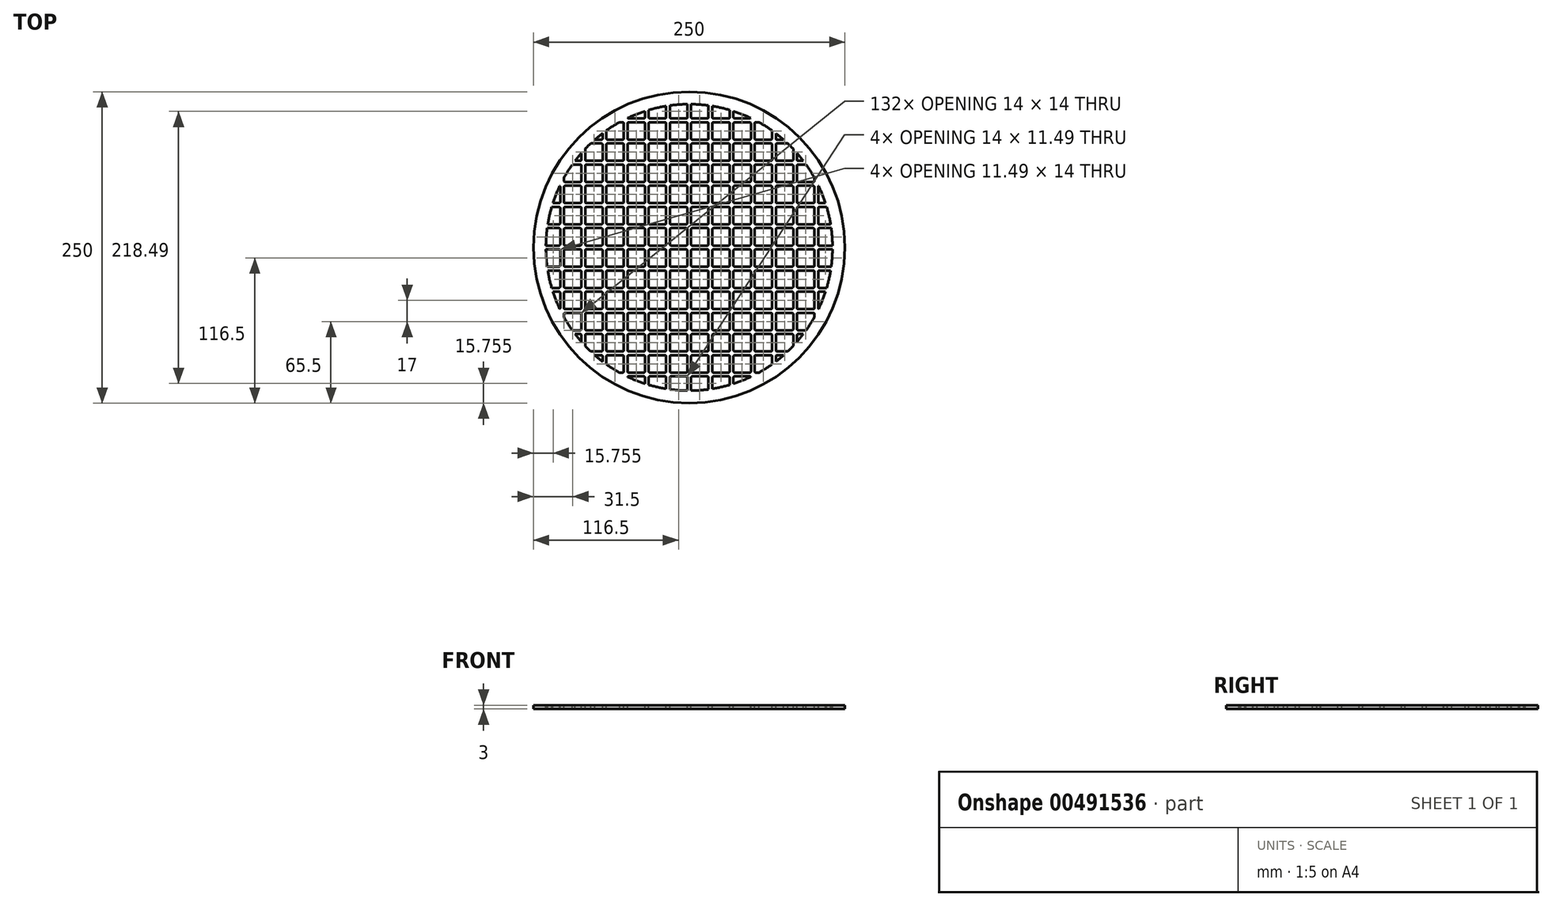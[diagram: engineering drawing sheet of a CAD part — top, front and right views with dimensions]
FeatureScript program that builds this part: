
annotation { "Feature Type Name" : "Feature", "Feature Type Description" : "" }
export const myFeature = defineFeature(function(context is Context, id is Id, definition is map)
    precondition{}
    {
        {
            var Q0;
            Q0=qCreatedBy(makeId("Top.planeOp"),FACE);
            var sketch = newSketch(context, id + "F0", { "sketchPlane" : qUnion([Q0])});
            skCircle(sketch, "E0", {"center": v(0, 0) * mm, "radius": 125 * mm});
            skSolve(sketch);
        }
        {
            var Q0;
            Q0 = qSketchRegion(id + "F0", true);
            extrude(context, id + "F1", {"entities" : qUnion([Q0]), "depth" : 3 * mm});
        }
        {
            var Q0;
            Q0=makeQuery(id+"F1.opExtrude","CAP_FACE",FACE,{"disambiguationData":[OSD([sQuery(id+"F0.wireOp",EDGE,"E0")])],"isStart":false});
            var sketch = newSketch(context, id + "F2", { "sketchPlane" : qUnion([Q0])});
            skLineSegment(sketch, "E1.bottom", {"start": v(2.5, 1.5) * mm, "end": v(14.5, 1.5) * mm});
            skLineSegment(sketch, "E1.top", {"start": v(2.5, 15.5) * mm, "end": v(14.5, 15.5) * mm});
            skLineSegment(sketch, "E1.left", {"start": v(1.5, 2.5) * mm, "end": v(1.5, 14.5) * mm});
            skLineSegment(sketch, "E1.right", {"start": v(15.5, 2.5) * mm, "end": v(15.5, 14.5) * mm});
            skPoint(sketch, "E2.visualSharp", {"position": v(1.5, 15.5) * mm});
            skArc(sketch, "E2.filletArc", {"start": v(2.5, 15.5) * mm, "mid": v(1.8, 15.2) * mm, "end": v(1.5, 14.5) * mm});
            skPoint(sketch, "E3.visualSharp", {"position": v(15.5, 15.5) * mm});
            skArc(sketch, "E3.filletArc", {"start": v(15.5, 14.5) * mm, "mid": v(15.2, 15.2) * mm, "end": v(14.5, 15.5) * mm});
            skPoint(sketch, "E4.visualSharp", {"position": v(1.5, 1.5) * mm});
            skArc(sketch, "E4.filletArc", {"start": v(1.5, 2.5) * mm, "mid": v(1.8, 1.8) * mm, "end": v(2.5, 1.5) * mm});
            skPoint(sketch, "E5.visualSharp", {"position": v(15.5, 1.5) * mm});
            skArc(sketch, "E5.filletArc", {"start": v(14.5, 1.5) * mm, "mid": v(15.2, 1.8) * mm, "end": v(15.5, 2.5) * mm});
            skLineSegment(sketch, "E6.0.1.0", {"start": v(2.5, 18.5) * mm, "end": v(14.5, 18.5) * mm});
            skPoint(sketch, "E6.0.1.1", {"position": v(1.5, 32.5) * mm});
            skArc(sketch, "E6.0.1.2", {"start": v(14.5, 18.5) * mm, "mid": v(15.2, 18.8) * mm, "end": v(15.5, 19.5) * mm});
            skLineSegment(sketch, "E6.0.1.3", {"start": v(15.5, 19.5) * mm, "end": v(15.5, 31.5) * mm});
            skArc(sketch, "E6.0.1.4", {"start": v(15.5, 31.5) * mm, "mid": v(15.2, 32.2) * mm, "end": v(14.5, 32.5) * mm});
            skLineSegment(sketch, "E6.0.1.5", {"start": v(1.5, 19.5) * mm, "end": v(1.5, 31.5) * mm});
            skPoint(sketch, "E6.0.1.6", {"position": v(1.5, 18.5) * mm});
            skArc(sketch, "E6.0.1.7", {"start": v(2.5, 32.5) * mm, "mid": v(1.8, 32.2) * mm, "end": v(1.5, 31.5) * mm});
            skLineSegment(sketch, "E6.0.1.8", {"start": v(2.5, 32.5) * mm, "end": v(14.5, 32.5) * mm});
            skPoint(sketch, "E6.0.1.9", {"position": v(15.5, 32.5) * mm});
            skPoint(sketch, "E6.0.1.10", {"position": v(15.5, 18.5) * mm});
            skArc(sketch, "E6.0.1.11", {"start": v(1.5, 19.5) * mm, "mid": v(1.8, 18.8) * mm, "end": v(2.5, 18.5) * mm});
            skLineSegment(sketch, "E6.0.2.0", {"start": v(2.5, 35.5) * mm, "end": v(14.5, 35.5) * mm});
            skPoint(sketch, "E6.0.2.1", {"position": v(1.5, 49.5) * mm});
            skArc(sketch, "E6.0.2.2", {"start": v(14.5, 35.5) * mm, "mid": v(15.2, 35.8) * mm, "end": v(15.5, 36.5) * mm});
            skLineSegment(sketch, "E6.0.2.3", {"start": v(15.5, 36.5) * mm, "end": v(15.5, 48.5) * mm});
            skArc(sketch, "E6.0.2.4", {"start": v(15.5, 48.5) * mm, "mid": v(15.2, 49.2) * mm, "end": v(14.5, 49.5) * mm});
            skLineSegment(sketch, "E6.0.2.5", {"start": v(1.5, 36.5) * mm, "end": v(1.5, 48.5) * mm});
            skPoint(sketch, "E6.0.2.6", {"position": v(1.5, 35.5) * mm});
            skArc(sketch, "E6.0.2.7", {"start": v(2.5, 49.5) * mm, "mid": v(1.8, 49.2) * mm, "end": v(1.5, 48.5) * mm});
            skLineSegment(sketch, "E6.0.2.8", {"start": v(2.5, 49.5) * mm, "end": v(14.5, 49.5) * mm});
            skPoint(sketch, "E6.0.2.9", {"position": v(15.5, 49.5) * mm});
            skPoint(sketch, "E6.0.2.10", {"position": v(15.5, 35.5) * mm});
            skArc(sketch, "E6.0.2.11", {"start": v(1.5, 36.5) * mm, "mid": v(1.8, 35.8) * mm, "end": v(2.5, 35.5) * mm});
            skLineSegment(sketch, "E6.0.3.0", {"start": v(2.5, 52.5) * mm, "end": v(14.5, 52.5) * mm});
            skPoint(sketch, "E6.0.3.1", {"position": v(1.5, 66.5) * mm});
            skArc(sketch, "E6.0.3.2", {"start": v(14.5, 52.5) * mm, "mid": v(15.2, 52.8) * mm, "end": v(15.5, 53.5) * mm});
            skLineSegment(sketch, "E6.0.3.3", {"start": v(15.5, 53.5) * mm, "end": v(15.5, 65.5) * mm});
            skArc(sketch, "E6.0.3.4", {"start": v(15.5, 65.5) * mm, "mid": v(15.2, 66.2) * mm, "end": v(14.5, 66.5) * mm});
            skLineSegment(sketch, "E6.0.3.5", {"start": v(1.5, 53.5) * mm, "end": v(1.5, 65.5) * mm});
            skPoint(sketch, "E6.0.3.6", {"position": v(1.5, 52.5) * mm});
            skArc(sketch, "E6.0.3.7", {"start": v(2.5, 66.5) * mm, "mid": v(1.8, 66.2) * mm, "end": v(1.5, 65.5) * mm});
            skLineSegment(sketch, "E6.0.3.8", {"start": v(2.5, 66.5) * mm, "end": v(14.5, 66.5) * mm});
            skPoint(sketch, "E6.0.3.9", {"position": v(15.5, 66.5) * mm});
            skPoint(sketch, "E6.0.3.10", {"position": v(15.5, 52.5) * mm});
            skArc(sketch, "E6.0.3.11", {"start": v(1.5, 53.5) * mm, "mid": v(1.8, 52.8) * mm, "end": v(2.5, 52.5) * mm});
            skLineSegment(sketch, "E6.0.4.0", {"start": v(2.5, 69.5) * mm, "end": v(14.5, 69.5) * mm});
            skPoint(sketch, "E6.0.4.1", {"position": v(1.5, 83.5) * mm});
            skArc(sketch, "E6.0.4.2", {"start": v(14.5, 69.5) * mm, "mid": v(15.2, 69.8) * mm, "end": v(15.5, 70.5) * mm});
            skLineSegment(sketch, "E6.0.4.3", {"start": v(15.5, 70.5) * mm, "end": v(15.5, 82.5) * mm});
            skArc(sketch, "E6.0.4.4", {"start": v(15.5, 82.5) * mm, "mid": v(15.2, 83.2) * mm, "end": v(14.5, 83.5) * mm});
            skLineSegment(sketch, "E6.0.4.5", {"start": v(1.5, 70.5) * mm, "end": v(1.5, 82.5) * mm});
            skPoint(sketch, "E6.0.4.6", {"position": v(1.5, 69.5) * mm});
            skArc(sketch, "E6.0.4.7", {"start": v(2.5, 83.5) * mm, "mid": v(1.8, 83.2) * mm, "end": v(1.5, 82.5) * mm});
            skLineSegment(sketch, "E6.0.4.8", {"start": v(2.5, 83.5) * mm, "end": v(14.5, 83.5) * mm});
            skPoint(sketch, "E6.0.4.9", {"position": v(15.5, 83.5) * mm});
            skPoint(sketch, "E6.0.4.10", {"position": v(15.5, 69.5) * mm});
            skArc(sketch, "E6.0.4.11", {"start": v(1.5, 70.5) * mm, "mid": v(1.8, 69.8) * mm, "end": v(2.5, 69.5) * mm});
            skLineSegment(sketch, "E6.0.5.0", {"start": v(2.5, 86.5) * mm, "end": v(14.5, 86.5) * mm});
            skPoint(sketch, "E6.0.5.1", {"position": v(1.5, 100.5) * mm});
            skArc(sketch, "E6.0.5.2", {"start": v(14.5, 86.5) * mm, "mid": v(15.2, 86.8) * mm, "end": v(15.5, 87.5) * mm});
            skLineSegment(sketch, "E6.0.5.3", {"start": v(15.5, 87.5) * mm, "end": v(15.5, 99.5) * mm});
            skArc(sketch, "E6.0.5.4", {"start": v(15.5, 99.5) * mm, "mid": v(15.2, 100.2) * mm, "end": v(14.5, 100.5) * mm});
            skLineSegment(sketch, "E6.0.5.5", {"start": v(1.5, 87.5) * mm, "end": v(1.5, 99.5) * mm});
            skPoint(sketch, "E6.0.5.6", {"position": v(1.5, 86.5) * mm});
            skArc(sketch, "E6.0.5.7", {"start": v(2.5, 100.5) * mm, "mid": v(1.8, 100.2) * mm, "end": v(1.5, 99.5) * mm});
            skLineSegment(sketch, "E6.0.5.8", {"start": v(2.5, 100.5) * mm, "end": v(14.5, 100.5) * mm});
            skPoint(sketch, "E6.0.5.9", {"position": v(15.5, 100.5) * mm});
            skPoint(sketch, "E6.0.5.10", {"position": v(15.5, 86.5) * mm});
            skArc(sketch, "E6.0.5.11", {"start": v(1.5, 87.5) * mm, "mid": v(1.8, 86.8) * mm, "end": v(2.5, 86.5) * mm});
            skLineSegment(sketch, "E6.0.6.0", {"start": v(2.5, 103.5) * mm, "end": v(14.5, 103.5) * mm});
            skArc(sketch, "E6.0.6.2", {"start": v(14.5, 103.5) * mm, "mid": v(15.2, 103.8) * mm, "end": v(15.5, 104.5) * mm});
            skLineSegment(sketch, "E6.0.6.3", {"start": v(15.5, 104.5) * mm, "end": v(15.5, 113.95) * mm});
            skLineSegment(sketch, "E6.0.6.5", {"start": v(1.5, 104.5) * mm, "end": v(1.5, 115) * mm});
            skPoint(sketch, "E6.0.6.6", {"position": v(1.5, 103.5) * mm});
            skPoint(sketch, "E6.0.6.10", {"position": v(15.5, 103.5) * mm});
            skArc(sketch, "E6.0.6.11", {"start": v(1.5, 104.5) * mm, "mid": v(1.8, 103.8) * mm, "end": v(2.5, 103.5) * mm});
            skLineSegment(sketch, "E6.1.0.0", {"start": v(19.5, 1.5) * mm, "end": v(31.5, 1.5) * mm});
            skPoint(sketch, "E6.1.0.1", {"position": v(18.5, 15.5) * mm});
            skArc(sketch, "E6.1.0.2", {"start": v(31.5, 1.5) * mm, "mid": v(32.2, 1.8) * mm, "end": v(32.5, 2.5) * mm});
            skLineSegment(sketch, "E6.1.0.3", {"start": v(32.5, 2.5) * mm, "end": v(32.5, 14.5) * mm});
            skArc(sketch, "E6.1.0.4", {"start": v(32.5, 14.5) * mm, "mid": v(32.2, 15.2) * mm, "end": v(31.5, 15.5) * mm});
            skLineSegment(sketch, "E6.1.0.5", {"start": v(18.5, 2.5) * mm, "end": v(18.5, 14.5) * mm});
            skPoint(sketch, "E6.1.0.6", {"position": v(18.5, 1.5) * mm});
            skArc(sketch, "E6.1.0.7", {"start": v(19.5, 15.5) * mm, "mid": v(18.8, 15.2) * mm, "end": v(18.5, 14.5) * mm});
            skLineSegment(sketch, "E6.1.0.8", {"start": v(19.5, 15.5) * mm, "end": v(31.5, 15.5) * mm});
            skPoint(sketch, "E6.1.0.9", {"position": v(32.5, 15.5) * mm});
            skPoint(sketch, "E6.1.0.10", {"position": v(32.5, 1.5) * mm});
            skArc(sketch, "E6.1.0.11", {"start": v(18.5, 2.5) * mm, "mid": v(18.8, 1.8) * mm, "end": v(19.5, 1.5) * mm});
            skLineSegment(sketch, "E6.1.1.0", {"start": v(19.5, 18.5) * mm, "end": v(31.5, 18.5) * mm});
            skPoint(sketch, "E6.1.1.1", {"position": v(18.5, 32.5) * mm});
            skArc(sketch, "E6.1.1.2", {"start": v(31.5, 18.5) * mm, "mid": v(32.2, 18.8) * mm, "end": v(32.5, 19.5) * mm});
            skLineSegment(sketch, "E6.1.1.3", {"start": v(32.5, 19.5) * mm, "end": v(32.5, 31.5) * mm});
            skArc(sketch, "E6.1.1.4", {"start": v(32.5, 31.5) * mm, "mid": v(32.2, 32.2) * mm, "end": v(31.5, 32.5) * mm});
            skLineSegment(sketch, "E6.1.1.5", {"start": v(18.5, 19.5) * mm, "end": v(18.5, 31.5) * mm});
            skPoint(sketch, "E6.1.1.6", {"position": v(18.5, 18.5) * mm});
            skArc(sketch, "E6.1.1.7", {"start": v(19.5, 32.5) * mm, "mid": v(18.8, 32.2) * mm, "end": v(18.5, 31.5) * mm});
            skLineSegment(sketch, "E6.1.1.8", {"start": v(19.5, 32.5) * mm, "end": v(31.5, 32.5) * mm});
            skPoint(sketch, "E6.1.1.9", {"position": v(32.5, 32.5) * mm});
            skPoint(sketch, "E6.1.1.10", {"position": v(32.5, 18.5) * mm});
            skArc(sketch, "E6.1.1.11", {"start": v(18.5, 19.5) * mm, "mid": v(18.8, 18.8) * mm, "end": v(19.5, 18.5) * mm});
            skLineSegment(sketch, "E6.1.2.0", {"start": v(19.5, 35.5) * mm, "end": v(31.5, 35.5) * mm});
            skPoint(sketch, "E6.1.2.1", {"position": v(18.5, 49.5) * mm});
            skArc(sketch, "E6.1.2.2", {"start": v(31.5, 35.5) * mm, "mid": v(32.2, 35.8) * mm, "end": v(32.5, 36.5) * mm});
            skLineSegment(sketch, "E6.1.2.3", {"start": v(32.5, 36.5) * mm, "end": v(32.5, 48.5) * mm});
            skArc(sketch, "E6.1.2.4", {"start": v(32.5, 48.5) * mm, "mid": v(32.2, 49.2) * mm, "end": v(31.5, 49.5) * mm});
            skLineSegment(sketch, "E6.1.2.5", {"start": v(18.5, 36.5) * mm, "end": v(18.5, 48.5) * mm});
            skPoint(sketch, "E6.1.2.6", {"position": v(18.5, 35.5) * mm});
            skArc(sketch, "E6.1.2.7", {"start": v(19.5, 49.5) * mm, "mid": v(18.8, 49.2) * mm, "end": v(18.5, 48.5) * mm});
            skLineSegment(sketch, "E6.1.2.8", {"start": v(19.5, 49.5) * mm, "end": v(31.5, 49.5) * mm});
            skPoint(sketch, "E6.1.2.9", {"position": v(32.5, 49.5) * mm});
            skPoint(sketch, "E6.1.2.10", {"position": v(32.5, 35.5) * mm});
            skArc(sketch, "E6.1.2.11", {"start": v(18.5, 36.5) * mm, "mid": v(18.8, 35.8) * mm, "end": v(19.5, 35.5) * mm});
            skLineSegment(sketch, "E6.1.3.0", {"start": v(19.5, 52.5) * mm, "end": v(31.5, 52.5) * mm});
            skPoint(sketch, "E6.1.3.1", {"position": v(18.5, 66.5) * mm});
            skArc(sketch, "E6.1.3.2", {"start": v(31.5, 52.5) * mm, "mid": v(32.2, 52.8) * mm, "end": v(32.5, 53.5) * mm});
            skLineSegment(sketch, "E6.1.3.3", {"start": v(32.5, 53.5) * mm, "end": v(32.5, 65.5) * mm});
            skArc(sketch, "E6.1.3.4", {"start": v(32.5, 65.5) * mm, "mid": v(32.2, 66.2) * mm, "end": v(31.5, 66.5) * mm});
            skLineSegment(sketch, "E6.1.3.5", {"start": v(18.5, 53.5) * mm, "end": v(18.5, 65.5) * mm});
            skPoint(sketch, "E6.1.3.6", {"position": v(18.5, 52.5) * mm});
            skArc(sketch, "E6.1.3.7", {"start": v(19.5, 66.5) * mm, "mid": v(18.8, 66.2) * mm, "end": v(18.5, 65.5) * mm});
            skLineSegment(sketch, "E6.1.3.8", {"start": v(19.5, 66.5) * mm, "end": v(31.5, 66.5) * mm});
            skPoint(sketch, "E6.1.3.9", {"position": v(32.5, 66.5) * mm});
            skPoint(sketch, "E6.1.3.10", {"position": v(32.5, 52.5) * mm});
            skArc(sketch, "E6.1.3.11", {"start": v(18.5, 53.5) * mm, "mid": v(18.8, 52.8) * mm, "end": v(19.5, 52.5) * mm});
            skLineSegment(sketch, "E6.1.4.0", {"start": v(19.5, 69.5) * mm, "end": v(31.5, 69.5) * mm});
            skPoint(sketch, "E6.1.4.1", {"position": v(18.5, 83.5) * mm});
            skArc(sketch, "E6.1.4.2", {"start": v(31.5, 69.5) * mm, "mid": v(32.2, 69.8) * mm, "end": v(32.5, 70.5) * mm});
            skLineSegment(sketch, "E6.1.4.3", {"start": v(32.5, 70.5) * mm, "end": v(32.5, 82.5) * mm});
            skArc(sketch, "E6.1.4.4", {"start": v(32.5, 82.5) * mm, "mid": v(32.2, 83.2) * mm, "end": v(31.5, 83.5) * mm});
            skLineSegment(sketch, "E6.1.4.5", {"start": v(18.5, 70.5) * mm, "end": v(18.5, 82.5) * mm});
            skPoint(sketch, "E6.1.4.6", {"position": v(18.5, 69.5) * mm});
            skArc(sketch, "E6.1.4.7", {"start": v(19.5, 83.5) * mm, "mid": v(18.8, 83.2) * mm, "end": v(18.5, 82.5) * mm});
            skLineSegment(sketch, "E6.1.4.8", {"start": v(19.5, 83.5) * mm, "end": v(31.5, 83.5) * mm});
            skPoint(sketch, "E6.1.4.9", {"position": v(32.5, 83.5) * mm});
            skPoint(sketch, "E6.1.4.10", {"position": v(32.5, 69.5) * mm});
            skArc(sketch, "E6.1.4.11", {"start": v(18.5, 70.5) * mm, "mid": v(18.8, 69.8) * mm, "end": v(19.5, 69.5) * mm});
            skLineSegment(sketch, "E6.1.5.0", {"start": v(19.5, 86.5) * mm, "end": v(31.5, 86.5) * mm});
            skPoint(sketch, "E6.1.5.1", {"position": v(18.5, 100.5) * mm});
            skArc(sketch, "E6.1.5.2", {"start": v(31.5, 86.5) * mm, "mid": v(32.2, 86.8) * mm, "end": v(32.5, 87.5) * mm});
            skLineSegment(sketch, "E6.1.5.3", {"start": v(32.5, 87.5) * mm, "end": v(32.5, 99.5) * mm});
            skArc(sketch, "E6.1.5.4", {"start": v(32.5, 99.5) * mm, "mid": v(32.2, 100.2) * mm, "end": v(31.5, 100.5) * mm});
            skLineSegment(sketch, "E6.1.5.5", {"start": v(18.5, 87.5) * mm, "end": v(18.5, 99.5) * mm});
            skPoint(sketch, "E6.1.5.6", {"position": v(18.5, 86.5) * mm});
            skArc(sketch, "E6.1.5.7", {"start": v(19.5, 100.5) * mm, "mid": v(18.8, 100.2) * mm, "end": v(18.5, 99.5) * mm});
            skLineSegment(sketch, "E6.1.5.8", {"start": v(19.5, 100.5) * mm, "end": v(31.5, 100.5) * mm});
            skPoint(sketch, "E6.1.5.9", {"position": v(32.5, 100.5) * mm});
            skPoint(sketch, "E6.1.5.10", {"position": v(32.5, 86.5) * mm});
            skArc(sketch, "E6.1.5.11", {"start": v(18.5, 87.5) * mm, "mid": v(18.8, 86.8) * mm, "end": v(19.5, 86.5) * mm});
            skLineSegment(sketch, "E6.1.6.0", {"start": v(19.5, 103.5) * mm, "end": v(31.5, 103.5) * mm});
            skArc(sketch, "E6.1.6.2", {"start": v(31.5, 103.5) * mm, "mid": v(32.2, 103.8) * mm, "end": v(32.5, 104.5) * mm});
            skLineSegment(sketch, "E6.1.6.3", {"start": v(32.5, 104.5) * mm, "end": v(32.5, 110.31) * mm});
            skLineSegment(sketch, "E6.1.6.5", {"start": v(18.5, 104.5) * mm, "end": v(18.5, 113.5) * mm});
            skPoint(sketch, "E6.1.6.6", {"position": v(18.5, 103.5) * mm});
            skPoint(sketch, "E6.1.6.10", {"position": v(32.5, 103.5) * mm});
            skArc(sketch, "E6.1.6.11", {"start": v(18.5, 104.5) * mm, "mid": v(18.8, 103.8) * mm, "end": v(19.5, 103.5) * mm});
            skLineSegment(sketch, "E6.2.0.0", {"start": v(36.5, 1.5) * mm, "end": v(48.5, 1.5) * mm});
            skPoint(sketch, "E6.2.0.1", {"position": v(35.5, 15.5) * mm});
            skArc(sketch, "E6.2.0.2", {"start": v(48.5, 1.5) * mm, "mid": v(49.2, 1.8) * mm, "end": v(49.5, 2.5) * mm});
            skLineSegment(sketch, "E6.2.0.3", {"start": v(49.5, 2.5) * mm, "end": v(49.5, 14.5) * mm});
            skArc(sketch, "E6.2.0.4", {"start": v(49.5, 14.5) * mm, "mid": v(49.2, 15.2) * mm, "end": v(48.5, 15.5) * mm});
            skLineSegment(sketch, "E6.2.0.5", {"start": v(35.5, 2.5) * mm, "end": v(35.5, 14.5) * mm});
            skPoint(sketch, "E6.2.0.6", {"position": v(35.5, 1.5) * mm});
            skArc(sketch, "E6.2.0.7", {"start": v(36.5, 15.5) * mm, "mid": v(35.8, 15.2) * mm, "end": v(35.5, 14.5) * mm});
            skLineSegment(sketch, "E6.2.0.8", {"start": v(36.5, 15.5) * mm, "end": v(48.5, 15.5) * mm});
            skPoint(sketch, "E6.2.0.9", {"position": v(49.5, 15.5) * mm});
            skPoint(sketch, "E6.2.0.10", {"position": v(49.5, 1.5) * mm});
            skArc(sketch, "E6.2.0.11", {"start": v(35.5, 2.5) * mm, "mid": v(35.8, 1.8) * mm, "end": v(36.5, 1.5) * mm});
            skLineSegment(sketch, "E6.2.1.0", {"start": v(36.5, 18.5) * mm, "end": v(48.5, 18.5) * mm});
            skPoint(sketch, "E6.2.1.1", {"position": v(35.5, 32.5) * mm});
            skArc(sketch, "E6.2.1.2", {"start": v(48.5, 18.5) * mm, "mid": v(49.2, 18.8) * mm, "end": v(49.5, 19.5) * mm});
            skLineSegment(sketch, "E6.2.1.3", {"start": v(49.5, 19.5) * mm, "end": v(49.5, 31.5) * mm});
            skArc(sketch, "E6.2.1.4", {"start": v(49.5, 31.5) * mm, "mid": v(49.2, 32.2) * mm, "end": v(48.5, 32.5) * mm});
            skLineSegment(sketch, "E6.2.1.5", {"start": v(35.5, 19.5) * mm, "end": v(35.5, 31.5) * mm});
            skPoint(sketch, "E6.2.1.6", {"position": v(35.5, 18.5) * mm});
            skArc(sketch, "E6.2.1.7", {"start": v(36.5, 32.5) * mm, "mid": v(35.8, 32.2) * mm, "end": v(35.5, 31.5) * mm});
            skLineSegment(sketch, "E6.2.1.8", {"start": v(36.5, 32.5) * mm, "end": v(48.5, 32.5) * mm});
            skPoint(sketch, "E6.2.1.9", {"position": v(49.5, 32.5) * mm});
            skPoint(sketch, "E6.2.1.10", {"position": v(49.5, 18.5) * mm});
            skArc(sketch, "E6.2.1.11", {"start": v(35.5, 19.5) * mm, "mid": v(35.8, 18.8) * mm, "end": v(36.5, 18.5) * mm});
            skLineSegment(sketch, "E6.2.2.0", {"start": v(36.5, 35.5) * mm, "end": v(48.5, 35.5) * mm});
            skPoint(sketch, "E6.2.2.1", {"position": v(35.5, 49.5) * mm});
            skArc(sketch, "E6.2.2.2", {"start": v(48.5, 35.5) * mm, "mid": v(49.2, 35.8) * mm, "end": v(49.5, 36.5) * mm});
            skLineSegment(sketch, "E6.2.2.3", {"start": v(49.5, 36.5) * mm, "end": v(49.5, 48.5) * mm});
            skArc(sketch, "E6.2.2.4", {"start": v(49.5, 48.5) * mm, "mid": v(49.2, 49.2) * mm, "end": v(48.5, 49.5) * mm});
            skLineSegment(sketch, "E6.2.2.5", {"start": v(35.5, 36.5) * mm, "end": v(35.5, 48.5) * mm});
            skPoint(sketch, "E6.2.2.6", {"position": v(35.5, 35.5) * mm});
            skArc(sketch, "E6.2.2.7", {"start": v(36.5, 49.5) * mm, "mid": v(35.8, 49.2) * mm, "end": v(35.5, 48.5) * mm});
            skLineSegment(sketch, "E6.2.2.8", {"start": v(36.5, 49.5) * mm, "end": v(48.5, 49.5) * mm});
            skPoint(sketch, "E6.2.2.9", {"position": v(49.5, 49.5) * mm});
            skPoint(sketch, "E6.2.2.10", {"position": v(49.5, 35.5) * mm});
            skArc(sketch, "E6.2.2.11", {"start": v(35.5, 36.5) * mm, "mid": v(35.8, 35.8) * mm, "end": v(36.5, 35.5) * mm});
            skLineSegment(sketch, "E6.2.3.0", {"start": v(36.5, 52.5) * mm, "end": v(48.5, 52.5) * mm});
            skPoint(sketch, "E6.2.3.1", {"position": v(35.5, 66.5) * mm});
            skArc(sketch, "E6.2.3.2", {"start": v(48.5, 52.5) * mm, "mid": v(49.2, 52.8) * mm, "end": v(49.5, 53.5) * mm});
            skLineSegment(sketch, "E6.2.3.3", {"start": v(49.5, 53.5) * mm, "end": v(49.5, 65.5) * mm});
            skArc(sketch, "E6.2.3.4", {"start": v(49.5, 65.5) * mm, "mid": v(49.2, 66.2) * mm, "end": v(48.5, 66.5) * mm});
            skLineSegment(sketch, "E6.2.3.5", {"start": v(35.5, 53.5) * mm, "end": v(35.5, 65.5) * mm});
            skPoint(sketch, "E6.2.3.6", {"position": v(35.5, 52.5) * mm});
            skArc(sketch, "E6.2.3.7", {"start": v(36.5, 66.5) * mm, "mid": v(35.8, 66.2) * mm, "end": v(35.5, 65.5) * mm});
            skLineSegment(sketch, "E6.2.3.8", {"start": v(36.5, 66.5) * mm, "end": v(48.5, 66.5) * mm});
            skPoint(sketch, "E6.2.3.9", {"position": v(49.5, 66.5) * mm});
            skPoint(sketch, "E6.2.3.10", {"position": v(49.5, 52.5) * mm});
            skArc(sketch, "E6.2.3.11", {"start": v(35.5, 53.5) * mm, "mid": v(35.8, 52.8) * mm, "end": v(36.5, 52.5) * mm});
            skLineSegment(sketch, "E6.2.4.0", {"start": v(36.5, 69.5) * mm, "end": v(48.5, 69.5) * mm});
            skPoint(sketch, "E6.2.4.1", {"position": v(35.5, 83.5) * mm});
            skArc(sketch, "E6.2.4.2", {"start": v(48.5, 69.5) * mm, "mid": v(49.2, 69.8) * mm, "end": v(49.5, 70.5) * mm});
            skLineSegment(sketch, "E6.2.4.3", {"start": v(49.5, 70.5) * mm, "end": v(49.5, 82.5) * mm});
            skArc(sketch, "E6.2.4.4", {"start": v(49.5, 82.5) * mm, "mid": v(49.2, 83.2) * mm, "end": v(48.5, 83.5) * mm});
            skLineSegment(sketch, "E6.2.4.5", {"start": v(35.5, 70.5) * mm, "end": v(35.5, 82.5) * mm});
            skPoint(sketch, "E6.2.4.6", {"position": v(35.5, 69.5) * mm});
            skArc(sketch, "E6.2.4.7", {"start": v(36.5, 83.5) * mm, "mid": v(35.8, 83.2) * mm, "end": v(35.5, 82.5) * mm});
            skLineSegment(sketch, "E6.2.4.8", {"start": v(36.5, 83.5) * mm, "end": v(48.5, 83.5) * mm});
            skPoint(sketch, "E6.2.4.9", {"position": v(49.5, 83.5) * mm});
            skPoint(sketch, "E6.2.4.10", {"position": v(49.5, 69.5) * mm});
            skArc(sketch, "E6.2.4.11", {"start": v(35.5, 70.5) * mm, "mid": v(35.8, 69.8) * mm, "end": v(36.5, 69.5) * mm});
            skLineSegment(sketch, "E6.2.5.0", {"start": v(36.5, 86.5) * mm, "end": v(48.5, 86.5) * mm});
            skPoint(sketch, "E6.2.5.1", {"position": v(35.5, 100.5) * mm});
            skArc(sketch, "E6.2.5.2", {"start": v(48.5, 86.5) * mm, "mid": v(49.2, 86.8) * mm, "end": v(49.5, 87.5) * mm});
            skLineSegment(sketch, "E6.2.5.3", {"start": v(49.5, 87.5) * mm, "end": v(49.5, 99.5) * mm});
            skArc(sketch, "E6.2.5.4", {"start": v(49.5, 99.5) * mm, "mid": v(49.2, 100.2) * mm, "end": v(48.5, 100.5) * mm});
            skLineSegment(sketch, "E6.2.5.5", {"start": v(35.5, 87.5) * mm, "end": v(35.5, 99.5) * mm});
            skPoint(sketch, "E6.2.5.6", {"position": v(35.5, 86.5) * mm});
            skArc(sketch, "E6.2.5.7", {"start": v(36.5, 100.5) * mm, "mid": v(35.8, 100.2) * mm, "end": v(35.5, 99.5) * mm});
            skLineSegment(sketch, "E6.2.5.8", {"start": v(36.5, 100.5) * mm, "end": v(48.5, 100.5) * mm});
            skPoint(sketch, "E6.2.5.9", {"position": v(49.5, 100.5) * mm});
            skPoint(sketch, "E6.2.5.10", {"position": v(49.5, 86.5) * mm});
            skArc(sketch, "E6.2.5.11", {"start": v(35.5, 87.5) * mm, "mid": v(35.8, 86.8) * mm, "end": v(36.5, 86.5) * mm});
            skLineSegment(sketch, "E6.2.6.0", {"start": v(36.5, 103.5) * mm, "end": v(48.5, 103.5) * mm});
            skArc(sketch, "E6.2.6.2", {"start": v(48.5, 103.5) * mm, "mid": v(48.95, 103.6) * mm, "end": v(49.3, 103.9) * mm});
            skLineSegment(sketch, "E6.2.6.5", {"start": v(35.5, 104.5) * mm, "end": v(35.5, 109.38) * mm});
            skPoint(sketch, "E6.2.6.6", {"position": v(35.5, 103.5) * mm});
            skPoint(sketch, "E6.2.6.10", {"position": v(49.5, 103.5) * mm});
            skArc(sketch, "E6.2.6.11", {"start": v(35.5, 104.5) * mm, "mid": v(35.8, 103.8) * mm, "end": v(36.5, 103.5) * mm});
            skLineSegment(sketch, "E6.3.0.0", {"start": v(53.5, 1.5) * mm, "end": v(65.5, 1.5) * mm});
            skPoint(sketch, "E6.3.0.1", {"position": v(52.5, 15.5) * mm});
            skArc(sketch, "E6.3.0.2", {"start": v(65.5, 1.5) * mm, "mid": v(66.2, 1.8) * mm, "end": v(66.5, 2.5) * mm});
            skLineSegment(sketch, "E6.3.0.3", {"start": v(66.5, 2.5) * mm, "end": v(66.5, 14.5) * mm});
            skArc(sketch, "E6.3.0.4", {"start": v(66.5, 14.5) * mm, "mid": v(66.2, 15.2) * mm, "end": v(65.5, 15.5) * mm});
            skLineSegment(sketch, "E6.3.0.5", {"start": v(52.5, 2.5) * mm, "end": v(52.5, 14.5) * mm});
            skPoint(sketch, "E6.3.0.6", {"position": v(52.5, 1.5) * mm});
            skArc(sketch, "E6.3.0.7", {"start": v(53.5, 15.5) * mm, "mid": v(52.8, 15.2) * mm, "end": v(52.5, 14.5) * mm});
            skLineSegment(sketch, "E6.3.0.8", {"start": v(53.5, 15.5) * mm, "end": v(65.5, 15.5) * mm});
            skPoint(sketch, "E6.3.0.9", {"position": v(66.5, 15.5) * mm});
            skPoint(sketch, "E6.3.0.10", {"position": v(66.5, 1.5) * mm});
            skArc(sketch, "E6.3.0.11", {"start": v(52.5, 2.5) * mm, "mid": v(52.8, 1.8) * mm, "end": v(53.5, 1.5) * mm});
            skLineSegment(sketch, "E6.3.1.0", {"start": v(53.5, 18.5) * mm, "end": v(65.5, 18.5) * mm});
            skPoint(sketch, "E6.3.1.1", {"position": v(52.5, 32.5) * mm});
            skArc(sketch, "E6.3.1.2", {"start": v(65.5, 18.5) * mm, "mid": v(66.2, 18.8) * mm, "end": v(66.5, 19.5) * mm});
            skLineSegment(sketch, "E6.3.1.3", {"start": v(66.5, 19.5) * mm, "end": v(66.5, 31.5) * mm});
            skArc(sketch, "E6.3.1.4", {"start": v(66.5, 31.5) * mm, "mid": v(66.2, 32.2) * mm, "end": v(65.5, 32.5) * mm});
            skLineSegment(sketch, "E6.3.1.5", {"start": v(52.5, 19.5) * mm, "end": v(52.5, 31.5) * mm});
            skPoint(sketch, "E6.3.1.6", {"position": v(52.5, 18.5) * mm});
            skArc(sketch, "E6.3.1.7", {"start": v(53.5, 32.5) * mm, "mid": v(52.8, 32.2) * mm, "end": v(52.5, 31.5) * mm});
            skLineSegment(sketch, "E6.3.1.8", {"start": v(53.5, 32.5) * mm, "end": v(65.5, 32.5) * mm});
            skPoint(sketch, "E6.3.1.9", {"position": v(66.5, 32.5) * mm});
            skPoint(sketch, "E6.3.1.10", {"position": v(66.5, 18.5) * mm});
            skArc(sketch, "E6.3.1.11", {"start": v(52.5, 19.5) * mm, "mid": v(52.8, 18.8) * mm, "end": v(53.5, 18.5) * mm});
            skLineSegment(sketch, "E6.3.2.0", {"start": v(53.5, 35.5) * mm, "end": v(65.5, 35.5) * mm});
            skPoint(sketch, "E6.3.2.1", {"position": v(52.5, 49.5) * mm});
            skArc(sketch, "E6.3.2.2", {"start": v(65.5, 35.5) * mm, "mid": v(66.2, 35.8) * mm, "end": v(66.5, 36.5) * mm});
            skLineSegment(sketch, "E6.3.2.3", {"start": v(66.5, 36.5) * mm, "end": v(66.5, 48.5) * mm});
            skArc(sketch, "E6.3.2.4", {"start": v(66.5, 48.5) * mm, "mid": v(66.2, 49.2) * mm, "end": v(65.5, 49.5) * mm});
            skLineSegment(sketch, "E6.3.2.5", {"start": v(52.5, 36.5) * mm, "end": v(52.5, 48.5) * mm});
            skPoint(sketch, "E6.3.2.6", {"position": v(52.5, 35.5) * mm});
            skArc(sketch, "E6.3.2.7", {"start": v(53.5, 49.5) * mm, "mid": v(52.8, 49.2) * mm, "end": v(52.5, 48.5) * mm});
            skLineSegment(sketch, "E6.3.2.8", {"start": v(53.5, 49.5) * mm, "end": v(65.5, 49.5) * mm});
            skPoint(sketch, "E6.3.2.9", {"position": v(66.5, 49.5) * mm});
            skPoint(sketch, "E6.3.2.10", {"position": v(66.5, 35.5) * mm});
            skArc(sketch, "E6.3.2.11", {"start": v(52.5, 36.5) * mm, "mid": v(52.8, 35.8) * mm, "end": v(53.5, 35.5) * mm});
            skLineSegment(sketch, "E6.3.3.0", {"start": v(53.5, 52.5) * mm, "end": v(65.5, 52.5) * mm});
            skPoint(sketch, "E6.3.3.1", {"position": v(52.5, 66.5) * mm});
            skArc(sketch, "E6.3.3.2", {"start": v(65.5, 52.5) * mm, "mid": v(66.2, 52.8) * mm, "end": v(66.5, 53.5) * mm});
            skLineSegment(sketch, "E6.3.3.3", {"start": v(66.5, 53.5) * mm, "end": v(66.5, 65.5) * mm});
            skArc(sketch, "E6.3.3.4", {"start": v(66.5, 65.5) * mm, "mid": v(66.2, 66.2) * mm, "end": v(65.5, 66.5) * mm});
            skLineSegment(sketch, "E6.3.3.5", {"start": v(52.5, 53.5) * mm, "end": v(52.5, 65.5) * mm});
            skPoint(sketch, "E6.3.3.6", {"position": v(52.5, 52.5) * mm});
            skArc(sketch, "E6.3.3.7", {"start": v(53.5, 66.5) * mm, "mid": v(52.8, 66.2) * mm, "end": v(52.5, 65.5) * mm});
            skLineSegment(sketch, "E6.3.3.8", {"start": v(53.5, 66.5) * mm, "end": v(65.5, 66.5) * mm});
            skPoint(sketch, "E6.3.3.9", {"position": v(66.5, 66.5) * mm});
            skPoint(sketch, "E6.3.3.10", {"position": v(66.5, 52.5) * mm});
            skArc(sketch, "E6.3.3.11", {"start": v(52.5, 53.5) * mm, "mid": v(52.8, 52.8) * mm, "end": v(53.5, 52.5) * mm});
            skLineSegment(sketch, "E6.3.4.0", {"start": v(53.5, 69.5) * mm, "end": v(65.5, 69.5) * mm});
            skPoint(sketch, "E6.3.4.1", {"position": v(52.5, 83.5) * mm});
            skArc(sketch, "E6.3.4.2", {"start": v(65.5, 69.5) * mm, "mid": v(66.2, 69.8) * mm, "end": v(66.5, 70.5) * mm});
            skLineSegment(sketch, "E6.3.4.3", {"start": v(66.5, 70.5) * mm, "end": v(66.5, 82.5) * mm});
            skArc(sketch, "E6.3.4.4", {"start": v(66.5, 82.5) * mm, "mid": v(66.2, 83.2) * mm, "end": v(65.5, 83.5) * mm});
            skLineSegment(sketch, "E6.3.4.5", {"start": v(52.5, 70.5) * mm, "end": v(52.5, 82.5) * mm});
            skPoint(sketch, "E6.3.4.6", {"position": v(52.5, 69.5) * mm});
            skArc(sketch, "E6.3.4.7", {"start": v(53.5, 83.5) * mm, "mid": v(52.8, 83.2) * mm, "end": v(52.5, 82.5) * mm});
            skLineSegment(sketch, "E6.3.4.8", {"start": v(53.5, 83.5) * mm, "end": v(65.5, 83.5) * mm});
            skPoint(sketch, "E6.3.4.9", {"position": v(66.5, 83.5) * mm});
            skPoint(sketch, "E6.3.4.10", {"position": v(66.5, 69.5) * mm});
            skArc(sketch, "E6.3.4.11", {"start": v(52.5, 70.5) * mm, "mid": v(52.8, 69.8) * mm, "end": v(53.5, 69.5) * mm});
            skLineSegment(sketch, "E6.3.5.0", {"start": v(53.5, 86.5) * mm, "end": v(65.5, 86.5) * mm});
            skPoint(sketch, "E6.3.5.1", {"position": v(52.5, 100.5) * mm});
            skArc(sketch, "E6.3.5.2", {"start": v(65.5, 86.5) * mm, "mid": v(66.2, 86.8) * mm, "end": v(66.5, 87.5) * mm});
            skLineSegment(sketch, "E6.3.5.3", {"start": v(66.5, 87.5) * mm, "end": v(66.5, 93.82) * mm});
            skLineSegment(sketch, "E6.3.5.5", {"start": v(52.5, 87.5) * mm, "end": v(52.5, 99.5) * mm});
            skPoint(sketch, "E6.3.5.6", {"position": v(52.5, 86.5) * mm});
            skArc(sketch, "E6.3.5.7", {"start": v(53.5, 100.5) * mm, "mid": v(52.8, 100.2) * mm, "end": v(52.5, 99.5) * mm});
            skLineSegment(sketch, "E6.3.5.8", {"start": v(53.5, 100.5) * mm, "end": v(55.9, 100.5) * mm});
            skPoint(sketch, "E6.3.5.10", {"position": v(66.5, 86.5) * mm});
            skArc(sketch, "E6.3.5.11", {"start": v(52.5, 87.5) * mm, "mid": v(52.8, 86.8) * mm, "end": v(53.5, 86.5) * mm});
            skLineSegment(sketch, "E6.4.0.0", {"start": v(70.5, 1.5) * mm, "end": v(82.5, 1.5) * mm});
            skPoint(sketch, "E6.4.0.1", {"position": v(69.5, 15.5) * mm});
            skArc(sketch, "E6.4.0.2", {"start": v(82.5, 1.5) * mm, "mid": v(83.2, 1.8) * mm, "end": v(83.5, 2.5) * mm});
            skLineSegment(sketch, "E6.4.0.3", {"start": v(83.5, 2.5) * mm, "end": v(83.5, 14.5) * mm});
            skArc(sketch, "E6.4.0.4", {"start": v(83.5, 14.5) * mm, "mid": v(83.2, 15.2) * mm, "end": v(82.5, 15.5) * mm});
            skLineSegment(sketch, "E6.4.0.5", {"start": v(69.5, 2.5) * mm, "end": v(69.5, 14.5) * mm});
            skPoint(sketch, "E6.4.0.6", {"position": v(69.5, 1.5) * mm});
            skArc(sketch, "E6.4.0.7", {"start": v(70.5, 15.5) * mm, "mid": v(69.8, 15.2) * mm, "end": v(69.5, 14.5) * mm});
            skLineSegment(sketch, "E6.4.0.8", {"start": v(70.5, 15.5) * mm, "end": v(82.5, 15.5) * mm});
            skPoint(sketch, "E6.4.0.9", {"position": v(83.5, 15.5) * mm});
            skPoint(sketch, "E6.4.0.10", {"position": v(83.5, 1.5) * mm});
            skArc(sketch, "E6.4.0.11", {"start": v(69.5, 2.5) * mm, "mid": v(69.8, 1.8) * mm, "end": v(70.5, 1.5) * mm});
            skLineSegment(sketch, "E6.4.1.0", {"start": v(70.5, 18.5) * mm, "end": v(82.5, 18.5) * mm});
            skPoint(sketch, "E6.4.1.1", {"position": v(69.5, 32.5) * mm});
            skArc(sketch, "E6.4.1.2", {"start": v(82.5, 18.5) * mm, "mid": v(83.2, 18.8) * mm, "end": v(83.5, 19.5) * mm});
            skLineSegment(sketch, "E6.4.1.3", {"start": v(83.5, 19.5) * mm, "end": v(83.5, 31.5) * mm});
            skArc(sketch, "E6.4.1.4", {"start": v(83.5, 31.5) * mm, "mid": v(83.2, 32.2) * mm, "end": v(82.5, 32.5) * mm});
            skLineSegment(sketch, "E6.4.1.5", {"start": v(69.5, 19.5) * mm, "end": v(69.5, 31.5) * mm});
            skPoint(sketch, "E6.4.1.6", {"position": v(69.5, 18.5) * mm});
            skArc(sketch, "E6.4.1.7", {"start": v(70.5, 32.5) * mm, "mid": v(69.8, 32.2) * mm, "end": v(69.5, 31.5) * mm});
            skLineSegment(sketch, "E6.4.1.8", {"start": v(70.5, 32.5) * mm, "end": v(82.5, 32.5) * mm});
            skPoint(sketch, "E6.4.1.9", {"position": v(83.5, 32.5) * mm});
            skPoint(sketch, "E6.4.1.10", {"position": v(83.5, 18.5) * mm});
            skArc(sketch, "E6.4.1.11", {"start": v(69.5, 19.5) * mm, "mid": v(69.8, 18.8) * mm, "end": v(70.5, 18.5) * mm});
            skLineSegment(sketch, "E6.4.2.0", {"start": v(70.5, 35.5) * mm, "end": v(82.5, 35.5) * mm});
            skPoint(sketch, "E6.4.2.1", {"position": v(69.5, 49.5) * mm});
            skArc(sketch, "E6.4.2.2", {"start": v(82.5, 35.5) * mm, "mid": v(83.2, 35.8) * mm, "end": v(83.5, 36.5) * mm});
            skLineSegment(sketch, "E6.4.2.3", {"start": v(83.5, 36.5) * mm, "end": v(83.5, 48.5) * mm});
            skArc(sketch, "E6.4.2.4", {"start": v(83.5, 48.5) * mm, "mid": v(83.2, 49.2) * mm, "end": v(82.5, 49.5) * mm});
            skLineSegment(sketch, "E6.4.2.5", {"start": v(69.5, 36.5) * mm, "end": v(69.5, 48.5) * mm});
            skPoint(sketch, "E6.4.2.6", {"position": v(69.5, 35.5) * mm});
            skArc(sketch, "E6.4.2.7", {"start": v(70.5, 49.5) * mm, "mid": v(69.8, 49.2) * mm, "end": v(69.5, 48.5) * mm});
            skLineSegment(sketch, "E6.4.2.8", {"start": v(70.5, 49.5) * mm, "end": v(82.5, 49.5) * mm});
            skPoint(sketch, "E6.4.2.9", {"position": v(83.5, 49.5) * mm});
            skPoint(sketch, "E6.4.2.10", {"position": v(83.5, 35.5) * mm});
            skArc(sketch, "E6.4.2.11", {"start": v(69.5, 36.5) * mm, "mid": v(69.8, 35.8) * mm, "end": v(70.5, 35.5) * mm});
            skLineSegment(sketch, "E6.4.3.0", {"start": v(70.5, 52.5) * mm, "end": v(82.5, 52.5) * mm});
            skPoint(sketch, "E6.4.3.1", {"position": v(69.5, 66.5) * mm});
            skArc(sketch, "E6.4.3.2", {"start": v(82.5, 52.5) * mm, "mid": v(83.2, 52.8) * mm, "end": v(83.5, 53.5) * mm});
            skLineSegment(sketch, "E6.4.3.3", {"start": v(83.5, 53.5) * mm, "end": v(83.5, 65.5) * mm});
            skArc(sketch, "E6.4.3.4", {"start": v(83.5, 65.5) * mm, "mid": v(83.2, 66.2) * mm, "end": v(82.5, 66.5) * mm});
            skLineSegment(sketch, "E6.4.3.5", {"start": v(69.5, 53.5) * mm, "end": v(69.5, 65.5) * mm});
            skPoint(sketch, "E6.4.3.6", {"position": v(69.5, 52.5) * mm});
            skArc(sketch, "E6.4.3.7", {"start": v(70.5, 66.5) * mm, "mid": v(69.8, 66.2) * mm, "end": v(69.5, 65.5) * mm});
            skLineSegment(sketch, "E6.4.3.8", {"start": v(70.5, 66.5) * mm, "end": v(82.5, 66.5) * mm});
            skPoint(sketch, "E6.4.3.9", {"position": v(83.5, 66.5) * mm});
            skPoint(sketch, "E6.4.3.10", {"position": v(83.5, 52.5) * mm});
            skArc(sketch, "E6.4.3.11", {"start": v(69.5, 53.5) * mm, "mid": v(69.8, 52.8) * mm, "end": v(70.5, 52.5) * mm});
            skLineSegment(sketch, "E6.4.4.0", {"start": v(70.5, 69.5) * mm, "end": v(82.5, 69.5) * mm});
            skPoint(sketch, "E6.4.4.1", {"position": v(69.5, 83.5) * mm});
            skArc(sketch, "E6.4.4.2", {"start": v(82.5, 69.5) * mm, "mid": v(83.2, 69.8) * mm, "end": v(83.5, 70.5) * mm});
            skLineSegment(sketch, "E6.4.4.3", {"start": v(83.5, 70.5) * mm, "end": v(83.5, 79.07) * mm});
            skLineSegment(sketch, "E6.4.4.5", {"start": v(69.5, 70.5) * mm, "end": v(69.5, 82.5) * mm});
            skPoint(sketch, "E6.4.4.6", {"position": v(69.5, 69.5) * mm});
            skArc(sketch, "E6.4.4.7", {"start": v(70.5, 83.5) * mm, "mid": v(69.8, 83.2) * mm, "end": v(69.5, 82.5) * mm});
            skLineSegment(sketch, "E6.4.4.8", {"start": v(70.5, 83.5) * mm, "end": v(79.07, 83.5) * mm});
            skPoint(sketch, "E6.4.4.10", {"position": v(83.5, 69.5) * mm});
            skArc(sketch, "E6.4.4.11", {"start": v(69.5, 70.5) * mm, "mid": v(69.8, 69.8) * mm, "end": v(70.5, 69.5) * mm});
            skLineSegment(sketch, "E6.4.5.0", {"start": v(70.5, 86.5) * mm, "end": v(75.78, 86.5) * mm});
            skLineSegment(sketch, "E6.4.5.5", {"start": v(69.5, 87.5) * mm, "end": v(69.5, 91.62) * mm});
            skPoint(sketch, "E6.4.5.6", {"position": v(69.5, 86.5) * mm});
            skArc(sketch, "E6.4.5.11", {"start": v(69.5, 87.5) * mm, "mid": v(69.8, 86.8) * mm, "end": v(70.5, 86.5) * mm});
            skLineSegment(sketch, "E6.5.0.0", {"start": v(87.5, 1.5) * mm, "end": v(99.5, 1.5) * mm});
            skPoint(sketch, "E6.5.0.1", {"position": v(86.5, 15.5) * mm});
            skArc(sketch, "E6.5.0.2", {"start": v(99.5, 1.5) * mm, "mid": v(100.2, 1.8) * mm, "end": v(100.5, 2.5) * mm});
            skLineSegment(sketch, "E6.5.0.3", {"start": v(100.5, 2.5) * mm, "end": v(100.5, 14.5) * mm});
            skArc(sketch, "E6.5.0.4", {"start": v(100.5, 14.5) * mm, "mid": v(100.2, 15.2) * mm, "end": v(99.5, 15.5) * mm});
            skLineSegment(sketch, "E6.5.0.5", {"start": v(86.5, 2.5) * mm, "end": v(86.5, 14.5) * mm});
            skPoint(sketch, "E6.5.0.6", {"position": v(86.5, 1.5) * mm});
            skArc(sketch, "E6.5.0.7", {"start": v(87.5, 15.5) * mm, "mid": v(86.8, 15.2) * mm, "end": v(86.5, 14.5) * mm});
            skLineSegment(sketch, "E6.5.0.8", {"start": v(87.5, 15.5) * mm, "end": v(99.5, 15.5) * mm});
            skPoint(sketch, "E6.5.0.9", {"position": v(100.5, 15.5) * mm});
            skPoint(sketch, "E6.5.0.10", {"position": v(100.5, 1.5) * mm});
            skArc(sketch, "E6.5.0.11", {"start": v(86.5, 2.5) * mm, "mid": v(86.8, 1.8) * mm, "end": v(87.5, 1.5) * mm});
            skLineSegment(sketch, "E6.5.1.0", {"start": v(87.5, 18.5) * mm, "end": v(99.5, 18.5) * mm});
            skPoint(sketch, "E6.5.1.1", {"position": v(86.5, 32.5) * mm});
            skArc(sketch, "E6.5.1.2", {"start": v(99.5, 18.5) * mm, "mid": v(100.2, 18.8) * mm, "end": v(100.5, 19.5) * mm});
            skLineSegment(sketch, "E6.5.1.3", {"start": v(100.5, 19.5) * mm, "end": v(100.5, 31.5) * mm});
            skArc(sketch, "E6.5.1.4", {"start": v(100.5, 31.5) * mm, "mid": v(100.2, 32.2) * mm, "end": v(99.5, 32.5) * mm});
            skLineSegment(sketch, "E6.5.1.5", {"start": v(86.5, 19.5) * mm, "end": v(86.5, 31.5) * mm});
            skPoint(sketch, "E6.5.1.6", {"position": v(86.5, 18.5) * mm});
            skArc(sketch, "E6.5.1.7", {"start": v(87.5, 32.5) * mm, "mid": v(86.8, 32.2) * mm, "end": v(86.5, 31.5) * mm});
            skLineSegment(sketch, "E6.5.1.8", {"start": v(87.5, 32.5) * mm, "end": v(99.5, 32.5) * mm});
            skPoint(sketch, "E6.5.1.9", {"position": v(100.5, 32.5) * mm});
            skPoint(sketch, "E6.5.1.10", {"position": v(100.5, 18.5) * mm});
            skArc(sketch, "E6.5.1.11", {"start": v(86.5, 19.5) * mm, "mid": v(86.8, 18.8) * mm, "end": v(87.5, 18.5) * mm});
            skLineSegment(sketch, "E6.5.2.0", {"start": v(87.5, 35.5) * mm, "end": v(99.5, 35.5) * mm});
            skPoint(sketch, "E6.5.2.1", {"position": v(86.5, 49.5) * mm});
            skArc(sketch, "E6.5.2.2", {"start": v(99.5, 35.5) * mm, "mid": v(100.2, 35.8) * mm, "end": v(100.5, 36.5) * mm});
            skLineSegment(sketch, "E6.5.2.3", {"start": v(100.5, 36.5) * mm, "end": v(100.5, 48.5) * mm});
            skArc(sketch, "E6.5.2.4", {"start": v(100.5, 48.5) * mm, "mid": v(100.2, 49.2) * mm, "end": v(99.5, 49.5) * mm});
            skLineSegment(sketch, "E6.5.2.5", {"start": v(86.5, 36.5) * mm, "end": v(86.5, 48.5) * mm});
            skPoint(sketch, "E6.5.2.6", {"position": v(86.5, 35.5) * mm});
            skArc(sketch, "E6.5.2.7", {"start": v(87.5, 49.5) * mm, "mid": v(86.8, 49.2) * mm, "end": v(86.5, 48.5) * mm});
            skLineSegment(sketch, "E6.5.2.8", {"start": v(87.5, 49.5) * mm, "end": v(99.5, 49.5) * mm});
            skPoint(sketch, "E6.5.2.9", {"position": v(100.5, 49.5) * mm});
            skPoint(sketch, "E6.5.2.10", {"position": v(100.5, 35.5) * mm});
            skArc(sketch, "E6.5.2.11", {"start": v(86.5, 36.5) * mm, "mid": v(86.8, 35.8) * mm, "end": v(87.5, 35.5) * mm});
            skLineSegment(sketch, "E6.5.3.0", {"start": v(87.5, 52.5) * mm, "end": v(99.5, 52.5) * mm});
            skPoint(sketch, "E6.5.3.1", {"position": v(86.5, 66.5) * mm});
            skArc(sketch, "E6.5.3.2", {"start": v(99.5, 52.5) * mm, "mid": v(100.2, 52.8) * mm, "end": v(100.5, 53.5) * mm});
            skLineSegment(sketch, "E6.5.3.3", {"start": v(100.5, 53.5) * mm, "end": v(100.5, 55.9) * mm});
            skLineSegment(sketch, "E6.5.3.5", {"start": v(86.5, 53.5) * mm, "end": v(86.5, 65.5) * mm});
            skPoint(sketch, "E6.5.3.6", {"position": v(86.5, 52.5) * mm});
            skArc(sketch, "E6.5.3.7", {"start": v(87.5, 66.5) * mm, "mid": v(86.8, 66.2) * mm, "end": v(86.5, 65.5) * mm});
            skLineSegment(sketch, "E6.5.3.8", {"start": v(87.5, 66.5) * mm, "end": v(93.82, 66.5) * mm});
            skPoint(sketch, "E6.5.3.10", {"position": v(100.5, 52.5) * mm});
            skArc(sketch, "E6.5.3.11", {"start": v(86.5, 53.5) * mm, "mid": v(86.8, 52.8) * mm, "end": v(87.5, 52.5) * mm});
            skLineSegment(sketch, "E6.5.4.0", {"start": v(87.5, 69.5) * mm, "end": v(91.62, 69.5) * mm});
            skLineSegment(sketch, "E6.5.4.5", {"start": v(86.5, 70.5) * mm, "end": v(86.5, 75.78) * mm});
            skPoint(sketch, "E6.5.4.6", {"position": v(86.5, 69.5) * mm});
            skArc(sketch, "E6.5.4.11", {"start": v(86.5, 70.5) * mm, "mid": v(86.8, 69.8) * mm, "end": v(87.5, 69.5) * mm});
            skLineSegment(sketch, "E6.6.0.0", {"start": v(104.5, 1.5) * mm, "end": v(115, 1.5) * mm});
            skPoint(sketch, "E6.6.0.1", {"position": v(103.5, 15.5) * mm});
            skLineSegment(sketch, "E6.6.0.5", {"start": v(103.5, 2.5) * mm, "end": v(103.5, 14.5) * mm});
            skPoint(sketch, "E6.6.0.6", {"position": v(103.5, 1.5) * mm});
            skArc(sketch, "E6.6.0.7", {"start": v(104.5, 15.5) * mm, "mid": v(103.8, 15.2) * mm, "end": v(103.5, 14.5) * mm});
            skLineSegment(sketch, "E6.6.0.8", {"start": v(104.5, 15.5) * mm, "end": v(113.95, 15.5) * mm});
            skArc(sketch, "E6.6.0.11", {"start": v(103.5, 2.5) * mm, "mid": v(103.8, 1.8) * mm, "end": v(104.5, 1.5) * mm});
            skLineSegment(sketch, "E6.6.1.0", {"start": v(104.5, 18.5) * mm, "end": v(113.5, 18.5) * mm});
            skPoint(sketch, "E6.6.1.1", {"position": v(103.5, 32.5) * mm});
            skLineSegment(sketch, "E6.6.1.5", {"start": v(103.5, 19.5) * mm, "end": v(103.5, 31.5) * mm});
            skPoint(sketch, "E6.6.1.6", {"position": v(103.5, 18.5) * mm});
            skArc(sketch, "E6.6.1.7", {"start": v(104.5, 32.5) * mm, "mid": v(103.8, 32.2) * mm, "end": v(103.5, 31.5) * mm});
            skLineSegment(sketch, "E6.6.1.8", {"start": v(104.5, 32.5) * mm, "end": v(110.31, 32.5) * mm});
            skArc(sketch, "E6.6.1.11", {"start": v(103.5, 19.5) * mm, "mid": v(103.8, 18.8) * mm, "end": v(104.5, 18.5) * mm});
            skLineSegment(sketch, "E6.6.2.0", {"start": v(104.5, 35.5) * mm, "end": v(109.38, 35.5) * mm});
            skPoint(sketch, "E6.6.2.1", {"position": v(103.5, 49.5) * mm});
            skLineSegment(sketch, "E6.6.2.5", {"start": v(103.5, 36.5) * mm, "end": v(103.5, 48.5) * mm});
            skPoint(sketch, "E6.6.2.6", {"position": v(103.5, 35.5) * mm});
            skArc(sketch, "E6.6.2.7", {"start": v(103.9, 49.3) * mm, "mid": v(103.6, 48.95) * mm, "end": v(103.5, 48.5) * mm});
            skArc(sketch, "E6.6.2.11", {"start": v(103.5, 36.5) * mm, "mid": v(103.8, 35.8) * mm, "end": v(104.5, 35.5) * mm});
            skLineSegment(sketch, "E6.direction1", {"start": v(1.5, 1.5) * mm, "end": v(18.5, 1.5) * mm, "construction": true});
            skLineSegment(sketch, "E6.direction2", {"start": v(1.5, 1.5) * mm, "end": v(1.5, 18.5) * mm, "construction": true});
            skArc(sketch, "E7.0", {"start": v(113.5, 18.5) * mm, "mid": v(112.13, 25.55) * mm, "end": v(110.31, 32.5) * mm});
            skPoint(sketch, "E8.orphan", {"position": v(104.5, 49.5) * mm});
            skArc(sketch, "E9.trimOffspring", {"start": v(109.38, 35.5) * mm, "mid": v(106.86, 42.49) * mm, "end": v(103.9, 49.3) * mm});
            skArc(sketch, "E10.trimOffspring", {"start": v(100.5, 55.9) * mm, "mid": v(97.3, 61.3) * mm, "end": v(93.82, 66.5) * mm});
            skArc(sketch, "E11.trimOffspring", {"start": v(91.62, 69.5) * mm, "mid": v(89.12, 72.69) * mm, "end": v(86.5, 75.78) * mm});
            skArc(sketch, "E12.trimOffspring", {"start": v(83.5, 79.07) * mm, "mid": v(81.32, 81.32) * mm, "end": v(79.07, 83.5) * mm});
            skArc(sketch, "E13.trimOffspring", {"start": v(75.78, 86.5) * mm, "mid": v(72.69, 89.12) * mm, "end": v(69.5, 91.62) * mm});
            skArc(sketch, "E14.trimOffspring", {"start": v(66.5, 93.82) * mm, "mid": v(61.3, 97.3) * mm, "end": v(55.9, 100.5) * mm});
            skPoint(sketch, "E15.orphan", {"position": v(49.5, 104.5) * mm});
            skArc(sketch, "E16.trimOffspring", {"start": v(49.3, 103.9) * mm, "mid": v(42.49, 106.86) * mm, "end": v(35.5, 109.38) * mm});
            skArc(sketch, "E17.trimOffspring", {"start": v(32.5, 110.31) * mm, "mid": v(25.55, 112.13) * mm, "end": v(18.5, 113.5) * mm});
            skArc(sketch, "E18.trimOffspring", {"start": v(15.5, 113.95) * mm, "mid": v(8.52, 114.68) * mm, "end": v(1.5, 115) * mm});
            skArc(sketch, "E19.trimOffspring", {"start": v(115, 1.5) * mm, "mid": v(114.68, 8.52) * mm, "end": v(113.95, 15.5) * mm});
            skLineSegment(sketch, "E20.MirrorCS", {"start": v(32.5, -104.5) * mm, "end": v(32.5, -110.31) * mm});
            skPoint(sketch, "E21.MirrorP", {"position": v(18.5, -15.5) * mm});
            skPoint(sketch, "E22.MirrorP", {"position": v(35.5, -52.5) * mm});
            skPoint(sketch, "E23.MirrorP", {"position": v(69.5, -32.5) * mm});
            skPoint(sketch, "E24.MirrorP", {"position": v(100.5, -35.5) * mm});
            skLineSegment(sketch, "E25.MirrorCS", {"start": v(2.5, -66.5) * mm, "end": v(14.5, -66.5) * mm});
            skLineSegment(sketch, "E26.MirrorCS", {"start": v(2.5, -86.5) * mm, "end": v(14.5, -86.5) * mm});
            skArc(sketch, "E27.MirrorCS", {"start": v(49.5, -14.5) * mm, "mid": v(49.2, -15.2) * mm, "end": v(48.5, -15.5) * mm});
            skArc(sketch, "E28.MirrorCS", {"start": v(36.5, -32.5) * mm, "mid": v(35.8, -32.2) * mm, "end": v(35.5, -31.5) * mm});
            skPoint(sketch, "E29.MirrorP", {"position": v(18.5, -49.5) * mm});
            skPoint(sketch, "E30.MirrorP", {"position": v(35.5, -86.5) * mm});
            skPoint(sketch, "E31.MirrorP", {"position": v(35.5, -15.5) * mm});
            skLineSegment(sketch, "E32.MirrorCS", {"start": v(2.5, -100.5) * mm, "end": v(14.5, -100.5) * mm});
            skArc(sketch, "E33.MirrorCS", {"start": v(32.5, -14.5) * mm, "mid": v(32.2, -15.2) * mm, "end": v(31.5, -15.5) * mm});
            skArc(sketch, "E34.MirrorCS", {"start": v(1.5, -2.5) * mm, "mid": v(1.8, -1.8) * mm, "end": v(2.5, -1.5) * mm});
            skArc(sketch, "E35.MirrorCS", {"start": v(49.5, -48.5) * mm, "mid": v(49.2, -49.2) * mm, "end": v(48.5, -49.5) * mm});
            skArc(sketch, "E36.MirrorCS", {"start": v(36.5, -66.5) * mm, "mid": v(35.8, -66.2) * mm, "end": v(35.5, -65.5) * mm});
            skPoint(sketch, "E37.MirrorP", {"position": v(18.5, -83.5) * mm});
            skPoint(sketch, "E38.MirrorP", {"position": v(35.5, -49.5) * mm});
            skArc(sketch, "E39.MirrorCS", {"start": v(31.5, -18.5) * mm, "mid": v(32.2, -18.8) * mm, "end": v(32.5, -19.5) * mm});
            skArc(sketch, "E40.MirrorCS", {"start": v(32.5, -48.5) * mm, "mid": v(32.2, -49.2) * mm, "end": v(31.5, -49.5) * mm});
            skArc(sketch, "E41.MirrorCS", {"start": v(49.5, -82.5) * mm, "mid": v(49.2, -83.2) * mm, "end": v(48.5, -83.5) * mm});
            skArc(sketch, "E42.MirrorCS", {"start": v(36.5, -100.5) * mm, "mid": v(35.8, -100.2) * mm, "end": v(35.5, -99.5) * mm});
            skPoint(sketch, "E43.MirrorP", {"position": v(32.5, -15.5) * mm});
            skPoint(sketch, "E44.MirrorP", {"position": v(35.5, -83.5) * mm});
            skArc(sketch, "E45.MirrorCS", {"start": v(31.5, -52.5) * mm, "mid": v(32.2, -52.8) * mm, "end": v(32.5, -53.5) * mm});
            skArc(sketch, "E46.MirrorCS", {"start": v(32.5, -82.5) * mm, "mid": v(32.2, -83.2) * mm, "end": v(31.5, -83.5) * mm});
            skArc(sketch, "E47.MirrorCS", {"start": v(35.5, -104.5) * mm, "mid": v(35.8, -103.8) * mm, "end": v(36.5, -103.5) * mm});
            skArc(sketch, "E48.MirrorCS", {"start": v(65.5, -18.5) * mm, "mid": v(66.2, -18.8) * mm, "end": v(66.5, -19.5) * mm});
            skPoint(sketch, "E49.MirrorP", {"position": v(32.5, -49.5) * mm});
            skArc(sketch, "E50.MirrorCS", {"start": v(14.5, -52.5) * mm, "mid": v(15.2, -52.8) * mm, "end": v(15.5, -53.5) * mm});
            skLineSegment(sketch, "E51.MirrorCS", {"start": v(18.5, -104.5) * mm, "end": v(18.5, -113.5) * mm});
            skArc(sketch, "E52.MirrorCS", {"start": v(65.5, -52.5) * mm, "mid": v(66.2, -52.8) * mm, "end": v(66.5, -53.5) * mm});
            skArc(sketch, "E53.MirrorCS", {"start": v(52.5, -19.5) * mm, "mid": v(52.8, -18.8) * mm, "end": v(53.5, -18.5) * mm});
            skArc(sketch, "E54.MirrorCS", {"start": v(31.5, -86.5) * mm, "mid": v(32.2, -86.8) * mm, "end": v(32.5, -87.5) * mm});
            skPoint(sketch, "E55.MirrorP", {"position": v(32.5, -83.5) * mm});
            skArc(sketch, "E56.MirrorCS", {"start": v(1.5, -53.5) * mm, "mid": v(1.8, -52.8) * mm, "end": v(2.5, -52.5) * mm});
            skArc(sketch, "E57.MirrorCS", {"start": v(14.5, -86.5) * mm, "mid": v(15.2, -86.8) * mm, "end": v(15.5, -87.5) * mm});
            skLineSegment(sketch, "E58.MirrorCS", {"start": v(36.5, -32.5) * mm, "end": v(48.5, -32.5) * mm});
            skArc(sketch, "E59.MirrorCS", {"start": v(65.5, -86.5) * mm, "mid": v(66.2, -86.8) * mm, "end": v(66.5, -87.5) * mm});
            skArc(sketch, "E60.MirrorCS", {"start": v(52.5, -53.5) * mm, "mid": v(52.8, -52.8) * mm, "end": v(53.5, -52.5) * mm});
            skLineSegment(sketch, "E61.MirrorCS", {"start": v(35.5, -2.5) * mm, "end": v(35.5, -14.5) * mm});
            skArc(sketch, "E62.MirrorCS", {"start": v(1.5, -87.5) * mm, "mid": v(1.8, -86.8) * mm, "end": v(2.5, -86.5) * mm});
            skLineSegment(sketch, "E63.MirrorCS", {"start": v(18.5, -2.5) * mm, "end": v(18.5, -14.5) * mm});
            skLineSegment(sketch, "E64.MirrorCS", {"start": v(36.5, -66.5) * mm, "end": v(48.5, -66.5) * mm});
            skLineSegment(sketch, "E65.MirrorCS", {"start": v(83.5, -19.5) * mm, "end": v(83.5, -31.5) * mm});
            skLineSegment(sketch, "E66.MirrorCS", {"start": v(70.5, -1.5) * mm, "end": v(82.5, -1.5) * mm});
            skLineSegment(sketch, "E67.MirrorCS", {"start": v(35.5, -36.5) * mm, "end": v(35.5, -48.5) * mm});
            skArc(sketch, "E68.MirrorCS", {"start": v(14.5, -1.5) * mm, "mid": v(15.2, -1.8) * mm, "end": v(15.5, -2.5) * mm});
            skPoint(sketch, "E69.MirrorP", {"position": v(52.5, -32.5) * mm});
            skPoint(sketch, "E70.MirrorP", {"position": v(69.5, -49.5) * mm});
            skPoint(sketch, "E71.MirrorP", {"position": v(66.5, -86.5) * mm});
            skLineSegment(sketch, "E72.MirrorCS", {"start": v(32.5, -19.5) * mm, "end": v(32.5, -31.5) * mm});
            skLineSegment(sketch, "E73.MirrorCS", {"start": v(18.5, -36.5) * mm, "end": v(18.5, -48.5) * mm});
            skLineSegment(sketch, "E74.MirrorCS", {"start": v(36.5, -100.5) * mm, "end": v(48.5, -100.5) * mm});
            skLineSegment(sketch, "E75.MirrorCS", {"start": v(83.5, -53.5) * mm, "end": v(83.5, -65.5) * mm});
            skLineSegment(sketch, "E76.MirrorCS", {"start": v(70.5, -35.5) * mm, "end": v(82.5, -35.5) * mm});
            skLineSegment(sketch, "E77.MirrorCS", {"start": v(35.5, -70.5) * mm, "end": v(35.5, -82.5) * mm});
            skPoint(sketch, "E78.MirrorP", {"position": v(52.5, -66.5) * mm});
            skPoint(sketch, "E79.MirrorP", {"position": v(69.5, -83.5) * mm});
            skPoint(sketch, "E80.MirrorP", {"position": v(32.5, -1.5) * mm});
            skLineSegment(sketch, "E81.MirrorCS", {"start": v(32.5, -53.5) * mm, "end": v(32.5, -65.5) * mm});
            skLineSegment(sketch, "E82.MirrorCS", {"start": v(18.5, -70.5) * mm, "end": v(18.5, -82.5) * mm});
            skLineSegment(sketch, "E83.MirrorCS", {"start": v(66.5, -19.5) * mm, "end": v(66.5, -31.5) * mm});
            skLineSegment(sketch, "E84.MirrorCS", {"start": v(87.5, -1.5) * mm, "end": v(99.5, -1.5) * mm});
            skLineSegment(sketch, "E85.MirrorCS", {"start": v(70.5, -69.5) * mm, "end": v(82.5, -69.5) * mm});
            skLineSegment(sketch, "E86.MirrorCS", {"start": v(53.5, -1.5) * mm, "end": v(65.5, -1.5) * mm});
            skLineSegment(sketch, "E87.MirrorCS", {"start": v(2.5, -18.5) * mm, "end": v(14.5, -18.5) * mm});
            skPoint(sketch, "E88.MirrorP", {"position": v(52.5, -100.5) * mm});
            skPoint(sketch, "E89.MirrorP", {"position": v(86.5, -32.5) * mm});
            skPoint(sketch, "E90.MirrorP", {"position": v(32.5, -35.5) * mm});
            skPoint(sketch, "E91.MirrorP", {"position": v(35.5, -103.5) * mm});
            skLineSegment(sketch, "E92.MirrorCS", {"start": v(15.5, -53.5) * mm, "end": v(15.5, -65.5) * mm});
            skArc(sketch, "E93.MirrorCS", {"start": v(18.5, -104.5) * mm, "mid": v(18.8, -103.8) * mm, "end": v(19.5, -103.5) * mm});
            skLineSegment(sketch, "E94.MirrorCS", {"start": v(66.5, -53.5) * mm, "end": v(66.5, -65.5) * mm});
            skLineSegment(sketch, "E95.MirrorCS", {"start": v(87.5, -35.5) * mm, "end": v(99.5, -35.5) * mm});
            skLineSegment(sketch, "E96.MirrorCS", {"start": v(87.5, -15.5) * mm, "end": v(99.5, -15.5) * mm});
            skLineSegment(sketch, "E97.MirrorCS", {"start": v(53.5, -35.5) * mm, "end": v(65.5, -35.5) * mm});
            skLineSegment(sketch, "E98.MirrorCS", {"start": v(32.5, -87.5) * mm, "end": v(32.5, -99.5) * mm});
            skPoint(sketch, "E99.MirrorP", {"position": v(1.5, -18.5) * mm});
            skPoint(sketch, "E100.MirrorP", {"position": v(86.5, -66.5) * mm});
            skPoint(sketch, "E101.MirrorP", {"position": v(66.5, -32.5) * mm});
            skPoint(sketch, "E102.MirrorP", {"position": v(32.5, -69.5) * mm});
            skLineSegment(sketch, "E103.MirrorCS", {"start": v(15.5, -87.5) * mm, "end": v(15.5, -99.5) * mm});
            skArc(sketch, "E104.MirrorCS", {"start": v(35.5, -19.5) * mm, "mid": v(35.8, -18.8) * mm, "end": v(36.5, -18.5) * mm});
            skLineSegment(sketch, "E105.MirrorCS", {"start": v(66.5, -87.5) * mm, "end": v(66.5, -93.82) * mm});
            skLineSegment(sketch, "E106.MirrorCS", {"start": v(86.5, -70.5) * mm, "end": v(86.5, -75.78) * mm});
            skLineSegment(sketch, "E107.MirrorCS", {"start": v(87.5, -49.5) * mm, "end": v(99.5, -49.5) * mm});
            skLineSegment(sketch, "E108.MirrorCS", {"start": v(53.5, -69.5) * mm, "end": v(65.5, -69.5) * mm});
            skArc(sketch, "E109.MirrorCS", {"start": v(36.5, -15.5) * mm, "mid": v(35.8, -15.2) * mm, "end": v(35.5, -14.5) * mm});
            skArc(sketch, "E110.MirrorCS", {"start": v(14.5, -18.5) * mm, "mid": v(15.2, -18.8) * mm, "end": v(15.5, -19.5) * mm});
            skPoint(sketch, "E111.MirrorP", {"position": v(1.5, -52.5) * mm});
            skPoint(sketch, "E112.MirrorP", {"position": v(103.5, -49.5) * mm});
            skPoint(sketch, "E113.MirrorP", {"position": v(66.5, -66.5) * mm});
            skArc(sketch, "E114.MirrorCS", {"start": v(19.5, -15.5) * mm, "mid": v(18.8, -15.2) * mm, "end": v(18.5, -14.5) * mm});
            skArc(sketch, "E115.MirrorCS", {"start": v(35.5, -53.5) * mm, "mid": v(35.8, -52.8) * mm, "end": v(36.5, -52.5) * mm});
            skArc(sketch, "E116.MirrorCS", {"start": v(83.5, -31.5) * mm, "mid": v(83.2, -32.2) * mm, "end": v(82.5, -32.5) * mm});
            skLineSegment(sketch, "E117.MirrorCS", {"start": v(1.5, -1.5) * mm, "end": v(18.5, -1.5) * mm, "construction": true});
            skArc(sketch, "E118.MirrorCS", {"start": v(103.5, -2.5) * mm, "mid": v(103.8, -1.8) * mm, "end": v(104.5, -1.5) * mm});
            skArc(sketch, "E119.MirrorCS", {"start": v(82.5, -1.5) * mm, "mid": v(83.2, -1.8) * mm, "end": v(83.5, -2.5) * mm});
            skArc(sketch, "E120.MirrorCS", {"start": v(36.5, -49.5) * mm, "mid": v(35.8, -49.2) * mm, "end": v(35.5, -48.5) * mm});
            skPoint(sketch, "E121.MirrorP", {"position": v(1.5, -86.5) * mm});
            skArc(sketch, "E122.MirrorCS", {"start": v(19.5, -49.5) * mm, "mid": v(18.8, -49.2) * mm, "end": v(18.5, -48.5) * mm});
            skArc(sketch, "E123.MirrorCS", {"start": v(35.5, -87.5) * mm, "mid": v(35.8, -86.8) * mm, "end": v(36.5, -86.5) * mm});
            skArc(sketch, "E124.MirrorCS", {"start": v(83.5, -65.5) * mm, "mid": v(83.2, -66.2) * mm, "end": v(82.5, -66.5) * mm});
            skArc(sketch, "E125.MirrorCS", {"start": v(83.5, -79.07) * mm, "mid": v(81.32, -81.32) * mm, "end": v(79.07, -83.5) * mm});
            skArc(sketch, "E126.MirrorCS", {"start": v(82.5, -35.5) * mm, "mid": v(83.2, -35.8) * mm, "end": v(83.5, -36.5) * mm});
            skArc(sketch, "E127.MirrorCS", {"start": v(36.5, -83.5) * mm, "mid": v(35.8, -83.2) * mm, "end": v(35.5, -82.5) * mm});
            skLineSegment(sketch, "E128.MirrorCS", {"start": v(15.5, -19.5) * mm, "end": v(15.5, -31.5) * mm});
            skArc(sketch, "E129.MirrorCS", {"start": v(19.5, -83.5) * mm, "mid": v(18.8, -83.2) * mm, "end": v(18.5, -82.5) * mm});
            skArc(sketch, "E130.MirrorCS", {"start": v(66.5, -31.5) * mm, "mid": v(66.2, -32.2) * mm, "end": v(65.5, -32.5) * mm});
            skArc(sketch, "E131.MirrorCS", {"start": v(99.5, -1.5) * mm, "mid": v(100.2, -1.8) * mm, "end": v(100.5, -2.5) * mm});
            skArc(sketch, "E132.MirrorCS", {"start": v(82.5, -69.5) * mm, "mid": v(83.2, -69.8) * mm, "end": v(83.5, -70.5) * mm});
            skArc(sketch, "E133.MirrorCS", {"start": v(65.5, -1.5) * mm, "mid": v(66.2, -1.8) * mm, "end": v(66.5, -2.5) * mm});
            skPoint(sketch, "E134.MirrorP", {"position": v(49.5, -103.5) * mm});
            skArc(sketch, "E135.MirrorCS", {"start": v(15.5, -65.5) * mm, "mid": v(15.2, -66.2) * mm, "end": v(14.5, -66.5) * mm});
            skLineSegment(sketch, "E136.MirrorCS", {"start": v(36.5, -1.5) * mm, "end": v(48.5, -1.5) * mm});
            skArc(sketch, "E137.MirrorCS", {"start": v(66.5, -65.5) * mm, "mid": v(66.2, -66.2) * mm, "end": v(65.5, -66.5) * mm});
            skArc(sketch, "E138.MirrorCS", {"start": v(99.5, -35.5) * mm, "mid": v(100.2, -35.8) * mm, "end": v(100.5, -36.5) * mm});
            skArc(sketch, "E139.MirrorCS", {"start": v(86.5, -2.5) * mm, "mid": v(86.8, -1.8) * mm, "end": v(87.5, -1.5) * mm});
            skArc(sketch, "E140.MirrorCS", {"start": v(65.5, -35.5) * mm, "mid": v(66.2, -35.8) * mm, "end": v(66.5, -36.5) * mm});
            skPoint(sketch, "E141.MirrorP", {"position": v(66.5, -18.5) * mm});
            skArc(sketch, "E142.MirrorCS", {"start": v(15.5, -31.5) * mm, "mid": v(15.2, -32.2) * mm, "end": v(14.5, -32.5) * mm});
            skArc(sketch, "E143.MirrorCS", {"start": v(15.5, -99.5) * mm, "mid": v(15.2, -100.2) * mm, "end": v(14.5, -100.5) * mm});
            skLineSegment(sketch, "E144.MirrorCS", {"start": v(36.5, -35.5) * mm, "end": v(48.5, -35.5) * mm});
            skLineSegment(sketch, "E145.MirrorCS", {"start": v(52.5, -87.5) * mm, "end": v(52.5, -99.5) * mm});
            skArc(sketch, "E146.MirrorCS", {"start": v(86.5, -70.5) * mm, "mid": v(86.8, -69.8) * mm, "end": v(87.5, -69.5) * mm});
            skArc(sketch, "E147.MirrorCS", {"start": v(86.5, -36.5) * mm, "mid": v(86.8, -35.8) * mm, "end": v(87.5, -35.5) * mm});
            skArc(sketch, "E148.MirrorCS", {"start": v(65.5, -69.5) * mm, "mid": v(66.2, -69.8) * mm, "end": v(66.5, -70.5) * mm});
            skPoint(sketch, "E149.MirrorP", {"position": v(103.5, -35.5) * mm});
            skPoint(sketch, "E150.MirrorP", {"position": v(35.5, -1.5) * mm});
            skPoint(sketch, "E151.MirrorP", {"position": v(66.5, -52.5) * mm});
            skLineSegment(sketch, "E152.MirrorCS", {"start": v(19.5, -15.5) * mm, "end": v(31.5, -15.5) * mm});
            skLineSegment(sketch, "E153.MirrorCS", {"start": v(36.5, -69.5) * mm, "end": v(48.5, -69.5) * mm});
            skLineSegment(sketch, "E154.MirrorCS", {"start": v(69.5, -19.5) * mm, "end": v(69.5, -31.5) * mm});
            skLineSegment(sketch, "E155.MirrorCS", {"start": v(1.5, -1.5) * mm, "end": v(1.5, -18.5) * mm, "construction": true});
            skLineSegment(sketch, "E156.MirrorCS", {"start": v(2.5, -35.5) * mm, "end": v(14.5, -35.5) * mm});
            skLineSegment(sketch, "E157.MirrorCS", {"start": v(104.5, -18.5) * mm, "end": v(113.5, -18.5) * mm});
            skLineSegment(sketch, "E158.MirrorCS", {"start": v(83.5, -2.5) * mm, "end": v(83.5, -14.5) * mm});
            skPoint(sketch, "E159.MirrorP", {"position": v(35.5, -35.5) * mm});
            skPoint(sketch, "E160.MirrorP", {"position": v(69.5, -15.5) * mm});
            skLineSegment(sketch, "E161.MirrorCS", {"start": v(19.5, -49.5) * mm, "end": v(31.5, -49.5) * mm});
            skLineSegment(sketch, "E162.MirrorCS", {"start": v(36.5, -103.5) * mm, "end": v(48.5, -103.5) * mm});
            skLineSegment(sketch, "E163.MirrorCS", {"start": v(69.5, -53.5) * mm, "end": v(69.5, -65.5) * mm});
            skLineSegment(sketch, "E164.MirrorCS", {"start": v(1.5, -19.5) * mm, "end": v(1.5, -31.5) * mm});
            skLineSegment(sketch, "E165.MirrorCS", {"start": v(2.5, -69.5) * mm, "end": v(14.5, -69.5) * mm});
            skArc(sketch, "E166.MirrorCS", {"start": v(75.78, -86.5) * mm, "mid": v(72.69, -89.12) * mm, "end": v(69.5, -91.62) * mm});
            skLineSegment(sketch, "E167.MirrorCS", {"start": v(83.5, -36.5) * mm, "end": v(83.5, -48.5) * mm});
            skPoint(sketch, "E168.MirrorP", {"position": v(69.5, -69.5) * mm});
            skPoint(sketch, "E169.MirrorP", {"position": v(18.5, -32.5) * mm});
            skPoint(sketch, "E170.MirrorP", {"position": v(35.5, -69.5) * mm});
            skLineSegment(sketch, "E171.MirrorCS", {"start": v(19.5, -83.5) * mm, "end": v(31.5, -83.5) * mm});
            skLineSegment(sketch, "E172.MirrorCS", {"start": v(83.5, -70.5) * mm, "end": v(83.5, -79.07) * mm});
            skLineSegment(sketch, "E173.MirrorCS", {"start": v(100.5, -2.5) * mm, "end": v(100.5, -14.5) * mm});
            skLineSegment(sketch, "E174.MirrorCS", {"start": v(52.5, -19.5) * mm, "end": v(52.5, -31.5) * mm});
            skLineSegment(sketch, "E175.MirrorCS", {"start": v(2.5, -103.5) * mm, "end": v(14.5, -103.5) * mm});
            skPoint(sketch, "E176.MirrorP", {"position": v(18.5, -66.5) * mm});
            skLineSegment(sketch, "E177.MirrorCS", {"start": v(1.5, -53.5) * mm, "end": v(1.5, -65.5) * mm});
            skArc(sketch, "E178.MirrorCS", {"start": v(48.5, -1.5) * mm, "mid": v(49.2, -1.8) * mm, "end": v(49.5, -2.5) * mm});
            skLineSegment(sketch, "E179.MirrorCS", {"start": v(87.5, -18.5) * mm, "end": v(99.5, -18.5) * mm});
            skLineSegment(sketch, "E180.MirrorCS", {"start": v(100.5, -36.5) * mm, "end": v(100.5, -48.5) * mm});
            skLineSegment(sketch, "E181.MirrorCS", {"start": v(52.5, -53.5) * mm, "end": v(52.5, -65.5) * mm});
            skArc(sketch, "E182.MirrorCS", {"start": v(32.5, -31.5) * mm, "mid": v(32.2, -32.2) * mm, "end": v(31.5, -32.5) * mm});
            skPoint(sketch, "E183.MirrorP", {"position": v(15.5, -32.5) * mm});
            skPoint(sketch, "E184.MirrorP", {"position": v(18.5, -100.5) * mm});
            skPoint(sketch, "E185.MirrorP", {"position": v(86.5, -52.5) * mm});
            skLineSegment(sketch, "E186.MirrorCS", {"start": v(1.5, -87.5) * mm, "end": v(1.5, -99.5) * mm});
            skArc(sketch, "E187.MirrorCS", {"start": v(48.5, -35.5) * mm, "mid": v(49.2, -35.8) * mm, "end": v(49.5, -36.5) * mm});
            skLineSegment(sketch, "E188.MirrorCS", {"start": v(87.5, -52.5) * mm, "end": v(99.5, -52.5) * mm});
            skLineSegment(sketch, "E189.MirrorCS", {"start": v(104.5, -1.5) * mm, "end": v(115, -1.5) * mm});
            skArc(sketch, "E190.MirrorCS", {"start": v(53.5, -100.5) * mm, "mid": v(52.8, -100.2) * mm, "end": v(52.5, -99.5) * mm});
            skArc(sketch, "E191.MirrorCS", {"start": v(32.5, -65.5) * mm, "mid": v(32.2, -66.2) * mm, "end": v(31.5, -66.5) * mm});
            skPoint(sketch, "E192.MirrorP", {"position": v(15.5, -66.5) * mm});
            skArc(sketch, "E193.MirrorCS", {"start": v(18.5, -2.5) * mm, "mid": v(18.8, -1.8) * mm, "end": v(19.5, -1.5) * mm});
            skArc(sketch, "E194.MirrorCS", {"start": v(48.5, -69.5) * mm, "mid": v(49.2, -69.8) * mm, "end": v(49.5, -70.5) * mm});
            skLineSegment(sketch, "E195.MirrorCS", {"start": v(103.5, -19.5) * mm, "end": v(103.5, -31.5) * mm});
            skArc(sketch, "E196.MirrorCS", {"start": v(113.5, -18.5) * mm, "mid": v(112.13, -25.55) * mm, "end": v(110.31, -32.5) * mm});
            skArc(sketch, "E197.MirrorCS", {"start": v(70.5, -32.5) * mm, "mid": v(69.8, -32.2) * mm, "end": v(69.5, -31.5) * mm});
            skArc(sketch, "E198.MirrorCS", {"start": v(32.5, -99.5) * mm, "mid": v(32.2, -100.2) * mm, "end": v(31.5, -100.5) * mm});
            skArc(sketch, "E199.MirrorCS", {"start": v(14.5, -35.5) * mm, "mid": v(15.2, -35.8) * mm, "end": v(15.5, -36.5) * mm});
            skPoint(sketch, "E200.MirrorP", {"position": v(69.5, -35.5) * mm});
            skPoint(sketch, "E201.MirrorP", {"position": v(15.5, -100.5) * mm});
            skArc(sketch, "E202.MirrorCS", {"start": v(18.5, -36.5) * mm, "mid": v(18.8, -35.8) * mm, "end": v(19.5, -35.5) * mm});
            skArc(sketch, "E203.MirrorCS", {"start": v(48.5, -103.5) * mm, "mid": v(48.95, -103.6) * mm, "end": v(49.3, -103.9) * mm});
            skArc(sketch, "E204.MirrorCS", {"start": v(66.5, -93.82) * mm, "mid": v(61.3, -97.3) * mm, "end": v(55.9, -100.5) * mm});
            skArc(sketch, "E205.MirrorCS", {"start": v(70.5, -66.5) * mm, "mid": v(69.8, -66.2) * mm, "end": v(69.5, -65.5) * mm});
            skLineSegment(sketch, "E206.MirrorCS", {"start": v(36.5, -15.5) * mm, "end": v(48.5, -15.5) * mm});
            skArc(sketch, "E207.MirrorCS", {"start": v(14.5, -69.5) * mm, "mid": v(15.2, -69.8) * mm, "end": v(15.5, -70.5) * mm});
            skArc(sketch, "E208.MirrorCS", {"start": v(18.5, -70.5) * mm, "mid": v(18.8, -69.8) * mm, "end": v(19.5, -69.5) * mm});
            skArc(sketch, "E209.MirrorCS", {"start": v(53.5, -32.5) * mm, "mid": v(52.8, -32.2) * mm, "end": v(52.5, -31.5) * mm});
            skArc(sketch, "E210.MirrorCS", {"start": v(100.5, -14.5) * mm, "mid": v(100.2, -15.2) * mm, "end": v(99.5, -15.5) * mm});
            skArc(sketch, "E211.MirrorCS", {"start": v(14.5, -103.5) * mm, "mid": v(15.2, -103.8) * mm, "end": v(15.5, -104.5) * mm});
            skLineSegment(sketch, "E212.MirrorCS", {"start": v(36.5, -49.5) * mm, "end": v(48.5, -49.5) * mm});
            skPoint(sketch, "E213.MirrorP", {"position": v(86.5, -18.5) * mm});
            skPoint(sketch, "E214.MirrorP", {"position": v(52.5, -15.5) * mm});
            skLineSegment(sketch, "E215.MirrorCS", {"start": v(49.5, -2.5) * mm, "end": v(49.5, -14.5) * mm});
            skArc(sketch, "E216.MirrorCS", {"start": v(53.5, -66.5) * mm, "mid": v(52.8, -66.2) * mm, "end": v(52.5, -65.5) * mm});
            skArc(sketch, "E217.MirrorCS", {"start": v(100.5, -48.5) * mm, "mid": v(100.2, -49.2) * mm, "end": v(99.5, -49.5) * mm});
            skLineSegment(sketch, "E218.MirrorCS", {"start": v(18.5, -19.5) * mm, "end": v(18.5, -31.5) * mm});
            skLineSegment(sketch, "E219.MirrorCS", {"start": v(36.5, -83.5) * mm, "end": v(48.5, -83.5) * mm});
            skPoint(sketch, "E220.MirrorP", {"position": v(15.5, -18.5) * mm});
            skPoint(sketch, "E221.MirrorP", {"position": v(52.5, -49.5) * mm});
            skLineSegment(sketch, "E222.MirrorCS", {"start": v(49.5, -36.5) * mm, "end": v(49.5, -48.5) * mm});
            skLineSegment(sketch, "E223.MirrorCS", {"start": v(53.5, -100.5) * mm, "end": v(55.9, -100.5) * mm});
            skLineSegment(sketch, "E224.MirrorCS", {"start": v(103.5, -2.5) * mm, "end": v(103.5, -14.5) * mm});
            skLineSegment(sketch, "E225.MirrorCS", {"start": v(18.5, -53.5) * mm, "end": v(18.5, -65.5) * mm});
            skLineSegment(sketch, "E226.MirrorCS", {"start": v(66.5, -2.5) * mm, "end": v(66.5, -14.5) * mm});
            skPoint(sketch, "E227.MirrorP", {"position": v(15.5, -52.5) * mm});
            skPoint(sketch, "E228.MirrorP", {"position": v(49.5, -15.5) * mm});
            skPoint(sketch, "E229.MirrorP", {"position": v(52.5, -83.5) * mm});
            skLineSegment(sketch, "E230.MirrorCS", {"start": v(49.5, -70.5) * mm, "end": v(49.5, -82.5) * mm});
            skLineSegment(sketch, "E231.MirrorCS", {"start": v(70.5, -32.5) * mm, "end": v(82.5, -32.5) * mm});
            skArc(sketch, "E232.MirrorCS", {"start": v(109.38, -35.5) * mm, "mid": v(106.86, -42.49) * mm, "end": v(103.9, -49.3) * mm});
            skLineSegment(sketch, "E233.MirrorCS", {"start": v(18.5, -87.5) * mm, "end": v(18.5, -99.5) * mm});
            skLineSegment(sketch, "E234.MirrorCS", {"start": v(66.5, -36.5) * mm, "end": v(66.5, -48.5) * mm});
            skLineSegment(sketch, "E235.MirrorCS", {"start": v(15.5, -36.5) * mm, "end": v(15.5, -48.5) * mm});
            skPoint(sketch, "E236.MirrorP", {"position": v(15.5, -86.5) * mm});
            skPoint(sketch, "E237.MirrorP", {"position": v(49.5, -49.5) * mm});
            skLineSegment(sketch, "E238.MirrorCS", {"start": v(35.5, -104.5) * mm, "end": v(35.5, -109.38) * mm});
            skLineSegment(sketch, "E239.MirrorCS", {"start": v(70.5, -66.5) * mm, "end": v(82.5, -66.5) * mm});
            skLineSegment(sketch, "E240.MirrorCS", {"start": v(15.5, -70.5) * mm, "end": v(15.5, -82.5) * mm});
            skArc(sketch, "E241.MirrorCS", {"start": v(35.5, -2.5) * mm, "mid": v(35.8, -1.8) * mm, "end": v(36.5, -1.5) * mm});
            skLineSegment(sketch, "E242.MirrorCS", {"start": v(66.5, -70.5) * mm, "end": v(66.5, -82.5) * mm});
            skPoint(sketch, "E243.MirrorP", {"position": v(83.5, -69.5) * mm});
            skPoint(sketch, "E244.MirrorP", {"position": v(49.5, -83.5) * mm});
            skLineSegment(sketch, "E245.MirrorCS", {"start": v(53.5, -32.5) * mm, "end": v(65.5, -32.5) * mm});
            skLineSegment(sketch, "E246.MirrorCS", {"start": v(86.5, -2.5) * mm, "end": v(86.5, -14.5) * mm});
            skLineSegment(sketch, "E247.MirrorCS", {"start": v(15.5, -104.5) * mm, "end": v(15.5, -113.95) * mm});
            skArc(sketch, "E248.MirrorCS", {"start": v(35.5, -36.5) * mm, "mid": v(35.8, -35.8) * mm, "end": v(36.5, -35.5) * mm});
            skArc(sketch, "E249.MirrorCS", {"start": v(83.5, -14.5) * mm, "mid": v(83.2, -15.2) * mm, "end": v(82.5, -15.5) * mm});
            skLineSegment(sketch, "E250.MirrorCS", {"start": v(53.5, -66.5) * mm, "end": v(65.5, -66.5) * mm});
            skLineSegment(sketch, "E251.MirrorCS", {"start": v(86.5, -36.5) * mm, "end": v(86.5, -48.5) * mm});
            skArc(sketch, "E252.MirrorCS", {"start": v(19.5, -32.5) * mm, "mid": v(18.8, -32.2) * mm, "end": v(18.5, -31.5) * mm});
            skArc(sketch, "E253.MirrorCS", {"start": v(35.5, -70.5) * mm, "mid": v(35.8, -69.8) * mm, "end": v(36.5, -69.5) * mm});
            skArc(sketch, "E254.MirrorCS", {"start": v(83.5, -48.5) * mm, "mid": v(83.2, -49.2) * mm, "end": v(82.5, -49.5) * mm});
            skPoint(sketch, "E255.MirrorP", {"position": v(100.5, -52.5) * mm});
            skArc(sketch, "E256.MirrorCS", {"start": v(52.5, -87.5) * mm, "mid": v(52.8, -86.8) * mm, "end": v(53.5, -86.5) * mm});
            skArc(sketch, "E257.MirrorCS", {"start": v(104.5, -15.5) * mm, "mid": v(103.8, -15.2) * mm, "end": v(103.5, -14.5) * mm});
            skArc(sketch, "E258.MirrorCS", {"start": v(19.5, -66.5) * mm, "mid": v(18.8, -66.2) * mm, "end": v(18.5, -65.5) * mm});
            skArc(sketch, "E259.MirrorCS", {"start": v(66.5, -14.5) * mm, "mid": v(66.2, -15.2) * mm, "end": v(65.5, -15.5) * mm});
            skLineSegment(sketch, "E260.MirrorCS", {"start": v(69.5, -70.5) * mm, "end": v(69.5, -82.5) * mm});
            skPoint(sketch, "E261.MirrorP", {"position": v(49.5, -1.5) * mm});
            skArc(sketch, "E262.MirrorCS", {"start": v(69.5, -19.5) * mm, "mid": v(69.8, -18.8) * mm, "end": v(70.5, -18.5) * mm});
            skArc(sketch, "E263.MirrorCS", {"start": v(15.5, -48.5) * mm, "mid": v(15.2, -49.2) * mm, "end": v(14.5, -49.5) * mm});
            skArc(sketch, "E264.MirrorCS", {"start": v(19.5, -100.5) * mm, "mid": v(18.8, -100.2) * mm, "end": v(18.5, -99.5) * mm});
            skArc(sketch, "E265.MirrorCS", {"start": v(100.5, -55.9) * mm, "mid": v(97.3, -61.3) * mm, "end": v(93.82, -66.5) * mm});
            skArc(sketch, "E266.MirrorCS", {"start": v(99.5, -18.5) * mm, "mid": v(100.2, -18.8) * mm, "end": v(100.5, -19.5) * mm});
            skArc(sketch, "E267.MirrorCS", {"start": v(66.5, -48.5) * mm, "mid": v(66.2, -49.2) * mm, "end": v(65.5, -49.5) * mm});
            skPoint(sketch, "E268.MirrorP", {"position": v(49.5, -35.5) * mm});
            skPoint(sketch, "E269.MirrorP", {"position": v(69.5, -1.5) * mm});
            skArc(sketch, "E270.MirrorCS", {"start": v(69.5, -53.5) * mm, "mid": v(69.8, -52.8) * mm, "end": v(70.5, -52.5) * mm});
            skArc(sketch, "E271.MirrorCS", {"start": v(15.5, -82.5) * mm, "mid": v(15.2, -83.2) * mm, "end": v(14.5, -83.5) * mm});
            skLineSegment(sketch, "E272.MirrorCS", {"start": v(36.5, -18.5) * mm, "end": v(48.5, -18.5) * mm});
            skArc(sketch, "E273.MirrorCS", {"start": v(66.5, -82.5) * mm, "mid": v(66.2, -83.2) * mm, "end": v(65.5, -83.5) * mm});
            skArc(sketch, "E274.MirrorCS", {"start": v(99.5, -52.5) * mm, "mid": v(100.2, -52.8) * mm, "end": v(100.5, -53.5) * mm});
            skPoint(sketch, "E275.MirrorP", {"position": v(49.5, -69.5) * mm});
            skArc(sketch, "E276.MirrorCS", {"start": v(87.5, -15.5) * mm, "mid": v(86.8, -15.2) * mm, "end": v(86.5, -14.5) * mm});
            skLineSegment(sketch, "E277.MirrorCS", {"start": v(1.5, -104.5) * mm, "end": v(1.5, -115) * mm});
            skLineSegment(sketch, "E278.MirrorCS", {"start": v(36.5, -52.5) * mm, "end": v(48.5, -52.5) * mm});
            skLineSegment(sketch, "E279.MirrorCS", {"start": v(69.5, -2.5) * mm, "end": v(69.5, -14.5) * mm});
            skArc(sketch, "E280.MirrorCS", {"start": v(104.5, -32.5) * mm, "mid": v(103.8, -32.2) * mm, "end": v(103.5, -31.5) * mm});
            skArc(sketch, "E281.MirrorCS", {"start": v(87.5, -49.5) * mm, "mid": v(86.8, -49.2) * mm, "end": v(86.5, -48.5) * mm});
            skLineSegment(sketch, "E282.MirrorCS", {"start": v(19.5, -32.5) * mm, "end": v(31.5, -32.5) * mm});
            skLineSegment(sketch, "E283.MirrorCS", {"start": v(36.5, -86.5) * mm, "end": v(48.5, -86.5) * mm});
            skLineSegment(sketch, "E284.MirrorCS", {"start": v(69.5, -36.5) * mm, "end": v(69.5, -48.5) * mm});
            skArc(sketch, "E285.MirrorCS", {"start": v(49.3, -103.9) * mm, "mid": v(42.49, -106.86) * mm, "end": v(35.5, -109.38) * mm});
            skLineSegment(sketch, "E286.MirrorCS", {"start": v(104.5, -15.5) * mm, "end": v(113.95, -15.5) * mm});
            skLineSegment(sketch, "E287.MirrorCS", {"start": v(19.5, -66.5) * mm, "end": v(31.5, -66.5) * mm});
            skLineSegment(sketch, "E288.MirrorCS", {"start": v(52.5, -2.5) * mm, "end": v(52.5, -14.5) * mm});
            skArc(sketch, "E289.MirrorCS", {"start": v(70.5, -83.5) * mm, "mid": v(69.8, -83.2) * mm, "end": v(69.5, -82.5) * mm});
            skLineSegment(sketch, "E290.MirrorCS", {"start": v(1.5, -36.5) * mm, "end": v(1.5, -48.5) * mm});
            skLineSegment(sketch, "E291.MirrorCS", {"start": v(19.5, -100.5) * mm, "end": v(31.5, -100.5) * mm});
            skLineSegment(sketch, "E292.MirrorCS", {"start": v(52.5, -36.5) * mm, "end": v(52.5, -48.5) * mm});
            skArc(sketch, "E293.MirrorCS", {"start": v(91.62, -69.5) * mm, "mid": v(89.12, -72.69) * mm, "end": v(86.5, -75.78) * mm});
            skLineSegment(sketch, "E294.MirrorCS", {"start": v(100.5, -19.5) * mm, "end": v(100.5, -31.5) * mm});
            skLineSegment(sketch, "E295.MirrorCS", {"start": v(1.5, -70.5) * mm, "end": v(1.5, -82.5) * mm});
            skArc(sketch, "E296.MirrorCS", {"start": v(48.5, -18.5) * mm, "mid": v(49.2, -18.8) * mm, "end": v(49.5, -19.5) * mm});
            skLineSegment(sketch, "E297.MirrorCS", {"start": v(52.5, -70.5) * mm, "end": v(52.5, -82.5) * mm});
            skLineSegment(sketch, "E298.MirrorCS", {"start": v(100.5, -53.5) * mm, "end": v(100.5, -55.9) * mm});
            skArc(sketch, "E299.MirrorCS", {"start": v(1.5, -104.5) * mm, "mid": v(1.8, -103.8) * mm, "end": v(2.5, -103.5) * mm});
            skArc(sketch, "E300.MirrorCS", {"start": v(48.5, -52.5) * mm, "mid": v(49.2, -52.8) * mm, "end": v(49.5, -53.5) * mm});
            skArc(sketch, "E301.MirrorCS", {"start": v(70.5, -15.5) * mm, "mid": v(69.8, -15.2) * mm, "end": v(69.5, -14.5) * mm});
            skLineSegment(sketch, "E302.MirrorCS", {"start": v(104.5, -32.5) * mm, "end": v(110.31, -32.5) * mm});
            skPoint(sketch, "E303.MirrorP", {"position": v(15.5, -49.5) * mm});
            skPoint(sketch, "E304.MirrorP", {"position": v(83.5, -49.5) * mm});
            skArc(sketch, "E305.MirrorCS", {"start": v(48.5, -86.5) * mm, "mid": v(49.2, -86.8) * mm, "end": v(49.5, -87.5) * mm});
            skArc(sketch, "E306.MirrorCS", {"start": v(70.5, -49.5) * mm, "mid": v(69.8, -49.2) * mm, "end": v(69.5, -48.5) * mm});
            skArc(sketch, "E307.MirrorCS", {"start": v(32.5, -110.31) * mm, "mid": v(25.55, -112.13) * mm, "end": v(18.5, -113.5) * mm});
            skArc(sketch, "E308.MirrorCS", {"start": v(18.5, -19.5) * mm, "mid": v(18.8, -18.8) * mm, "end": v(19.5, -18.5) * mm});
            skPoint(sketch, "E309.MirrorP", {"position": v(15.5, -83.5) * mm});
            skPoint(sketch, "E310.MirrorP", {"position": v(69.5, -52.5) * mm});
            skArc(sketch, "E311.MirrorCS", {"start": v(18.5, -53.5) * mm, "mid": v(18.8, -52.8) * mm, "end": v(19.5, -52.5) * mm});
            skArc(sketch, "E312.MirrorCS", {"start": v(53.5, -15.5) * mm, "mid": v(52.8, -15.2) * mm, "end": v(52.5, -14.5) * mm});
            skLineSegment(sketch, "E313.MirrorCS", {"start": v(70.5, -83.5) * mm, "end": v(79.07, -83.5) * mm});
            skPoint(sketch, "E314.MirrorP", {"position": v(18.5, -18.5) * mm});
            skArc(sketch, "E315.MirrorCS", {"start": v(2.5, -49.5) * mm, "mid": v(1.8, -49.2) * mm, "end": v(1.5, -48.5) * mm});
            skPoint(sketch, "E316.MirrorP", {"position": v(100.5, -32.5) * mm});
            skArc(sketch, "E317.MirrorCS", {"start": v(53.5, -49.5) * mm, "mid": v(52.8, -49.2) * mm, "end": v(52.5, -48.5) * mm});
            skArc(sketch, "E318.MirrorCS", {"start": v(100.5, -31.5) * mm, "mid": v(100.2, -32.2) * mm, "end": v(99.5, -32.5) * mm});
            skArc(sketch, "E319.MirrorCS", {"start": v(18.5, -87.5) * mm, "mid": v(18.8, -86.8) * mm, "end": v(19.5, -86.5) * mm});
            skPoint(sketch, "E320.MirrorP", {"position": v(18.5, -52.5) * mm});
            skPoint(sketch, "E321.MirrorP", {"position": v(86.5, -1.5) * mm});
            skPoint(sketch, "E322.MirrorP", {"position": v(1.5, -15.5) * mm});
            skArc(sketch, "E323.MirrorCS", {"start": v(2.5, -83.5) * mm, "mid": v(1.8, -83.2) * mm, "end": v(1.5, -82.5) * mm});
            skLineSegment(sketch, "E324.MirrorCS", {"start": v(49.5, -19.5) * mm, "end": v(49.5, -31.5) * mm});
            skArc(sketch, "E325.MirrorCS", {"start": v(53.5, -83.5) * mm, "mid": v(52.8, -83.2) * mm, "end": v(52.5, -82.5) * mm});
            skLineSegment(sketch, "E326.MirrorCS", {"start": v(86.5, -53.5) * mm, "end": v(86.5, -65.5) * mm});
            skPoint(sketch, "E327.MirrorP", {"position": v(15.5, -1.5) * mm});
            skPoint(sketch, "E328.MirrorP", {"position": v(18.5, -86.5) * mm});
            skPoint(sketch, "E329.MirrorP", {"position": v(86.5, -35.5) * mm});
            skPoint(sketch, "E330.MirrorP", {"position": v(1.5, -49.5) * mm});
            skLineSegment(sketch, "E331.MirrorCS", {"start": v(19.5, -1.5) * mm, "end": v(31.5, -1.5) * mm});
            skPoint(sketch, "E332.MirrorP", {"position": v(104.5, -49.5) * mm});
            skLineSegment(sketch, "E333.MirrorCS", {"start": v(70.5, -15.5) * mm, "end": v(82.5, -15.5) * mm});
            skArc(sketch, "E334.MirrorCS", {"start": v(103.5, -19.5) * mm, "mid": v(103.8, -18.8) * mm, "end": v(104.5, -18.5) * mm});
            skLineSegment(sketch, "E335.MirrorCS", {"start": v(49.5, -53.5) * mm, "end": v(49.5, -65.5) * mm});
            skPoint(sketch, "E336.MirrorP", {"position": v(18.5, -103.5) * mm});
            skPoint(sketch, "E337.MirrorP", {"position": v(15.5, -35.5) * mm});
            skPoint(sketch, "E338.MirrorP", {"position": v(1.5, -83.5) * mm});
            skArc(sketch, "E339.MirrorCS", {"start": v(2.5, -32.5) * mm, "mid": v(1.8, -32.2) * mm, "end": v(1.5, -31.5) * mm});
            skPoint(sketch, "E340.MirrorP", {"position": v(83.5, -35.5) * mm});
            skLineSegment(sketch, "E341.MirrorCS", {"start": v(49.5, -87.5) * mm, "end": v(49.5, -99.5) * mm});
            skLineSegment(sketch, "E342.MirrorCS", {"start": v(70.5, -49.5) * mm, "end": v(82.5, -49.5) * mm});
            skArc(sketch, "E343.MirrorCS", {"start": v(15.5, -113.95) * mm, "mid": v(8.52, -114.68) * mm, "end": v(1.5, -115) * mm});
            skLineSegment(sketch, "E344.MirrorCS", {"start": v(19.5, -35.5) * mm, "end": v(31.5, -35.5) * mm});
            skPoint(sketch, "E345.MirrorP", {"position": v(49.5, -32.5) * mm});
            skPoint(sketch, "E346.MirrorP", {"position": v(15.5, -69.5) * mm});
            skPoint(sketch, "E347.MirrorP", {"position": v(69.5, -86.5) * mm});
            skLineSegment(sketch, "E348.MirrorCS", {"start": v(53.5, -15.5) * mm, "end": v(65.5, -15.5) * mm});
            skArc(sketch, "E349.MirrorCS", {"start": v(69.5, -70.5) * mm, "mid": v(69.8, -69.8) * mm, "end": v(70.5, -69.5) * mm});
            skLineSegment(sketch, "E350.MirrorCS", {"start": v(19.5, -69.5) * mm, "end": v(31.5, -69.5) * mm});
            skPoint(sketch, "E351.MirrorP", {"position": v(49.5, -66.5) * mm});
            skLineSegment(sketch, "E352.MirrorCS", {"start": v(2.5, -32.5) * mm, "end": v(14.5, -32.5) * mm});
            skLineSegment(sketch, "E353.MirrorCS", {"start": v(2.5, -49.5) * mm, "end": v(14.5, -49.5) * mm});
            skPoint(sketch, "E354.MirrorP", {"position": v(100.5, -18.5) * mm});
            skLineSegment(sketch, "E355.MirrorCS", {"start": v(53.5, -49.5) * mm, "end": v(65.5, -49.5) * mm});
            skLineSegment(sketch, "E356.MirrorCS", {"start": v(86.5, -19.5) * mm, "end": v(86.5, -31.5) * mm});
            skLineSegment(sketch, "E357.MirrorCS", {"start": v(19.5, -103.5) * mm, "end": v(31.5, -103.5) * mm});
            skPoint(sketch, "E358.MirrorP", {"position": v(49.5, -100.5) * mm});
            skPoint(sketch, "E359.MirrorP", {"position": v(52.5, -1.5) * mm});
            skLineSegment(sketch, "E360.MirrorCS", {"start": v(2.5, -83.5) * mm, "end": v(14.5, -83.5) * mm});
            skPoint(sketch, "E361.MirrorP", {"position": v(86.5, -69.5) * mm});
            skLineSegment(sketch, "E362.MirrorCS", {"start": v(53.5, -83.5) * mm, "end": v(65.5, -83.5) * mm});
            skArc(sketch, "E363.MirrorCS", {"start": v(87.5, -66.5) * mm, "mid": v(86.8, -66.2) * mm, "end": v(86.5, -65.5) * mm});
            skArc(sketch, "E364.MirrorCS", {"start": v(49.5, -31.5) * mm, "mid": v(49.2, -32.2) * mm, "end": v(48.5, -32.5) * mm});
            skPoint(sketch, "E365.MirrorP", {"position": v(52.5, -35.5) * mm});
            skArc(sketch, "E366.MirrorCS", {"start": v(1.5, -19.5) * mm, "mid": v(1.8, -18.8) * mm, "end": v(2.5, -18.5) * mm});
            skPoint(sketch, "E367.MirrorP", {"position": v(103.5, -32.5) * mm});
            skArc(sketch, "E368.MirrorCS", {"start": v(49.5, -65.5) * mm, "mid": v(49.2, -66.2) * mm, "end": v(48.5, -66.5) * mm});
            skPoint(sketch, "E369.MirrorP", {"position": v(35.5, -32.5) * mm});
            skLineSegment(sketch, "E370.MirrorCS", {"start": v(104.5, -35.5) * mm, "end": v(109.38, -35.5) * mm});
            skArc(sketch, "E371.MirrorCS", {"start": v(69.5, -2.5) * mm, "mid": v(69.8, -1.8) * mm, "end": v(70.5, -1.5) * mm});
            skArc(sketch, "E372.MirrorCS", {"start": v(31.5, -1.5) * mm, "mid": v(32.2, -1.8) * mm, "end": v(32.5, -2.5) * mm});
            skPoint(sketch, "E373.MirrorP", {"position": v(32.5, -103.5) * mm});
            skPoint(sketch, "E374.MirrorP", {"position": v(52.5, -69.5) * mm});
            skPoint(sketch, "E375.MirrorP", {"position": v(49.5, -104.5) * mm});
            skPoint(sketch, "E376.MirrorP", {"position": v(1.5, -103.5) * mm});
            skPoint(sketch, "E377.MirrorP", {"position": v(35.5, -66.5) * mm});
            skArc(sketch, "E378.MirrorCS", {"start": v(115, -1.5) * mm, "mid": v(114.68, -8.52) * mm, "end": v(113.95, -15.5) * mm});
            skArc(sketch, "E379.MirrorCS", {"start": v(69.5, -36.5) * mm, "mid": v(69.8, -35.8) * mm, "end": v(70.5, -35.5) * mm});
            skArc(sketch, "E380.MirrorCS", {"start": v(49.5, -99.5) * mm, "mid": v(49.2, -100.2) * mm, "end": v(48.5, -100.5) * mm});
            skArc(sketch, "E381.MirrorCS", {"start": v(31.5, -35.5) * mm, "mid": v(32.2, -35.8) * mm, "end": v(32.5, -36.5) * mm});
            skPoint(sketch, "E382.MirrorP", {"position": v(49.5, -18.5) * mm});
            skPoint(sketch, "E383.MirrorP", {"position": v(83.5, -15.5) * mm});
            skPoint(sketch, "E384.MirrorP", {"position": v(83.5, -66.5) * mm});
            skArc(sketch, "E385.MirrorCS", {"start": v(31.5, -69.5) * mm, "mid": v(32.2, -69.8) * mm, "end": v(32.5, -70.5) * mm});
            skPoint(sketch, "E386.MirrorP", {"position": v(32.5, -32.5) * mm});
            skPoint(sketch, "E387.MirrorP", {"position": v(35.5, -100.5) * mm});
            skLineSegment(sketch, "E388.MirrorCS", {"start": v(70.5, -86.5) * mm, "end": v(75.78, -86.5) * mm});
            skArc(sketch, "E389.MirrorCS", {"start": v(52.5, -2.5) * mm, "mid": v(52.8, -1.8) * mm, "end": v(53.5, -1.5) * mm});
            skPoint(sketch, "E390.MirrorP", {"position": v(69.5, -18.5) * mm});
            skPoint(sketch, "E391.MirrorP", {"position": v(49.5, -52.5) * mm});
            skPoint(sketch, "E392.MirrorP", {"position": v(18.5, -1.5) * mm});
            skPoint(sketch, "E393.MirrorP", {"position": v(100.5, -15.5) * mm});
            skPoint(sketch, "E394.MirrorP", {"position": v(15.5, -15.5) * mm});
            skPoint(sketch, "E395.MirrorP", {"position": v(32.5, -66.5) * mm});
            skArc(sketch, "E396.MirrorCS", {"start": v(87.5, -32.5) * mm, "mid": v(86.8, -32.2) * mm, "end": v(86.5, -31.5) * mm});
            skArc(sketch, "E397.MirrorCS", {"start": v(52.5, -36.5) * mm, "mid": v(52.8, -35.8) * mm, "end": v(53.5, -35.5) * mm});
            skArc(sketch, "E398.MirrorCS", {"start": v(31.5, -103.5) * mm, "mid": v(32.2, -103.8) * mm, "end": v(32.5, -104.5) * mm});
            skPoint(sketch, "E399.MirrorP", {"position": v(49.5, -86.5) * mm});
            skPoint(sketch, "E400.MirrorP", {"position": v(18.5, -35.5) * mm});
            skPoint(sketch, "E401.MirrorP", {"position": v(100.5, -49.5) * mm});
            skLineSegment(sketch, "E402.MirrorCS", {"start": v(35.5, -19.5) * mm, "end": v(35.5, -31.5) * mm});
            skPoint(sketch, "E403.MirrorP", {"position": v(32.5, -100.5) * mm});
            skLineSegment(sketch, "E404.MirrorCS", {"start": v(87.5, -66.5) * mm, "end": v(93.82, -66.5) * mm});
            skArc(sketch, "E405.MirrorCS", {"start": v(52.5, -70.5) * mm, "mid": v(52.8, -69.8) * mm, "end": v(53.5, -69.5) * mm});
            skPoint(sketch, "E406.MirrorP", {"position": v(18.5, -69.5) * mm});
            skLineSegment(sketch, "E407.MirrorCS", {"start": v(2.5, -1.5) * mm, "end": v(14.5, -1.5) * mm});
            skPoint(sketch, "E408.MirrorP", {"position": v(103.5, -18.5) * mm});
            skLineSegment(sketch, "E409.MirrorCS", {"start": v(35.5, -53.5) * mm, "end": v(35.5, -65.5) * mm});
            skLineSegment(sketch, "E410.MirrorCS", {"start": v(70.5, -18.5) * mm, "end": v(82.5, -18.5) * mm});
            skLineSegment(sketch, "E411.MirrorCS", {"start": v(103.5, -36.5) * mm, "end": v(103.5, -48.5) * mm});
            skPoint(sketch, "E412.MirrorP", {"position": v(69.5, -66.5) * mm});
            skPoint(sketch, "E413.MirrorP", {"position": v(15.5, -103.5) * mm});
            skLineSegment(sketch, "E414.MirrorCS", {"start": v(70.5, -52.5) * mm, "end": v(82.5, -52.5) * mm});
            skPoint(sketch, "E415.MirrorP", {"position": v(83.5, -1.5) * mm});
            skLineSegment(sketch, "E416.MirrorCS", {"start": v(35.5, -87.5) * mm, "end": v(35.5, -99.5) * mm});
            skPoint(sketch, "E417.MirrorP", {"position": v(52.5, -86.5) * mm});
            skLineSegment(sketch, "E418.MirrorCS", {"start": v(2.5, -15.5) * mm, "end": v(14.5, -15.5) * mm});
            skPoint(sketch, "E419.MirrorP", {"position": v(86.5, -15.5) * mm});
            skPoint(sketch, "E420.MirrorP", {"position": v(32.5, -18.5) * mm});
            skLineSegment(sketch, "E421.MirrorCS", {"start": v(69.5, -87.5) * mm, "end": v(69.5, -91.62) * mm});
            skLineSegment(sketch, "E422.MirrorCS", {"start": v(53.5, -18.5) * mm, "end": v(65.5, -18.5) * mm});
            skPoint(sketch, "E423.MirrorP", {"position": v(86.5, -49.5) * mm});
            skPoint(sketch, "E424.MirrorP", {"position": v(32.5, -52.5) * mm});
            skPoint(sketch, "E425.MirrorP", {"position": v(66.5, -15.5) * mm});
            skLineSegment(sketch, "E426.MirrorCS", {"start": v(87.5, -32.5) * mm, "end": v(99.5, -32.5) * mm});
            skLineSegment(sketch, "E427.MirrorCS", {"start": v(53.5, -52.5) * mm, "end": v(65.5, -52.5) * mm});
            skLineSegment(sketch, "E428.MirrorCS", {"start": v(1.5, -2.5) * mm, "end": v(1.5, -14.5) * mm});
            skPoint(sketch, "E429.MirrorP", {"position": v(1.5, -35.5) * mm});
            skPoint(sketch, "E430.MirrorP", {"position": v(32.5, -86.5) * mm});
            skPoint(sketch, "E431.MirrorP", {"position": v(66.5, -49.5) * mm});
            skArc(sketch, "E432.MirrorCS", {"start": v(86.5, -53.5) * mm, "mid": v(86.8, -52.8) * mm, "end": v(87.5, -52.5) * mm});
            skPoint(sketch, "E433.MirrorP", {"position": v(103.5, -15.5) * mm});
            skLineSegment(sketch, "E434.MirrorCS", {"start": v(53.5, -86.5) * mm, "end": v(65.5, -86.5) * mm});
            skPoint(sketch, "E435.MirrorP", {"position": v(52.5, -18.5) * mm});
            skPoint(sketch, "E436.MirrorP", {"position": v(1.5, -69.5) * mm});
            skArc(sketch, "E437.MirrorCS", {"start": v(82.5, -18.5) * mm, "mid": v(83.2, -18.8) * mm, "end": v(83.5, -19.5) * mm});
            skPoint(sketch, "E438.MirrorP", {"position": v(66.5, -83.5) * mm});
            skArc(sketch, "E439.MirrorCS", {"start": v(103.9, -49.3) * mm, "mid": v(103.6, -48.95) * mm, "end": v(103.5, -48.5) * mm});
            skPoint(sketch, "E440.MirrorP", {"position": v(52.5, -52.5) * mm});
            skArc(sketch, "E441.MirrorCS", {"start": v(1.5, -36.5) * mm, "mid": v(1.8, -35.8) * mm, "end": v(2.5, -35.5) * mm});
            skLineSegment(sketch, "E442.MirrorCS", {"start": v(15.5, -2.5) * mm, "end": v(15.5, -14.5) * mm});
            skArc(sketch, "E443.MirrorCS", {"start": v(82.5, -52.5) * mm, "mid": v(83.2, -52.8) * mm, "end": v(83.5, -53.5) * mm});
            skPoint(sketch, "E444.MirrorP", {"position": v(1.5, -32.5) * mm});
            skArc(sketch, "E445.MirrorCS", {"start": v(2.5, -66.5) * mm, "mid": v(1.8, -66.2) * mm, "end": v(1.5, -65.5) * mm});
            skArc(sketch, "E446.MirrorCS", {"start": v(1.5, -70.5) * mm, "mid": v(1.8, -69.8) * mm, "end": v(2.5, -69.5) * mm});
            skArc(sketch, "E447.MirrorCS", {"start": v(69.5, -87.5) * mm, "mid": v(69.8, -86.8) * mm, "end": v(70.5, -86.5) * mm});
            skPoint(sketch, "E448.MirrorP", {"position": v(83.5, -32.5) * mm});
            skPoint(sketch, "E449.MirrorP", {"position": v(1.5, -66.5) * mm});
            skArc(sketch, "E450.MirrorCS", {"start": v(2.5, -100.5) * mm, "mid": v(1.8, -100.2) * mm, "end": v(1.5, -99.5) * mm});
            skLineSegment(sketch, "E451.MirrorCS", {"start": v(32.5, -2.5) * mm, "end": v(32.5, -14.5) * mm});
            skPoint(sketch, "E452.MirrorP", {"position": v(1.5, -1.5) * mm});
            skPoint(sketch, "E453.MirrorP", {"position": v(66.5, -1.5) * mm});
            skArc(sketch, "E454.MirrorCS", {"start": v(2.5, -15.5) * mm, "mid": v(1.8, -15.2) * mm, "end": v(1.5, -14.5) * mm});
            skPoint(sketch, "E455.MirrorP", {"position": v(1.5, -100.5) * mm});
            skArc(sketch, "E456.MirrorCS", {"start": v(86.5, -19.5) * mm, "mid": v(86.8, -18.8) * mm, "end": v(87.5, -18.5) * mm});
            skPoint(sketch, "E457.MirrorP", {"position": v(83.5, -18.5) * mm});
            skLineSegment(sketch, "E458.MirrorCS", {"start": v(19.5, -18.5) * mm, "end": v(31.5, -18.5) * mm});
            skLineSegment(sketch, "E459.MirrorCS", {"start": v(32.5, -36.5) * mm, "end": v(32.5, -48.5) * mm});
            skPoint(sketch, "E460.MirrorP", {"position": v(103.5, -1.5) * mm});
            skPoint(sketch, "E461.MirrorP", {"position": v(66.5, -35.5) * mm});
            skLineSegment(sketch, "E462.MirrorCS", {"start": v(87.5, -69.5) * mm, "end": v(91.62, -69.5) * mm});
            skPoint(sketch, "E463.MirrorP", {"position": v(83.5, -52.5) * mm});
            skLineSegment(sketch, "E464.MirrorCS", {"start": v(19.5, -52.5) * mm, "end": v(31.5, -52.5) * mm});
            skLineSegment(sketch, "E465.MirrorCS", {"start": v(32.5, -70.5) * mm, "end": v(32.5, -82.5) * mm});
            skPoint(sketch, "E466.MirrorP", {"position": v(35.5, -18.5) * mm});
            skPoint(sketch, "E467.MirrorP", {"position": v(66.5, -69.5) * mm});
            skArc(sketch, "E468.MirrorCS", {"start": v(103.5, -36.5) * mm, "mid": v(103.8, -35.8) * mm, "end": v(104.5, -35.5) * mm});
            skPoint(sketch, "E469.MirrorP", {"position": v(100.5, -1.5) * mm});
            skArc(sketch, "E470.MirrorCS", {"start": v(15.5, -14.5) * mm, "mid": v(15.2, -15.2) * mm, "end": v(14.5, -15.5) * mm});
            skLineSegment(sketch, "E471.MirrorCS", {"start": v(2.5, -52.5) * mm, "end": v(14.5, -52.5) * mm});
            skLineSegment(sketch, "E472.MirrorCS", {"start": v(19.5, -86.5) * mm, "end": v(31.5, -86.5) * mm});
            skLineSegment(sketch, "E473.MirrorCS", {"start": v(-70.5, 69.5) * mm, "end": v(-82.5, 69.5) * mm});
            skArc(sketch, "E474.MirrorCS", {"start": v(-53.5, 49.5) * mm, "mid": v(-52.8, 49.2) * mm, "end": v(-52.5, 48.5) * mm});
            skLineSegment(sketch, "E475.MirrorCS", {"start": v(-104.5, 1.5) * mm, "end": v(-115, 1.5) * mm});
            skLineSegment(sketch, "E476.MirrorCS", {"start": v(-87.5, 15.5) * mm, "end": v(-99.5, 15.5) * mm});
            skArc(sketch, "E477.MirrorCS", {"start": v(-53.5, 83.5) * mm, "mid": v(-52.8, 83.2) * mm, "end": v(-52.5, 82.5) * mm});
            skArc(sketch, "E478.MirrorCS", {"start": v(-113.5, 18.5) * mm, "mid": v(-112.13, 25.55) * mm, "end": v(-110.31, 32.5) * mm});
            skLineSegment(sketch, "E479.MirrorCS", {"start": v(-87.5, 49.5) * mm, "end": v(-99.5, 49.5) * mm});
            skLineSegment(sketch, "E480.MirrorCS", {"start": v(-70.5, 15.5) * mm, "end": v(-82.5, 15.5) * mm});
            skLineSegment(sketch, "E481.MirrorCS", {"start": v(-2.5, -100.5) * mm, "end": v(-14.5, -100.5) * mm});
            skArc(sketch, "E482.MirrorCS", {"start": v(-103.5, 2.5) * mm, "mid": v(-103.8, 1.8) * mm, "end": v(-104.5, 1.5) * mm});
            skLineSegment(sketch, "E483.MirrorCS", {"start": v(-70.5, 49.5) * mm, "end": v(-82.5, 49.5) * mm});
            skArc(sketch, "E484.MirrorCS", {"start": v(-52.5, -19.5) * mm, "mid": v(-52.8, -18.8) * mm, "end": v(-53.5, -18.5) * mm});
            skArc(sketch, "E485.MirrorCS", {"start": v(-83.5, 79.07) * mm, "mid": v(-81.32, 81.32) * mm, "end": v(-79.07, 83.5) * mm});
            skPoint(sketch, "E486.MirrorP", {"position": v(-15.5, 15.5) * mm});
            skArc(sketch, "E487.MirrorCS", {"start": v(-69.5, 70.5) * mm, "mid": v(-69.8, 69.8) * mm, "end": v(-70.5, 69.5) * mm});
            skLineSegment(sketch, "E488.MirrorCS", {"start": v(-18.5, -36.5) * mm, "end": v(-18.5, -48.5) * mm});
            skArc(sketch, "E489.MirrorCS", {"start": v(-36.5, -66.5) * mm, "mid": v(-35.8, -66.2) * mm, "end": v(-35.5, -65.5) * mm});
            skLineSegment(sketch, "E490.MirrorCS", {"start": v(-86.5, 19.5) * mm, "end": v(-86.5, 31.5) * mm});
            skLineSegment(sketch, "E491.MirrorCS", {"start": v(-87.5, -15.5) * mm, "end": v(-99.5, -15.5) * mm});
            skLineSegment(sketch, "E492.MirrorCS", {"start": v(-36.5, -32.5) * mm, "end": v(-48.5, -32.5) * mm});
            skPoint(sketch, "E493.MirrorP", {"position": v(-18.5, 103.5) * mm});
            skArc(sketch, "E494.MirrorCS", {"start": v(-87.5, 66.5) * mm, "mid": v(-86.8, 66.2) * mm, "end": v(-86.5, 65.5) * mm});
            skPoint(sketch, "E495.MirrorP", {"position": v(-86.5, 35.5) * mm});
            skPoint(sketch, "E496.MirrorP", {"position": v(-66.5, -52.5) * mm});
            skArc(sketch, "E497.MirrorCS", {"start": v(-82.5, -1.5) * mm, "mid": v(-83.2, -1.8) * mm, "end": v(-83.5, -2.5) * mm});
            skLineSegment(sketch, "E498.MirrorCS", {"start": v(-35.5, -70.5) * mm, "end": v(-35.5, -82.5) * mm});
            skLineSegment(sketch, "E499.MirrorCS", {"start": v(-104.5, 35.5) * mm, "end": v(-109.38, 35.5) * mm});
            skArc(sketch, "E500.MirrorCS", {"start": v(-66.5, -65.5) * mm, "mid": v(-66.2, -66.2) * mm, "end": v(-65.5, -66.5) * mm});
            skArc(sketch, "E501.MirrorCS", {"start": v(-35.5, -19.5) * mm, "mid": v(-35.8, -18.8) * mm, "end": v(-36.5, -18.5) * mm});
            skPoint(sketch, "E502.MirrorP", {"position": v(-35.5, 49.5) * mm});
            skArc(sketch, "E503.MirrorCS", {"start": v(-115, 1.5) * mm, "mid": v(-114.68, 8.52) * mm, "end": v(-113.95, 15.5) * mm});
            skPoint(sketch, "E504.MirrorP", {"position": v(-15.5, -32.5) * mm});
            skPoint(sketch, "E505.MirrorP", {"position": v(-35.5, -66.5) * mm});
            skLineSegment(sketch, "E506.MirrorCS", {"start": v(-104.5, -18.5) * mm, "end": v(-113.5, -18.5) * mm});
            skPoint(sketch, "E507.MirrorP", {"position": v(-32.5, -32.5) * mm});
            skArc(sketch, "E508.MirrorCS", {"start": v(-83.5, -65.5) * mm, "mid": v(-83.2, -66.2) * mm, "end": v(-82.5, -66.5) * mm});
            skArc(sketch, "E509.MirrorCS", {"start": v(-32.5, -82.5) * mm, "mid": v(-32.2, -83.2) * mm, "end": v(-31.5, -83.5) * mm});
            skArc(sketch, "E510.MirrorCS", {"start": v(-15.5, -31.5) * mm, "mid": v(-15.2, -32.2) * mm, "end": v(-14.5, -32.5) * mm});
            skLineSegment(sketch, "E511.MirrorCS", {"start": v(-36.5, -66.5) * mm, "end": v(-48.5, -66.5) * mm});
            skPoint(sketch, "E512.MirrorP", {"position": v(-69.5, -86.5) * mm});
            skLineSegment(sketch, "E513.MirrorCS", {"start": v(-69.5, -53.5) * mm, "end": v(-69.5, -65.5) * mm});
            skLineSegment(sketch, "E514.MirrorCS", {"start": v(-53.5, -1.5) * mm, "end": v(-65.5, -1.5) * mm});
            skArc(sketch, "E515.MirrorCS", {"start": v(-14.5, -18.5) * mm, "mid": v(-15.2, -18.8) * mm, "end": v(-15.5, -19.5) * mm});
            skArc(sketch, "E516.MirrorCS", {"start": v(-66.5, -31.5) * mm, "mid": v(-66.2, -32.2) * mm, "end": v(-65.5, -32.5) * mm});
            skArc(sketch, "E517.MirrorCS", {"start": v(-65.5, -69.5) * mm, "mid": v(-66.2, -69.8) * mm, "end": v(-66.5, -70.5) * mm});
            skPoint(sketch, "E518.MirrorP", {"position": v(-1.5, 103.5) * mm});
            skPoint(sketch, "E519.MirrorP", {"position": v(-66.5, 49.5) * mm});
            skPoint(sketch, "E520.MirrorP", {"position": v(-69.5, -49.5) * mm});
            skLineSegment(sketch, "E521.MirrorCS", {"start": v(-87.5, -18.5) * mm, "end": v(-99.5, -18.5) * mm});
            skPoint(sketch, "E522.MirrorP", {"position": v(-35.5, -18.5) * mm});
            skArc(sketch, "E523.MirrorCS", {"start": v(-14.5, -35.5) * mm, "mid": v(-15.2, -35.8) * mm, "end": v(-15.5, -36.5) * mm});
            skPoint(sketch, "E524.MirrorP", {"position": v(-83.5, -69.5) * mm});
            skPoint(sketch, "E525.MirrorP", {"position": v(-1.5, -35.5) * mm});
            skLineSegment(sketch, "E526.MirrorCS", {"start": v(-36.5, -83.5) * mm, "end": v(-48.5, -83.5) * mm});
            skLineSegment(sketch, "E527.MirrorCS", {"start": v(-1.5, -87.5) * mm, "end": v(-1.5, -99.5) * mm});
            skPoint(sketch, "E528.MirrorP", {"position": v(-15.5, 52.5) * mm});
            skLineSegment(sketch, "E529.MirrorCS", {"start": v(-66.5, -70.5) * mm, "end": v(-66.5, -82.5) * mm});
            skPoint(sketch, "E530.MirrorP", {"position": v(-32.5, -15.5) * mm});
            skArc(sketch, "E531.MirrorCS", {"start": v(-70.5, -66.5) * mm, "mid": v(-69.8, -66.2) * mm, "end": v(-69.5, -65.5) * mm});
            skPoint(sketch, "E532.MirrorP", {"position": v(-52.5, -52.5) * mm});
            skPoint(sketch, "E533.MirrorP", {"position": v(-52.5, 18.5) * mm});
            skPoint(sketch, "E534.MirrorP", {"position": v(-49.5, -35.5) * mm});
            skArc(sketch, "E535.MirrorCS", {"start": v(-69.5, -19.5) * mm, "mid": v(-69.8, -18.8) * mm, "end": v(-70.5, -18.5) * mm});
            skLineSegment(sketch, "E536.MirrorCS", {"start": v(-18.5, -53.5) * mm, "end": v(-18.5, -65.5) * mm});
            skArc(sketch, "E537.MirrorCS", {"start": v(-87.5, -49.5) * mm, "mid": v(-86.8, -49.2) * mm, "end": v(-86.5, -48.5) * mm});
            skLineSegment(sketch, "E538.MirrorCS", {"start": v(-2.5, 52.5) * mm, "end": v(-14.5, 52.5) * mm});
            skArc(sketch, "E539.MirrorCS", {"start": v(-35.5, -36.5) * mm, "mid": v(-35.8, -35.8) * mm, "end": v(-36.5, -35.5) * mm});
            skPoint(sketch, "E540.MirrorP", {"position": v(-103.5, -18.5) * mm});
            skLineSegment(sketch, "E541.MirrorCS", {"start": v(-83.5, -70.5) * mm, "end": v(-83.5, -79.07) * mm});
            skLineSegment(sketch, "E542.MirrorCS", {"start": v(-52.5, -70.5) * mm, "end": v(-52.5, -82.5) * mm});
            skLineSegment(sketch, "E543.MirrorCS", {"start": v(-2.5, 86.5) * mm, "end": v(-14.5, 86.5) * mm});
            skArc(sketch, "E544.MirrorCS", {"start": v(-99.5, -18.5) * mm, "mid": v(-100.2, -18.8) * mm, "end": v(-100.5, -19.5) * mm});
            skArc(sketch, "E545.MirrorCS", {"start": v(-18.5, -2.5) * mm, "mid": v(-18.8, -1.8) * mm, "end": v(-19.5, -1.5) * mm});
            skArc(sketch, "E546.MirrorCS", {"start": v(-18.5, -87.5) * mm, "mid": v(-18.8, -86.8) * mm, "end": v(-19.5, -86.5) * mm});
            skArc(sketch, "E547.MirrorCS", {"start": v(-32.5, 14.5) * mm, "mid": v(-32.2, 15.2) * mm, "end": v(-31.5, 15.5) * mm});
            skArc(sketch, "E548.MirrorCS", {"start": v(-49.3, -103.9) * mm, "mid": v(-42.49, -106.86) * mm, "end": v(-35.5, -109.38) * mm});
            skArc(sketch, "E549.MirrorCS", {"start": v(-14.5, -103.5) * mm, "mid": v(-15.2, -103.8) * mm, "end": v(-15.5, -104.5) * mm});
            skLineSegment(sketch, "E550.MirrorCS", {"start": v(-19.5, -69.5) * mm, "end": v(-31.5, -69.5) * mm});
            skArc(sketch, "E551.MirrorCS", {"start": v(-32.5, 48.5) * mm, "mid": v(-32.2, 49.2) * mm, "end": v(-31.5, 49.5) * mm});
            skArc(sketch, "E552.MirrorCS", {"start": v(-70.5, -15.5) * mm, "mid": v(-69.8, -15.2) * mm, "end": v(-69.5, -14.5) * mm});
            skLineSegment(sketch, "E553.MirrorCS", {"start": v(-66.5, -36.5) * mm, "end": v(-66.5, -48.5) * mm});
            skArc(sketch, "E554.MirrorCS", {"start": v(-69.5, -36.5) * mm, "mid": v(-69.8, -35.8) * mm, "end": v(-70.5, -35.5) * mm});
            skArc(sketch, "E555.MirrorCS", {"start": v(-32.5, 82.5) * mm, "mid": v(-32.2, 83.2) * mm, "end": v(-31.5, 83.5) * mm});
            skLineSegment(sketch, "E556.MirrorCS", {"start": v(-86.5, -53.5) * mm, "end": v(-86.5, -65.5) * mm});
            skArc(sketch, "E557.MirrorCS", {"start": v(-83.5, -48.5) * mm, "mid": v(-83.2, -49.2) * mm, "end": v(-82.5, -49.5) * mm});
            skLineSegment(sketch, "E558.MirrorCS", {"start": v(-70.5, -52.5) * mm, "end": v(-82.5, -52.5) * mm});
            skLineSegment(sketch, "E559.MirrorCS", {"start": v(-18.5, 104.5) * mm, "end": v(-18.5, 113.5) * mm});
            skLineSegment(sketch, "E560.MirrorCS", {"start": v(-86.5, -19.5) * mm, "end": v(-86.5, -31.5) * mm});
            skPoint(sketch, "E561.MirrorP", {"position": v(-100.5, 18.5) * mm});
            skPoint(sketch, "E562.MirrorP", {"position": v(-52.5, -1.5) * mm});
            skArc(sketch, "E563.MirrorCS", {"start": v(-99.5, -52.5) * mm, "mid": v(-100.2, -52.8) * mm, "end": v(-100.5, -53.5) * mm});
            skLineSegment(sketch, "E564.MirrorCS", {"start": v(-15.5, 36.5) * mm, "end": v(-15.5, 48.5) * mm});
            skArc(sketch, "E565.MirrorCS", {"start": v(-1.5, -70.5) * mm, "mid": v(-1.8, -69.8) * mm, "end": v(-2.5, -69.5) * mm});
            skLineSegment(sketch, "E566.MirrorCS", {"start": v(-36.5, 32.5) * mm, "end": v(-48.5, 32.5) * mm});
            skLineSegment(sketch, "E567.MirrorCS", {"start": v(-70.5, -86.5) * mm, "end": v(-75.78, -86.5) * mm});
            skLineSegment(sketch, "E568.MirrorCS", {"start": v(-19.5, -100.5) * mm, "end": v(-31.5, -100.5) * mm});
            skLineSegment(sketch, "E569.MirrorCS", {"start": v(-15.5, 70.5) * mm, "end": v(-15.5, 82.5) * mm});
            skPoint(sketch, "E570.MirrorP", {"position": v(-103.5, -49.5) * mm});
            skLineSegment(sketch, "E571.MirrorCS", {"start": v(-36.5, 66.5) * mm, "end": v(-48.5, 66.5) * mm});
            skLineSegment(sketch, "E572.MirrorCS", {"start": v(-53.5, -18.5) * mm, "end": v(-65.5, -18.5) * mm});
            skArc(sketch, "E573.MirrorCS", {"start": v(-18.5, -53.5) * mm, "mid": v(-18.8, -52.8) * mm, "end": v(-19.5, -52.5) * mm});
            skLineSegment(sketch, "E574.MirrorCS", {"start": v(-15.5, 104.5) * mm, "end": v(-15.5, 113.95) * mm});
            skPoint(sketch, "E575.MirrorP", {"position": v(-15.5, 69.5) * mm});
            skLineSegment(sketch, "E576.MirrorCS", {"start": v(-36.5, 100.5) * mm, "end": v(-48.5, 100.5) * mm});
            skArc(sketch, "E577.MirrorCS", {"start": v(-2.5, -15.5) * mm, "mid": v(-1.8, -15.2) * mm, "end": v(-1.5, -14.5) * mm});
            skPoint(sketch, "E578.MirrorP", {"position": v(-69.5, 1.5) * mm});
            skLineSegment(sketch, "E579.MirrorCS", {"start": v(-49.5, -87.5) * mm, "end": v(-49.5, -99.5) * mm});
            skPoint(sketch, "E580.MirrorP", {"position": v(-1.5, -66.5) * mm});
            skArc(sketch, "E581.MirrorCS", {"start": v(-19.5, 32.5) * mm, "mid": v(-18.8, 32.2) * mm, "end": v(-18.5, 31.5) * mm});
            skPoint(sketch, "E582.MirrorP", {"position": v(-15.5, -1.5) * mm});
            skLineSegment(sketch, "E583.MirrorCS", {"start": v(-66.5, 19.5) * mm, "end": v(-66.5, 31.5) * mm});
            skArc(sketch, "E584.MirrorCS", {"start": v(-1.5, -19.5) * mm, "mid": v(-1.8, -18.8) * mm, "end": v(-2.5, -18.5) * mm});
            skArc(sketch, "E585.MirrorCS", {"start": v(-19.5, 66.5) * mm, "mid": v(-18.8, 66.2) * mm, "end": v(-18.5, 65.5) * mm});
            skLineSegment(sketch, "E586.MirrorCS", {"start": v(-66.5, 53.5) * mm, "end": v(-66.5, 65.5) * mm});
            skPoint(sketch, "E587.MirrorP", {"position": v(-32.5, 15.5) * mm});
            skPoint(sketch, "E588.MirrorP", {"position": v(-66.5, 66.5) * mm});
            skLineSegment(sketch, "E589.MirrorCS", {"start": v(-87.5, -66.5) * mm, "end": v(-93.82, -66.5) * mm});
            skPoint(sketch, "E590.MirrorP", {"position": v(-35.5, -103.5) * mm});
            skArc(sketch, "E591.MirrorCS", {"start": v(-19.5, 100.5) * mm, "mid": v(-18.8, 100.2) * mm, "end": v(-18.5, 99.5) * mm});
            skPoint(sketch, "E592.MirrorP", {"position": v(-83.5, -49.5) * mm});
            skLineSegment(sketch, "E593.MirrorCS", {"start": v(-66.5, 87.5) * mm, "end": v(-66.5, 93.82) * mm});
            skArc(sketch, "E594.MirrorCS", {"start": v(-82.5, -18.5) * mm, "mid": v(-83.2, -18.8) * mm, "end": v(-83.5, -19.5) * mm});
            skPoint(sketch, "E595.MirrorP", {"position": v(-52.5, 15.5) * mm});
            skLineSegment(sketch, "E596.MirrorCS", {"start": v(-36.5, 18.5) * mm, "end": v(-48.5, 18.5) * mm});
            skArc(sketch, "E597.MirrorCS", {"start": v(-83.5, 31.5) * mm, "mid": v(-83.2, 32.2) * mm, "end": v(-82.5, 32.5) * mm});
            skPoint(sketch, "E598.MirrorP", {"position": v(-66.5, -83.5) * mm});
            skLineSegment(sketch, "E599.MirrorCS", {"start": v(-32.5, -70.5) * mm, "end": v(-32.5, -82.5) * mm});
            skLineSegment(sketch, "E600.MirrorCS", {"start": v(-36.5, 52.5) * mm, "end": v(-48.5, 52.5) * mm});
            skArc(sketch, "E601.MirrorCS", {"start": v(-83.5, 65.5) * mm, "mid": v(-83.2, 66.2) * mm, "end": v(-82.5, 66.5) * mm});
            skLineSegment(sketch, "E602.MirrorCS", {"start": v(-36.5, 86.5) * mm, "end": v(-48.5, 86.5) * mm});
            skArc(sketch, "E603.MirrorCS", {"start": v(-99.5, 1.5) * mm, "mid": v(-100.2, 1.8) * mm, "end": v(-100.5, 2.5) * mm});
            skLineSegment(sketch, "E604.MirrorCS", {"start": v(-52.5, 2.5) * mm, "end": v(-52.5, 14.5) * mm});
            skArc(sketch, "E605.MirrorCS", {"start": v(-99.5, 35.5) * mm, "mid": v(-100.2, 35.8) * mm, "end": v(-100.5, 36.5) * mm});
            skLineSegment(sketch, "E606.MirrorCS", {"start": v(-52.5, 36.5) * mm, "end": v(-52.5, 48.5) * mm});
            skArc(sketch, "E607.MirrorCS", {"start": v(-86.5, 70.5) * mm, "mid": v(-86.8, 69.8) * mm, "end": v(-87.5, 69.5) * mm});
            skLineSegment(sketch, "E608.MirrorCS", {"start": v(-52.5, 70.5) * mm, "end": v(-52.5, 82.5) * mm});
            skLineSegment(sketch, "E609.MirrorCS", {"start": v(-1.5, 1.5) * mm, "end": v(-1.5, 18.5) * mm, "construction": true});
            skPoint(sketch, "E610.MirrorP", {"position": v(-103.5, 15.5) * mm});
            skArc(sketch, "E611.MirrorCS", {"start": v(-70.5, 15.5) * mm, "mid": v(-69.8, 15.2) * mm, "end": v(-69.5, 14.5) * mm});
            skArc(sketch, "E612.MirrorCS", {"start": v(-36.5, -32.5) * mm, "mid": v(-35.8, -32.2) * mm, "end": v(-35.5, -31.5) * mm});
            skArc(sketch, "E613.MirrorCS", {"start": v(-70.5, 49.5) * mm, "mid": v(-69.8, 49.2) * mm, "end": v(-69.5, 48.5) * mm});
            skPoint(sketch, "E614.MirrorP", {"position": v(-86.5, 1.5) * mm});
            skArc(sketch, "E615.MirrorCS", {"start": v(-65.5, -52.5) * mm, "mid": v(-66.2, -52.8) * mm, "end": v(-66.5, -53.5) * mm});
            skPoint(sketch, "E616.MirrorP", {"position": v(-1.5, -83.5) * mm});
            skLineSegment(sketch, "E617.MirrorCS", {"start": v(-70.5, 83.5) * mm, "end": v(-79.07, 83.5) * mm});
            skLineSegment(sketch, "E618.MirrorCS", {"start": v(-32.5, -19.5) * mm, "end": v(-32.5, -31.5) * mm});
            skPoint(sketch, "E619.MirrorP", {"position": v(-18.5, 86.5) * mm});
            skPoint(sketch, "E620.MirrorP", {"position": v(-100.5, 32.5) * mm});
            skPoint(sketch, "E621.MirrorP", {"position": v(-35.5, 15.5) * mm});
            skArc(sketch, "E622.MirrorCS", {"start": v(-100.5, 31.5) * mm, "mid": v(-100.2, 32.2) * mm, "end": v(-99.5, 32.5) * mm});
            skPoint(sketch, "E623.MirrorP", {"position": v(-49.5, -100.5) * mm});
            skLineSegment(sketch, "E624.MirrorCS", {"start": v(-87.5, -35.5) * mm, "end": v(-99.5, -35.5) * mm});
            skPoint(sketch, "E625.MirrorP", {"position": v(-100.5, 35.5) * mm});
            skPoint(sketch, "E626.MirrorP", {"position": v(-35.5, -32.5) * mm});
            skLineSegment(sketch, "E627.MirrorCS", {"start": v(-86.5, 53.5) * mm, "end": v(-86.5, 65.5) * mm});
            skArc(sketch, "E628.MirrorCS", {"start": v(-103.5, -2.5) * mm, "mid": v(-103.8, -1.8) * mm, "end": v(-104.5, -1.5) * mm});
            skPoint(sketch, "E629.MirrorP", {"position": v(-1.5, -86.5) * mm});
            skArc(sketch, "E630.MirrorCS", {"start": v(-103.5, 19.5) * mm, "mid": v(-103.8, 18.8) * mm, "end": v(-104.5, 18.5) * mm});
            skLineSegment(sketch, "E631.MirrorCS", {"start": v(-36.5, -1.5) * mm, "end": v(-48.5, -1.5) * mm});
            skArc(sketch, "E632.MirrorCS", {"start": v(-15.5, 113.95) * mm, "mid": v(-8.52, 114.68) * mm, "end": v(-1.5, 115) * mm});
            skLineSegment(sketch, "E633.MirrorCS", {"start": v(-2.5, -35.5) * mm, "end": v(-14.5, -35.5) * mm});
            skArc(sketch, "E634.MirrorCS", {"start": v(-31.5, -52.5) * mm, "mid": v(-32.2, -52.8) * mm, "end": v(-32.5, -53.5) * mm});
            skLineSegment(sketch, "E635.MirrorCS", {"start": v(-18.5, -2.5) * mm, "end": v(-18.5, -14.5) * mm});
            skLineSegment(sketch, "E636.MirrorCS", {"start": v(-70.5, -69.5) * mm, "end": v(-82.5, -69.5) * mm});
            skPoint(sketch, "E637.MirrorP", {"position": v(-66.5, 15.5) * mm});
            skArc(sketch, "E638.MirrorCS", {"start": v(-36.5, -15.5) * mm, "mid": v(-35.8, -15.2) * mm, "end": v(-35.5, -14.5) * mm});
            skPoint(sketch, "E639.MirrorP", {"position": v(-1.5, -32.5) * mm});
            skArc(sketch, "E640.MirrorCS", {"start": v(-19.5, -83.5) * mm, "mid": v(-18.8, -83.2) * mm, "end": v(-18.5, -82.5) * mm});
            skPoint(sketch, "E641.MirrorP", {"position": v(-1.5, 1.5) * mm});
            skArc(sketch, "E642.MirrorCS", {"start": v(-86.5, -36.5) * mm, "mid": v(-86.8, -35.8) * mm, "end": v(-87.5, -35.5) * mm});
            skPoint(sketch, "E643.MirrorP", {"position": v(-49.5, -86.5) * mm});
            skPoint(sketch, "E644.MirrorP", {"position": v(-15.5, 18.5) * mm});
            skPoint(sketch, "E645.MirrorP", {"position": v(-49.5, 69.5) * mm});
            skArc(sketch, "E646.MirrorCS", {"start": v(-48.5, -1.5) * mm, "mid": v(-49.2, -1.8) * mm, "end": v(-49.5, -2.5) * mm});
            skPoint(sketch, "E647.MirrorP", {"position": v(-100.5, -35.5) * mm});
            skPoint(sketch, "E648.MirrorP", {"position": v(-49.5, -15.5) * mm});
            skPoint(sketch, "E649.MirrorP", {"position": v(-52.5, -86.5) * mm});
            skArc(sketch, "E650.MirrorCS", {"start": v(-32.5, -99.5) * mm, "mid": v(-32.2, -100.2) * mm, "end": v(-31.5, -100.5) * mm});
            skLineSegment(sketch, "E651.MirrorCS", {"start": v(-18.5, -19.5) * mm, "end": v(-18.5, -31.5) * mm});
            skPoint(sketch, "E652.MirrorP", {"position": v(-103.5, 49.5) * mm});
            skArc(sketch, "E653.MirrorCS", {"start": v(-35.5, -2.5) * mm, "mid": v(-35.8, -1.8) * mm, "end": v(-36.5, -1.5) * mm});
            skLineSegment(sketch, "E654.MirrorCS", {"start": v(-69.5, -70.5) * mm, "end": v(-69.5, -82.5) * mm});
            skArc(sketch, "E655.MirrorCS", {"start": v(-104.5, -32.5) * mm, "mid": v(-103.8, -32.2) * mm, "end": v(-103.5, -31.5) * mm});
            skArc(sketch, "E656.MirrorCS", {"start": v(-1.5, 36.5) * mm, "mid": v(-1.8, 35.8) * mm, "end": v(-2.5, 35.5) * mm});
            skLineSegment(sketch, "E657.MirrorCS", {"start": v(-19.5, -83.5) * mm, "end": v(-31.5, -83.5) * mm});
            skArc(sketch, "E658.MirrorCS", {"start": v(-48.5, -18.5) * mm, "mid": v(-49.2, -18.8) * mm, "end": v(-49.5, -19.5) * mm});
            skArc(sketch, "E659.MirrorCS", {"start": v(-1.5, 70.5) * mm, "mid": v(-1.8, 69.8) * mm, "end": v(-2.5, 69.5) * mm});
            skArc(sketch, "E660.MirrorCS", {"start": v(-32.5, -65.5) * mm, "mid": v(-32.2, -66.2) * mm, "end": v(-31.5, -66.5) * mm});
            skArc(sketch, "E661.MirrorCS", {"start": v(-100.5, -31.5) * mm, "mid": v(-100.2, -32.2) * mm, "end": v(-99.5, -32.5) * mm});
            skLineSegment(sketch, "E662.MirrorCS", {"start": v(-32.5, 2.5) * mm, "end": v(-32.5, 14.5) * mm});
            skPoint(sketch, "E663.MirrorP", {"position": v(-69.5, 86.5) * mm});
            skPoint(sketch, "E664.MirrorP", {"position": v(-1.5, -49.5) * mm});
            skArc(sketch, "E665.MirrorCS", {"start": v(-100.5, -14.5) * mm, "mid": v(-100.2, -15.2) * mm, "end": v(-99.5, -15.5) * mm});
            skArc(sketch, "E666.MirrorCS", {"start": v(-69.5, -70.5) * mm, "mid": v(-69.8, -69.8) * mm, "end": v(-70.5, -69.5) * mm});
            skLineSegment(sketch, "E667.MirrorCS", {"start": v(-32.5, 36.5) * mm, "end": v(-32.5, 48.5) * mm});
            skLineSegment(sketch, "E668.MirrorCS", {"start": v(-18.5, -87.5) * mm, "end": v(-18.5, -99.5) * mm});
            skPoint(sketch, "E669.MirrorP", {"position": v(-52.5, -66.5) * mm});
            skArc(sketch, "E670.MirrorCS", {"start": v(-115, -1.5) * mm, "mid": v(-114.68, -8.52) * mm, "end": v(-113.95, -15.5) * mm});
            skLineSegment(sketch, "E671.MirrorCS", {"start": v(-32.5, 70.5) * mm, "end": v(-32.5, 82.5) * mm});
            skArc(sketch, "E672.MirrorCS", {"start": v(-35.5, -70.5) * mm, "mid": v(-35.8, -69.8) * mm, "end": v(-36.5, -69.5) * mm});
            skPoint(sketch, "E673.MirrorP", {"position": v(-15.5, 35.5) * mm});
            skLineSegment(sketch, "E674.MirrorCS", {"start": v(-103.5, -36.5) * mm, "end": v(-103.5, -48.5) * mm});
            skLineSegment(sketch, "E675.MirrorCS", {"start": v(-32.5, 104.5) * mm, "end": v(-32.5, 110.31) * mm});
            skPoint(sketch, "E676.MirrorP", {"position": v(-49.5, 86.5) * mm});
            skArc(sketch, "E677.MirrorCS", {"start": v(-66.5, -82.5) * mm, "mid": v(-66.2, -83.2) * mm, "end": v(-65.5, -83.5) * mm});
            skPoint(sketch, "E678.MirrorP", {"position": v(-69.5, 35.5) * mm});
            skPoint(sketch, "E679.MirrorP", {"position": v(-66.5, -49.5) * mm});
            skPoint(sketch, "E680.MirrorP", {"position": v(-66.5, -32.5) * mm});
            skArc(sketch, "E681.MirrorCS", {"start": v(-14.5, 35.5) * mm, "mid": v(-15.2, 35.8) * mm, "end": v(-15.5, 36.5) * mm});
            skArc(sketch, "E682.MirrorCS", {"start": v(-2.5, -66.5) * mm, "mid": v(-1.8, -66.2) * mm, "end": v(-1.5, -65.5) * mm});
            skArc(sketch, "E683.MirrorCS", {"start": v(-36.5, 32.5) * mm, "mid": v(-35.8, 32.2) * mm, "end": v(-35.5, 31.5) * mm});
            skLineSegment(sketch, "E684.MirrorCS", {"start": v(-1.5, -36.5) * mm, "end": v(-1.5, -48.5) * mm});
            skArc(sketch, "E685.MirrorCS", {"start": v(-14.5, 69.5) * mm, "mid": v(-15.2, 69.8) * mm, "end": v(-15.5, 70.5) * mm});
            skArc(sketch, "E686.MirrorCS", {"start": v(-36.5, 66.5) * mm, "mid": v(-35.8, 66.2) * mm, "end": v(-35.5, 65.5) * mm});
            skPoint(sketch, "E687.MirrorP", {"position": v(-66.5, 32.5) * mm});
            skArc(sketch, "E688.MirrorCS", {"start": v(-18.5, -19.5) * mm, "mid": v(-18.8, -18.8) * mm, "end": v(-19.5, -18.5) * mm});
            skPoint(sketch, "E689.MirrorP", {"position": v(-32.5, -83.5) * mm});
            skArc(sketch, "E690.MirrorCS", {"start": v(-14.5, 103.5) * mm, "mid": v(-15.2, 103.8) * mm, "end": v(-15.5, 104.5) * mm});
            skPoint(sketch, "E691.MirrorP", {"position": v(-66.5, -1.5) * mm});
            skArc(sketch, "E692.MirrorCS", {"start": v(-36.5, 100.5) * mm, "mid": v(-35.8, 100.2) * mm, "end": v(-35.5, 99.5) * mm});
            skArc(sketch, "E693.MirrorCS", {"start": v(-2.5, -32.5) * mm, "mid": v(-1.8, -32.2) * mm, "end": v(-1.5, -31.5) * mm});
            skLineSegment(sketch, "E694.MirrorCS", {"start": v(-18.5, 19.5) * mm, "end": v(-18.5, 31.5) * mm});
            skPoint(sketch, "E695.MirrorP", {"position": v(-35.5, -52.5) * mm});
            skArc(sketch, "E696.MirrorCS", {"start": v(-65.5, 18.5) * mm, "mid": v(-66.2, 18.8) * mm, "end": v(-66.5, 19.5) * mm});
            skPoint(sketch, "E697.MirrorP", {"position": v(-52.5, -49.5) * mm});
            skPoint(sketch, "E698.MirrorP", {"position": v(-15.5, -103.5) * mm});
            skArc(sketch, "E699.MirrorCS", {"start": v(-49.5, -31.5) * mm, "mid": v(-49.2, -32.2) * mm, "end": v(-48.5, -32.5) * mm});
            skLineSegment(sketch, "E700.MirrorCS", {"start": v(-18.5, 53.5) * mm, "end": v(-18.5, 65.5) * mm});
            skArc(sketch, "E701.MirrorCS", {"start": v(-65.5, 52.5) * mm, "mid": v(-66.2, 52.8) * mm, "end": v(-66.5, 53.5) * mm});
            skLineSegment(sketch, "E702.MirrorCS", {"start": v(-35.5, -19.5) * mm, "end": v(-35.5, -31.5) * mm});
            skLineSegment(sketch, "E703.MirrorCS", {"start": v(-18.5, 87.5) * mm, "end": v(-18.5, 99.5) * mm});
            skArc(sketch, "E704.MirrorCS", {"start": v(-65.5, 86.5) * mm, "mid": v(-66.2, 86.8) * mm, "end": v(-66.5, 87.5) * mm});
            skLineSegment(sketch, "E705.MirrorCS", {"start": v(-53.5, -86.5) * mm, "end": v(-65.5, -86.5) * mm});
            skArc(sketch, "E706.MirrorCS", {"start": v(-35.5, 2.5) * mm, "mid": v(-35.8, 1.8) * mm, "end": v(-36.5, 1.5) * mm});
            skLineSegment(sketch, "E707.MirrorCS", {"start": v(-83.5, 19.5) * mm, "end": v(-83.5, 31.5) * mm});
            skLineSegment(sketch, "E708.MirrorCS", {"start": v(-19.5, -52.5) * mm, "end": v(-31.5, -52.5) * mm});
            skArc(sketch, "E709.MirrorCS", {"start": v(-35.5, 36.5) * mm, "mid": v(-35.8, 35.8) * mm, "end": v(-36.5, 35.5) * mm});
            skLineSegment(sketch, "E710.MirrorCS", {"start": v(-83.5, 53.5) * mm, "end": v(-83.5, 65.5) * mm});
            skArc(sketch, "E711.MirrorCS", {"start": v(-35.5, 70.5) * mm, "mid": v(-35.8, 69.8) * mm, "end": v(-36.5, 69.5) * mm});
            skPoint(sketch, "E712.MirrorP", {"position": v(-32.5, 86.5) * mm});
            skLineSegment(sketch, "E713.MirrorCS", {"start": v(-87.5, 1.5) * mm, "end": v(-99.5, 1.5) * mm});
            skPoint(sketch, "E714.MirrorP", {"position": v(-86.5, 49.5) * mm});
            skArc(sketch, "E715.MirrorCS", {"start": v(-66.5, 14.5) * mm, "mid": v(-66.2, 15.2) * mm, "end": v(-65.5, 15.5) * mm});
            skLineSegment(sketch, "E716.MirrorCS", {"start": v(-87.5, 35.5) * mm, "end": v(-99.5, 35.5) * mm});
            skArc(sketch, "E717.MirrorCS", {"start": v(-66.5, 48.5) * mm, "mid": v(-66.2, 49.2) * mm, "end": v(-65.5, 49.5) * mm});
            skPoint(sketch, "E718.MirrorP", {"position": v(-69.5, 52.5) * mm});
            skLineSegment(sketch, "E719.MirrorCS", {"start": v(-86.5, 70.5) * mm, "end": v(-86.5, 75.78) * mm});
            skArc(sketch, "E720.MirrorCS", {"start": v(-66.5, 82.5) * mm, "mid": v(-66.2, 83.2) * mm, "end": v(-65.5, 83.5) * mm});
            skLineSegment(sketch, "E721.MirrorCS", {"start": v(-1.5, 1.5) * mm, "end": v(-18.5, 1.5) * mm, "construction": true});
            skPoint(sketch, "E722.MirrorP", {"position": v(-18.5, 52.5) * mm});
            skPoint(sketch, "E723.MirrorP", {"position": v(-83.5, 15.5) * mm});
            skLineSegment(sketch, "E724.MirrorCS", {"start": v(-69.5, 2.5) * mm, "end": v(-69.5, 14.5) * mm});
            skPoint(sketch, "E725.MirrorP", {"position": v(-86.5, -35.5) * mm});
            skPoint(sketch, "E726.MirrorP", {"position": v(-100.5, 1.5) * mm});
            skArc(sketch, "E727.MirrorCS", {"start": v(-49.5, -14.5) * mm, "mid": v(-49.2, -15.2) * mm, "end": v(-48.5, -15.5) * mm});
            skLineSegment(sketch, "E728.MirrorCS", {"start": v(-69.5, 36.5) * mm, "end": v(-69.5, 48.5) * mm});
            skLineSegment(sketch, "E729.MirrorCS", {"start": v(-18.5, -104.5) * mm, "end": v(-18.5, -113.5) * mm});
            skPoint(sketch, "E730.MirrorP", {"position": v(-1.5, -18.5) * mm});
            skArc(sketch, "E731.MirrorCS", {"start": v(-70.5, 83.5) * mm, "mid": v(-69.8, 83.2) * mm, "end": v(-69.5, 82.5) * mm});
            skArc(sketch, "E732.MirrorCS", {"start": v(-14.5, -1.5) * mm, "mid": v(-15.2, -1.8) * mm, "end": v(-15.5, -2.5) * mm});
            skLineSegment(sketch, "E733.MirrorCS", {"start": v(-100.5, 19.5) * mm, "end": v(-100.5, 31.5) * mm});
            skLineSegment(sketch, "E734.MirrorCS", {"start": v(-66.5, -53.5) * mm, "end": v(-66.5, -65.5) * mm});
            skLineSegment(sketch, "E735.MirrorCS", {"start": v(-100.5, 53.5) * mm, "end": v(-100.5, 55.9) * mm});
            skLineSegment(sketch, "E736.MirrorCS", {"start": v(-1.5, -1.5) * mm, "end": v(-18.5, -1.5) * mm, "construction": true});
            skLineSegment(sketch, "E737.MirrorCS", {"start": v(-104.5, 32.5) * mm, "end": v(-110.31, 32.5) * mm});
            skArc(sketch, "E738.MirrorCS", {"start": v(-15.5, -65.5) * mm, "mid": v(-15.2, -66.2) * mm, "end": v(-14.5, -66.5) * mm});
            skArc(sketch, "E739.MirrorCS", {"start": v(-32.5, 110.31) * mm, "mid": v(-25.55, 112.13) * mm, "end": v(-18.5, 113.5) * mm});
            skLineSegment(sketch, "E740.MirrorCS", {"start": v(-1.5, -1.5) * mm, "end": v(-1.5, -18.5) * mm, "construction": true});
            skArc(sketch, "E741.MirrorCS", {"start": v(-36.5, -100.5) * mm, "mid": v(-35.8, -100.2) * mm, "end": v(-35.5, -99.5) * mm});
            skPoint(sketch, "E742.MirrorP", {"position": v(-18.5, -49.5) * mm});
            skPoint(sketch, "E743.MirrorP", {"position": v(-15.5, -86.5) * mm});
            skPoint(sketch, "E744.MirrorP", {"position": v(-86.5, -49.5) * mm});
            skArc(sketch, "E745.MirrorCS", {"start": v(-1.5, -87.5) * mm, "mid": v(-1.8, -86.8) * mm, "end": v(-2.5, -86.5) * mm});
            skLineSegment(sketch, "E746.MirrorCS", {"start": v(-87.5, -1.5) * mm, "end": v(-99.5, -1.5) * mm});
            skPoint(sketch, "E747.MirrorP", {"position": v(-49.5, -18.5) * mm});
            skLineSegment(sketch, "E748.MirrorCS", {"start": v(-53.5, -69.5) * mm, "end": v(-65.5, -69.5) * mm});
            skPoint(sketch, "E749.MirrorP", {"position": v(-49.5, 35.5) * mm});
            skPoint(sketch, "E750.MirrorP", {"position": v(-100.5, -15.5) * mm});
            skLineSegment(sketch, "E751.MirrorCS", {"start": v(-15.5, -19.5) * mm, "end": v(-15.5, -31.5) * mm});
            skPoint(sketch, "E752.MirrorP", {"position": v(-86.5, -18.5) * mm});
            skPoint(sketch, "E753.MirrorP", {"position": v(-32.5, -100.5) * mm});
            skArc(sketch, "E754.MirrorCS", {"start": v(-86.5, -70.5) * mm, "mid": v(-86.8, -69.8) * mm, "end": v(-87.5, -69.5) * mm});
            skPoint(sketch, "E755.MirrorP", {"position": v(-86.5, 66.5) * mm});
            skPoint(sketch, "E756.MirrorP", {"position": v(-18.5, -32.5) * mm});
            skLineSegment(sketch, "E757.MirrorCS", {"start": v(-1.5, -53.5) * mm, "end": v(-1.5, -65.5) * mm});
            skArc(sketch, "E758.MirrorCS", {"start": v(-70.5, -32.5) * mm, "mid": v(-69.8, -32.2) * mm, "end": v(-69.5, -31.5) * mm});
            skArc(sketch, "E759.MirrorCS", {"start": v(-100.5, -48.5) * mm, "mid": v(-100.2, -49.2) * mm, "end": v(-99.5, -49.5) * mm});
            skLineSegment(sketch, "E760.MirrorCS", {"start": v(-15.5, -70.5) * mm, "end": v(-15.5, -82.5) * mm});
            skArc(sketch, "E761.MirrorCS", {"start": v(-66.5, -14.5) * mm, "mid": v(-66.2, -15.2) * mm, "end": v(-65.5, -15.5) * mm});
            skPoint(sketch, "E762.MirrorP", {"position": v(-83.5, 35.5) * mm});
            skLineSegment(sketch, "E763.MirrorCS", {"start": v(-69.5, -2.5) * mm, "end": v(-69.5, -14.5) * mm});
            skPoint(sketch, "E764.MirrorP", {"position": v(-1.5, 69.5) * mm});
            skLineSegment(sketch, "E765.MirrorCS", {"start": v(-83.5, -36.5) * mm, "end": v(-83.5, -48.5) * mm});
            skLineSegment(sketch, "E766.MirrorCS", {"start": v(-1.5, -70.5) * mm, "end": v(-1.5, -82.5) * mm});
            skArc(sketch, "E767.MirrorCS", {"start": v(-53.5, -100.5) * mm, "mid": v(-52.8, -100.2) * mm, "end": v(-52.5, -99.5) * mm});
            skPoint(sketch, "E768.MirrorP", {"position": v(-15.5, 1.5) * mm});
            skArc(sketch, "E769.MirrorCS", {"start": v(-53.5, -49.5) * mm, "mid": v(-52.8, -49.2) * mm, "end": v(-52.5, -48.5) * mm});
            skPoint(sketch, "E770.MirrorP", {"position": v(-49.5, 52.5) * mm});
            skPoint(sketch, "E771.MirrorP", {"position": v(-15.5, 100.5) * mm});
            skPoint(sketch, "E772.MirrorP", {"position": v(-49.5, 104.5) * mm});
            skArc(sketch, "E773.MirrorCS", {"start": v(-53.5, -32.5) * mm, "mid": v(-52.8, -32.2) * mm, "end": v(-52.5, -31.5) * mm});
            skPoint(sketch, "E774.MirrorP", {"position": v(-100.5, -49.5) * mm});
            skLineSegment(sketch, "E775.MirrorCS", {"start": v(-53.5, -15.5) * mm, "end": v(-65.5, -15.5) * mm});
            skPoint(sketch, "E776.MirrorP", {"position": v(-49.5, -69.5) * mm});
            skPoint(sketch, "E777.MirrorP", {"position": v(-83.5, -18.5) * mm});
            skArc(sketch, "E778.MirrorCS", {"start": v(-109.38, -35.5) * mm, "mid": v(-106.86, -42.49) * mm, "end": v(-103.9, -49.3) * mm});
            skArc(sketch, "E779.MirrorCS", {"start": v(-31.5, -1.5) * mm, "mid": v(-32.2, -1.8) * mm, "end": v(-32.5, -2.5) * mm});
            skPoint(sketch, "E780.MirrorP", {"position": v(-35.5, 103.5) * mm});
            skArc(sketch, "E781.MirrorCS", {"start": v(-19.5, -32.5) * mm, "mid": v(-18.8, -32.2) * mm, "end": v(-18.5, -31.5) * mm});
            skPoint(sketch, "E782.MirrorP", {"position": v(-35.5, -49.5) * mm});
            skLineSegment(sketch, "E783.MirrorCS", {"start": v(-70.5, -18.5) * mm, "end": v(-82.5, -18.5) * mm});
            skPoint(sketch, "E784.MirrorP", {"position": v(-52.5, -18.5) * mm});
            skLineSegment(sketch, "E785.MirrorCS", {"start": v(-36.5, -18.5) * mm, "end": v(-48.5, -18.5) * mm});
            skLineSegment(sketch, "E786.MirrorCS", {"start": v(-2.5, 35.5) * mm, "end": v(-14.5, 35.5) * mm});
            skArc(sketch, "E787.MirrorCS", {"start": v(-82.5, -52.5) * mm, "mid": v(-83.2, -52.8) * mm, "end": v(-83.5, -53.5) * mm});
            skPoint(sketch, "E788.MirrorP", {"position": v(-69.5, -35.5) * mm});
            skPoint(sketch, "E789.MirrorP", {"position": v(-49.5, -52.5) * mm});
            skArc(sketch, "E790.MirrorCS", {"start": v(-70.5, -83.5) * mm, "mid": v(-69.8, -83.2) * mm, "end": v(-69.5, -82.5) * mm});
            skLineSegment(sketch, "E791.MirrorCS", {"start": v(-2.5, 69.5) * mm, "end": v(-14.5, 69.5) * mm});
            skLineSegment(sketch, "E792.MirrorCS", {"start": v(-19.5, -86.5) * mm, "end": v(-31.5, -86.5) * mm});
            skArc(sketch, "E793.MirrorCS", {"start": v(-32.5, -110.31) * mm, "mid": v(-25.55, -112.13) * mm, "end": v(-18.5, -113.5) * mm});
            skLineSegment(sketch, "E794.MirrorCS", {"start": v(-2.5, 103.5) * mm, "end": v(-14.5, 103.5) * mm});
            skLineSegment(sketch, "E795.MirrorCS", {"start": v(-49.5, -53.5) * mm, "end": v(-49.5, -65.5) * mm});
            skArc(sketch, "E796.MirrorCS", {"start": v(-32.5, 31.5) * mm, "mid": v(-32.2, 32.2) * mm, "end": v(-31.5, 32.5) * mm});
            skArc(sketch, "E797.MirrorCS", {"start": v(-87.5, -66.5) * mm, "mid": v(-86.8, -66.2) * mm, "end": v(-86.5, -65.5) * mm});
            skArc(sketch, "E798.MirrorCS", {"start": v(-32.5, 65.5) * mm, "mid": v(-32.2, 66.2) * mm, "end": v(-31.5, 66.5) * mm});
            skArc(sketch, "E799.MirrorCS", {"start": v(-31.5, -103.5) * mm, "mid": v(-32.2, -103.8) * mm, "end": v(-32.5, -104.5) * mm});
            skArc(sketch, "E800.MirrorCS", {"start": v(-32.5, 99.5) * mm, "mid": v(-32.2, 100.2) * mm, "end": v(-31.5, 100.5) * mm});
            skPoint(sketch, "E801.MirrorP", {"position": v(-32.5, 52.5) * mm});
            skPoint(sketch, "E802.MirrorP", {"position": v(-86.5, 15.5) * mm});
            skArc(sketch, "E803.MirrorCS", {"start": v(-86.5, -53.5) * mm, "mid": v(-86.8, -52.8) * mm, "end": v(-87.5, -52.5) * mm});
            skLineSegment(sketch, "E804.MirrorCS", {"start": v(-36.5, 15.5) * mm, "end": v(-48.5, 15.5) * mm});
            skLineSegment(sketch, "E805.MirrorCS", {"start": v(-87.5, -69.5) * mm, "end": v(-91.62, -69.5) * mm});
            skPoint(sketch, "E806.MirrorP", {"position": v(-69.5, 18.5) * mm});
            skLineSegment(sketch, "E807.MirrorCS", {"start": v(-36.5, 49.5) * mm, "end": v(-48.5, 49.5) * mm});
            skPoint(sketch, "E808.MirrorP", {"position": v(-32.5, -1.5) * mm});
            skLineSegment(sketch, "E809.MirrorCS", {"start": v(-36.5, 83.5) * mm, "end": v(-48.5, 83.5) * mm});
            skPoint(sketch, "E810.MirrorP", {"position": v(-18.5, 18.5) * mm});
            skPoint(sketch, "E811.MirrorP", {"position": v(-52.5, 69.5) * mm});
            skPoint(sketch, "E812.MirrorP", {"position": v(-83.5, 49.5) * mm});
            skLineSegment(sketch, "E813.MirrorCS", {"start": v(-66.5, 2.5) * mm, "end": v(-66.5, 14.5) * mm});
            skPoint(sketch, "E814.MirrorP", {"position": v(-66.5, 86.5) * mm});
            skPoint(sketch, "E815.MirrorP", {"position": v(-83.5, 52.5) * mm});
            skPoint(sketch, "E816.MirrorP", {"position": v(-69.5, -52.5) * mm});
            skPoint(sketch, "E817.MirrorP", {"position": v(-18.5, -52.5) * mm});
            skLineSegment(sketch, "E818.MirrorCS", {"start": v(-66.5, 36.5) * mm, "end": v(-66.5, 48.5) * mm});
            skPoint(sketch, "E819.MirrorP", {"position": v(-1.5, 86.5) * mm});
            skLineSegment(sketch, "E820.MirrorCS", {"start": v(-66.5, 70.5) * mm, "end": v(-66.5, 82.5) * mm});
            skPoint(sketch, "E821.MirrorP", {"position": v(-1.5, -100.5) * mm});
            skArc(sketch, "E822.MirrorCS", {"start": v(-83.5, 14.5) * mm, "mid": v(-83.2, 15.2) * mm, "end": v(-82.5, 15.5) * mm});
            skArc(sketch, "E823.MirrorCS", {"start": v(-83.5, 48.5) * mm, "mid": v(-83.2, 49.2) * mm, "end": v(-82.5, 49.5) * mm});
            skLineSegment(sketch, "E824.MirrorCS", {"start": v(-69.5, 70.5) * mm, "end": v(-69.5, 82.5) * mm});
            skArc(sketch, "E825.MirrorCS", {"start": v(-99.5, 18.5) * mm, "mid": v(-100.2, 18.8) * mm, "end": v(-100.5, 19.5) * mm});
            skArc(sketch, "E826.MirrorCS", {"start": v(-99.5, 52.5) * mm, "mid": v(-100.2, 52.8) * mm, "end": v(-100.5, 53.5) * mm});
            skArc(sketch, "E827.MirrorCS", {"start": v(-104.5, 32.5) * mm, "mid": v(-103.8, 32.2) * mm, "end": v(-103.5, 31.5) * mm});
            skPoint(sketch, "E828.MirrorP", {"position": v(-35.5, -1.5) * mm});
            skPoint(sketch, "E829.MirrorP", {"position": v(-52.5, -35.5) * mm});
            skArc(sketch, "E830.MirrorCS", {"start": v(-49.3, 103.9) * mm, "mid": v(-42.49, 106.86) * mm, "end": v(-35.5, 109.38) * mm});
            skPoint(sketch, "E831.MirrorP", {"position": v(-49.5, 1.5) * mm});
            skArc(sketch, "E832.MirrorCS", {"start": v(-49.5, -82.5) * mm, "mid": v(-49.2, -83.2) * mm, "end": v(-48.5, -83.5) * mm});
            skPoint(sketch, "E833.MirrorP", {"position": v(-100.5, 52.5) * mm});
            skPoint(sketch, "E834.MirrorP", {"position": v(-1.5, -103.5) * mm});
            skPoint(sketch, "E835.MirrorP", {"position": v(-103.5, 18.5) * mm});
            skLineSegment(sketch, "E836.MirrorCS", {"start": v(-35.5, -2.5) * mm, "end": v(-35.5, -14.5) * mm});
            skLineSegment(sketch, "E837.MirrorCS", {"start": v(-66.5, -19.5) * mm, "end": v(-66.5, -31.5) * mm});
            skPoint(sketch, "E838.MirrorP", {"position": v(-32.5, 69.5) * mm});
            skPoint(sketch, "E839.MirrorP", {"position": v(-86.5, 32.5) * mm});
            skPoint(sketch, "E840.MirrorP", {"position": v(-15.5, -69.5) * mm});
            skLineSegment(sketch, "E841.MirrorCS", {"start": v(-87.5, -49.5) * mm, "end": v(-99.5, -49.5) * mm});
            skArc(sketch, "E842.MirrorCS", {"start": v(-36.5, -83.5) * mm, "mid": v(-35.8, -83.2) * mm, "end": v(-35.5, -82.5) * mm});
            skLineSegment(sketch, "E843.MirrorCS", {"start": v(-52.5, -87.5) * mm, "end": v(-52.5, -99.5) * mm});
            skPoint(sketch, "E844.MirrorP", {"position": v(-83.5, 1.5) * mm});
            skPoint(sketch, "E845.MirrorP", {"position": v(-52.5, -32.5) * mm});
            skPoint(sketch, "E846.MirrorP", {"position": v(-83.5, -52.5) * mm});
            skPoint(sketch, "E847.MirrorP", {"position": v(-1.5, 35.5) * mm});
            skPoint(sketch, "E848.MirrorP", {"position": v(-35.5, 86.5) * mm});
            skPoint(sketch, "E849.MirrorP", {"position": v(-35.5, -15.5) * mm});
            skPoint(sketch, "E850.MirrorP", {"position": v(-66.5, -15.5) * mm});
            skPoint(sketch, "E851.MirrorP", {"position": v(-49.5, 18.5) * mm});
            skPoint(sketch, "E852.MirrorP", {"position": v(-15.5, 66.5) * mm});
            skPoint(sketch, "E853.MirrorP", {"position": v(-103.5, 32.5) * mm});
            skPoint(sketch, "E854.MirrorP", {"position": v(-83.5, -66.5) * mm});
            skArc(sketch, "E855.MirrorCS", {"start": v(-75.78, -86.5) * mm, "mid": v(-72.69, -89.12) * mm, "end": v(-69.5, -91.62) * mm});
            skLineSegment(sketch, "E856.MirrorCS", {"start": v(-104.5, -1.5) * mm, "end": v(-115, -1.5) * mm});
            skPoint(sketch, "E857.MirrorP", {"position": v(-18.5, -69.5) * mm});
            skArc(sketch, "E858.MirrorCS", {"start": v(-18.5, -70.5) * mm, "mid": v(-18.8, -69.8) * mm, "end": v(-19.5, -69.5) * mm});
            skPoint(sketch, "E859.MirrorP", {"position": v(-86.5, 52.5) * mm});
            skPoint(sketch, "E860.MirrorP", {"position": v(-18.5, -66.5) * mm});
            skPoint(sketch, "E861.MirrorP", {"position": v(-52.5, -69.5) * mm});
            skLineSegment(sketch, "E862.MirrorCS", {"start": v(-70.5, -32.5) * mm, "end": v(-82.5, -32.5) * mm});
            skLineSegment(sketch, "E863.MirrorCS", {"start": v(-86.5, -36.5) * mm, "end": v(-86.5, -48.5) * mm});
            skArc(sketch, "E864.MirrorCS", {"start": v(-15.5, -82.5) * mm, "mid": v(-15.2, -83.2) * mm, "end": v(-14.5, -83.5) * mm});
            skLineSegment(sketch, "E865.MirrorCS", {"start": v(-52.5, -2.5) * mm, "end": v(-52.5, -14.5) * mm});
            skArc(sketch, "E866.MirrorCS", {"start": v(-70.5, -49.5) * mm, "mid": v(-69.8, -49.2) * mm, "end": v(-69.5, -48.5) * mm});
            skPoint(sketch, "E867.MirrorP", {"position": v(-32.5, 18.5) * mm});
            skPoint(sketch, "E868.MirrorP", {"position": v(-66.5, 69.5) * mm});
            skPoint(sketch, "E869.MirrorP", {"position": v(-69.5, 66.5) * mm});
            skPoint(sketch, "E870.MirrorP", {"position": v(-1.5, -52.5) * mm});
            skArc(sketch, "E871.MirrorCS", {"start": v(-103.5, -19.5) * mm, "mid": v(-103.8, -18.8) * mm, "end": v(-104.5, -18.5) * mm});
            skPoint(sketch, "E872.MirrorP", {"position": v(-18.5, -18.5) * mm});
            skPoint(sketch, "E873.MirrorP", {"position": v(-15.5, 83.5) * mm});
            skLineSegment(sketch, "E874.MirrorCS", {"start": v(-53.5, -83.5) * mm, "end": v(-65.5, -83.5) * mm});
            skPoint(sketch, "E875.MirrorP", {"position": v(-83.5, -32.5) * mm});
            skArc(sketch, "E876.MirrorCS", {"start": v(-52.5, -36.5) * mm, "mid": v(-52.8, -35.8) * mm, "end": v(-53.5, -35.5) * mm});
            skPoint(sketch, "E877.MirrorP", {"position": v(-52.5, 35.5) * mm});
            skLineSegment(sketch, "E878.MirrorCS", {"start": v(-1.5, -2.5) * mm, "end": v(-1.5, -14.5) * mm});
            skPoint(sketch, "E879.MirrorP", {"position": v(-83.5, 18.5) * mm});
            skPoint(sketch, "E880.MirrorP", {"position": v(-66.5, -35.5) * mm});
            skPoint(sketch, "E881.MirrorP", {"position": v(-32.5, -35.5) * mm});
            skPoint(sketch, "E882.MirrorP", {"position": v(-15.5, -49.5) * mm});
            skLineSegment(sketch, "E883.MirrorCS", {"start": v(-1.5, 53.5) * mm, "end": v(-1.5, 65.5) * mm});
            skLineSegment(sketch, "E884.MirrorCS", {"start": v(-32.5, -36.5) * mm, "end": v(-32.5, -48.5) * mm});
            skPoint(sketch, "E885.MirrorP", {"position": v(-1.5, 52.5) * mm});
            skLineSegment(sketch, "E886.MirrorCS", {"start": v(-1.5, 87.5) * mm, "end": v(-1.5, 99.5) * mm});
            skPoint(sketch, "E887.MirrorP", {"position": v(-100.5, -52.5) * mm});
            skArc(sketch, "E888.MirrorCS", {"start": v(-18.5, 2.5) * mm, "mid": v(-18.8, 1.8) * mm, "end": v(-19.5, 1.5) * mm});
            skArc(sketch, "E889.MirrorCS", {"start": v(-18.5, 36.5) * mm, "mid": v(-18.8, 35.8) * mm, "end": v(-19.5, 35.5) * mm});
            skArc(sketch, "E890.MirrorCS", {"start": v(-18.5, 70.5) * mm, "mid": v(-18.8, 69.8) * mm, "end": v(-19.5, 69.5) * mm});
            skLineSegment(sketch, "E891.MirrorCS", {"start": v(-49.5, 2.5) * mm, "end": v(-49.5, 14.5) * mm});
            skLineSegment(sketch, "E892.MirrorCS", {"start": v(-2.5, 49.5) * mm, "end": v(-14.5, 49.5) * mm});
            skLineSegment(sketch, "E893.MirrorCS", {"start": v(-49.5, 36.5) * mm, "end": v(-49.5, 48.5) * mm});
            skPoint(sketch, "E894.MirrorP", {"position": v(-86.5, -52.5) * mm});
            skLineSegment(sketch, "E895.MirrorCS", {"start": v(-2.5, 83.5) * mm, "end": v(-14.5, 83.5) * mm});
            skLineSegment(sketch, "E896.MirrorCS", {"start": v(-49.5, 70.5) * mm, "end": v(-49.5, 82.5) * mm});
            skPoint(sketch, "E897.MirrorP", {"position": v(-18.5, 83.5) * mm});
            skArc(sketch, "E898.MirrorCS", {"start": v(-31.5, 1.5) * mm, "mid": v(-32.2, 1.8) * mm, "end": v(-32.5, 2.5) * mm});
            skLineSegment(sketch, "E899.MirrorCS", {"start": v(-35.5, 104.5) * mm, "end": v(-35.5, 109.38) * mm});
            skPoint(sketch, "E900.MirrorP", {"position": v(-15.5, -35.5) * mm});
            skArc(sketch, "E901.MirrorCS", {"start": v(-31.5, 35.5) * mm, "mid": v(-32.2, 35.8) * mm, "end": v(-32.5, 36.5) * mm});
            skLineSegment(sketch, "E902.MirrorCS", {"start": v(-53.5, 32.5) * mm, "end": v(-65.5, 32.5) * mm});
            skArc(sketch, "E903.MirrorCS", {"start": v(-31.5, 69.5) * mm, "mid": v(-32.2, 69.8) * mm, "end": v(-32.5, 70.5) * mm});
            skPoint(sketch, "E904.MirrorP", {"position": v(-100.5, -18.5) * mm});
            skPoint(sketch, "E905.MirrorP", {"position": v(-100.5, 49.5) * mm});
            skLineSegment(sketch, "E906.MirrorCS", {"start": v(-53.5, 66.5) * mm, "end": v(-65.5, 66.5) * mm});
            skPoint(sketch, "E907.MirrorP", {"position": v(-69.5, -15.5) * mm});
            skArc(sketch, "E908.MirrorCS", {"start": v(-31.5, 103.5) * mm, "mid": v(-32.2, 103.8) * mm, "end": v(-32.5, 104.5) * mm});
            skArc(sketch, "E909.MirrorCS", {"start": v(-52.5, 87.5) * mm, "mid": v(-52.8, 86.8) * mm, "end": v(-53.5, 86.5) * mm});
            skPoint(sketch, "E910.MirrorP", {"position": v(-32.5, 35.5) * mm});
            skPoint(sketch, "E911.MirrorP", {"position": v(-69.5, 15.5) * mm});
            skLineSegment(sketch, "E912.MirrorCS", {"start": v(-35.5, 19.5) * mm, "end": v(-35.5, 31.5) * mm});
            skPoint(sketch, "E913.MirrorP", {"position": v(-69.5, 83.5) * mm});
            skArc(sketch, "E914.MirrorCS", {"start": v(-69.5, 19.5) * mm, "mid": v(-69.8, 18.8) * mm, "end": v(-70.5, 18.5) * mm});
            skPoint(sketch, "E915.MirrorP", {"position": v(-1.5, -15.5) * mm});
            skLineSegment(sketch, "E916.MirrorCS", {"start": v(-35.5, 53.5) * mm, "end": v(-35.5, 65.5) * mm});
            skArc(sketch, "E917.MirrorCS", {"start": v(-69.5, 53.5) * mm, "mid": v(-69.8, 52.8) * mm, "end": v(-70.5, 52.5) * mm});
            skLineSegment(sketch, "E918.MirrorCS", {"start": v(-35.5, 87.5) * mm, "end": v(-35.5, 99.5) * mm});
            skArc(sketch, "E919.MirrorCS", {"start": v(-87.5, 15.5) * mm, "mid": v(-86.8, 15.2) * mm, "end": v(-86.5, 14.5) * mm});
            skLineSegment(sketch, "E920.MirrorCS", {"start": v(-53.5, 18.5) * mm, "end": v(-65.5, 18.5) * mm});
            skArc(sketch, "E921.MirrorCS", {"start": v(-87.5, 49.5) * mm, "mid": v(-86.8, 49.2) * mm, "end": v(-86.5, 48.5) * mm});
            skLineSegment(sketch, "E922.MirrorCS", {"start": v(-53.5, 52.5) * mm, "end": v(-65.5, 52.5) * mm});
            skLineSegment(sketch, "E923.MirrorCS", {"start": v(-104.5, 15.5) * mm, "end": v(-113.95, 15.5) * mm});
            skPoint(sketch, "E924.MirrorP", {"position": v(-1.5, 83.5) * mm});
            skLineSegment(sketch, "E925.MirrorCS", {"start": v(-53.5, 86.5) * mm, "end": v(-65.5, 86.5) * mm});
            skArc(sketch, "E926.MirrorCS", {"start": v(-91.62, 69.5) * mm, "mid": v(-89.12, 72.69) * mm, "end": v(-86.5, 75.78) * mm});
            skPoint(sketch, "E927.MirrorP", {"position": v(-49.5, -1.5) * mm});
            skArc(sketch, "E928.MirrorCS", {"start": v(-82.5, 18.5) * mm, "mid": v(-83.2, 18.8) * mm, "end": v(-83.5, 19.5) * mm});
            skArc(sketch, "E929.MirrorCS", {"start": v(-49.5, -48.5) * mm, "mid": v(-49.2, -49.2) * mm, "end": v(-48.5, -49.5) * mm});
            skPoint(sketch, "E930.MirrorP", {"position": v(-35.5, 52.5) * mm});
            skArc(sketch, "E931.MirrorCS", {"start": v(-82.5, 52.5) * mm, "mid": v(-83.2, 52.8) * mm, "end": v(-83.5, 53.5) * mm});
            skArc(sketch, "E932.MirrorCS", {"start": v(-14.5, -86.5) * mm, "mid": v(-15.2, -86.8) * mm, "end": v(-15.5, -87.5) * mm});
            skArc(sketch, "E933.MirrorCS", {"start": v(-69.5, 87.5) * mm, "mid": v(-69.8, 86.8) * mm, "end": v(-70.5, 86.5) * mm});
            skPoint(sketch, "E934.MirrorP", {"position": v(-32.5, 103.5) * mm});
            skPoint(sketch, "E935.MirrorP", {"position": v(-15.5, 32.5) * mm});
            skLineSegment(sketch, "E936.MirrorCS", {"start": v(-70.5, -35.5) * mm, "end": v(-82.5, -35.5) * mm});
            skPoint(sketch, "E937.MirrorP", {"position": v(-49.5, 83.5) * mm});
            skPoint(sketch, "E938.MirrorP", {"position": v(-35.5, -35.5) * mm});
            skPoint(sketch, "E939.MirrorP", {"position": v(-103.5, -32.5) * mm});
            skPoint(sketch, "E940.MirrorP", {"position": v(-69.5, -32.5) * mm});
            skPoint(sketch, "E941.MirrorP", {"position": v(-15.5, -52.5) * mm});
            skArc(sketch, "E942.MirrorCS", {"start": v(-86.5, 19.5) * mm, "mid": v(-86.8, 18.8) * mm, "end": v(-87.5, 18.5) * mm});
            skPoint(sketch, "E943.MirrorP", {"position": v(-83.5, -1.5) * mm});
            skLineSegment(sketch, "E944.MirrorCS", {"start": v(-15.5, -87.5) * mm, "end": v(-15.5, -99.5) * mm});
            skLineSegment(sketch, "E945.MirrorCS", {"start": v(-87.5, 69.5) * mm, "end": v(-91.62, 69.5) * mm});
            skArc(sketch, "E946.MirrorCS", {"start": v(-35.5, -87.5) * mm, "mid": v(-35.8, -86.8) * mm, "end": v(-36.5, -86.5) * mm});
            skArc(sketch, "E947.MirrorCS", {"start": v(-103.5, 36.5) * mm, "mid": v(-103.8, 35.8) * mm, "end": v(-104.5, 35.5) * mm});
            skPoint(sketch, "E948.MirrorP", {"position": v(-35.5, -100.5) * mm});
            skArc(sketch, "E949.MirrorCS", {"start": v(-65.5, -35.5) * mm, "mid": v(-66.2, -35.8) * mm, "end": v(-66.5, -36.5) * mm});
            skPoint(sketch, "E950.MirrorP", {"position": v(-18.5, 100.5) * mm});
            skArc(sketch, "E951.MirrorCS", {"start": v(-2.5, 32.5) * mm, "mid": v(-1.8, 32.2) * mm, "end": v(-1.5, 31.5) * mm});
            skLineSegment(sketch, "E952.MirrorCS", {"start": v(-2.5, -86.5) * mm, "end": v(-14.5, -86.5) * mm});
            skLineSegment(sketch, "E953.MirrorCS", {"start": v(-36.5, -103.5) * mm, "end": v(-48.5, -103.5) * mm});
            skArc(sketch, "E954.MirrorCS", {"start": v(-14.5, -52.5) * mm, "mid": v(-15.2, -52.8) * mm, "end": v(-15.5, -53.5) * mm});
            skLineSegment(sketch, "E955.MirrorCS", {"start": v(-2.5, 32.5) * mm, "end": v(-14.5, 32.5) * mm});
            skLineSegment(sketch, "E956.MirrorCS", {"start": v(-35.5, -36.5) * mm, "end": v(-35.5, -48.5) * mm});
            skArc(sketch, "E957.MirrorCS", {"start": v(-18.5, -104.5) * mm, "mid": v(-18.8, -103.8) * mm, "end": v(-19.5, -103.5) * mm});
            skArc(sketch, "E958.MirrorCS", {"start": v(-83.5, -31.5) * mm, "mid": v(-83.2, -32.2) * mm, "end": v(-82.5, -32.5) * mm});
            skArc(sketch, "E959.MirrorCS", {"start": v(-1.5, 19.5) * mm, "mid": v(-1.8, 18.8) * mm, "end": v(-2.5, 18.5) * mm});
            skPoint(sketch, "E960.MirrorP", {"position": v(-15.5, 103.5) * mm});
            skArc(sketch, "E961.MirrorCS", {"start": v(-65.5, -1.5) * mm, "mid": v(-66.2, -1.8) * mm, "end": v(-66.5, -2.5) * mm});
            skPoint(sketch, "E962.MirrorP", {"position": v(-66.5, 35.5) * mm});
            skPoint(sketch, "E963.MirrorP", {"position": v(-69.5, 32.5) * mm});
            skPoint(sketch, "E964.MirrorP", {"position": v(-66.5, -86.5) * mm});
            skPoint(sketch, "E965.MirrorP", {"position": v(-66.5, -69.5) * mm});
            skLineSegment(sketch, "E966.MirrorCS", {"start": v(-69.5, -19.5) * mm, "end": v(-69.5, -31.5) * mm});
            skPoint(sketch, "E967.MirrorP", {"position": v(-15.5, 49.5) * mm});
            skPoint(sketch, "E968.MirrorP", {"position": v(-49.5, 100.5) * mm});
            skPoint(sketch, "E969.MirrorP", {"position": v(-49.5, -83.5) * mm});
            skArc(sketch, "E970.MirrorCS", {"start": v(-32.5, -31.5) * mm, "mid": v(-32.2, -32.2) * mm, "end": v(-31.5, -32.5) * mm});
            skPoint(sketch, "E971.MirrorP", {"position": v(-32.5, -86.5) * mm});
            skArc(sketch, "E972.MirrorCS", {"start": v(-66.5, -93.82) * mm, "mid": v(-61.3, -97.3) * mm, "end": v(-55.9, -100.5) * mm});
            skPoint(sketch, "E973.MirrorP", {"position": v(-52.5, 1.5) * mm});
            skPoint(sketch, "E974.MirrorP", {"position": v(-1.5, 100.5) * mm});
            skLineSegment(sketch, "E975.MirrorCS", {"start": v(-2.5, 1.5) * mm, "end": v(-14.5, 1.5) * mm});
            skPoint(sketch, "E976.MirrorP", {"position": v(-35.5, -83.5) * mm});
            skLineSegment(sketch, "E977.MirrorCS", {"start": v(-103.5, -2.5) * mm, "end": v(-103.5, -14.5) * mm});
            skPoint(sketch, "E978.MirrorP", {"position": v(-69.5, -1.5) * mm});
            skPoint(sketch, "E979.MirrorP", {"position": v(-1.5, -1.5) * mm});
            skPoint(sketch, "E980.MirrorP", {"position": v(-1.5, 18.5) * mm});
            skLineSegment(sketch, "E981.MirrorCS", {"start": v(-15.5, -104.5) * mm, "end": v(-15.5, -113.95) * mm});
            skPoint(sketch, "E982.MirrorP", {"position": v(-35.5, 69.5) * mm});
            skPoint(sketch, "E983.MirrorP", {"position": v(-18.5, -15.5) * mm});
            skPoint(sketch, "E984.MirrorP", {"position": v(-15.5, -18.5) * mm});
            skLineSegment(sketch, "E985.MirrorCS", {"start": v(-2.5, 15.5) * mm, "end": v(-14.5, 15.5) * mm});
            skPoint(sketch, "E986.MirrorP", {"position": v(-69.5, -66.5) * mm});
            skArc(sketch, "E987.MirrorCS", {"start": v(-100.5, -55.9) * mm, "mid": v(-97.3, -61.3) * mm, "end": v(-93.82, -66.5) * mm});
            skLineSegment(sketch, "E988.MirrorCS", {"start": v(-69.5, -36.5) * mm, "end": v(-69.5, -48.5) * mm});
            skArc(sketch, "E989.MirrorCS", {"start": v(-15.5, 65.5) * mm, "mid": v(-15.2, 66.2) * mm, "end": v(-14.5, 66.5) * mm});
            skLineSegment(sketch, "E990.MirrorCS", {"start": v(-2.5, -103.5) * mm, "end": v(-14.5, -103.5) * mm});
            skLineSegment(sketch, "E991.MirrorCS", {"start": v(-1.5, 2.5) * mm, "end": v(-1.5, 14.5) * mm});
            skArc(sketch, "E992.MirrorCS", {"start": v(-48.5, -52.5) * mm, "mid": v(-49.2, -52.8) * mm, "end": v(-49.5, -53.5) * mm});
            skArc(sketch, "E993.MirrorCS", {"start": v(-15.5, 99.5) * mm, "mid": v(-15.2, 100.2) * mm, "end": v(-14.5, 100.5) * mm});
            skArc(sketch, "E994.MirrorCS", {"start": v(-113.5, -18.5) * mm, "mid": v(-112.13, -25.55) * mm, "end": v(-110.31, -32.5) * mm});
            skArc(sketch, "E995.MirrorCS", {"start": v(-53.5, -83.5) * mm, "mid": v(-52.8, -83.2) * mm, "end": v(-52.5, -82.5) * mm});
            skLineSegment(sketch, "E996.MirrorCS", {"start": v(-19.5, 15.5) * mm, "end": v(-31.5, 15.5) * mm});
            skArc(sketch, "E997.MirrorCS", {"start": v(-1.5, 53.5) * mm, "mid": v(-1.8, 52.8) * mm, "end": v(-2.5, 52.5) * mm});
            skArc(sketch, "E998.MirrorCS", {"start": v(-53.5, -66.5) * mm, "mid": v(-52.8, -66.2) * mm, "end": v(-52.5, -65.5) * mm});
            skLineSegment(sketch, "E999.MirrorCS", {"start": v(-15.5, 2.5) * mm, "end": v(-15.5, 14.5) * mm});
            skLineSegment(sketch, "E1000.MirrorCS", {"start": v(-53.5, -49.5) * mm, "end": v(-65.5, -49.5) * mm});
            skLineSegment(sketch, "E1001.MirrorCS", {"start": v(-19.5, 49.5) * mm, "end": v(-31.5, 49.5) * mm});
            skPoint(sketch, "E1002.MirrorP", {"position": v(-32.5, 100.5) * mm});
            skArc(sketch, "E1003.MirrorCS", {"start": v(-1.5, 87.5) * mm, "mid": v(-1.8, 86.8) * mm, "end": v(-2.5, 86.5) * mm});
            skLineSegment(sketch, "E1004.MirrorCS", {"start": v(-70.5, -66.5) * mm, "end": v(-82.5, -66.5) * mm});
            skArc(sketch, "E1005.MirrorCS", {"start": v(-31.5, -69.5) * mm, "mid": v(-32.2, -69.8) * mm, "end": v(-32.5, -70.5) * mm});
            skPoint(sketch, "E1006.MirrorP", {"position": v(-86.5, -69.5) * mm});
            skLineSegment(sketch, "E1007.MirrorCS", {"start": v(-19.5, 83.5) * mm, "end": v(-31.5, 83.5) * mm});
            skLineSegment(sketch, "E1008.MirrorCS", {"start": v(-32.5, 19.5) * mm, "end": v(-32.5, 31.5) * mm});
            skArc(sketch, "E1009.MirrorCS", {"start": v(-19.5, -66.5) * mm, "mid": v(-18.8, -66.2) * mm, "end": v(-18.5, -65.5) * mm});
            skPoint(sketch, "E1010.MirrorP", {"position": v(-18.5, 49.5) * mm});
            skPoint(sketch, "E1011.MirrorP", {"position": v(-52.5, 100.5) * mm});
            skLineSegment(sketch, "E1012.MirrorCS", {"start": v(-69.5, -87.5) * mm, "end": v(-69.5, -91.62) * mm});
            skArc(sketch, "E1013.MirrorCS", {"start": v(-2.5, 15.5) * mm, "mid": v(-1.8, 15.2) * mm, "end": v(-1.5, 14.5) * mm});
            skPoint(sketch, "E1014.MirrorP", {"position": v(-66.5, -66.5) * mm});
            skArc(sketch, "E1015.MirrorCS", {"start": v(-48.5, 1.5) * mm, "mid": v(-49.2, 1.8) * mm, "end": v(-49.5, 2.5) * mm});
            skPoint(sketch, "E1016.MirrorP", {"position": v(-100.5, -32.5) * mm});
            skLineSegment(sketch, "E1017.MirrorCS", {"start": v(-32.5, 53.5) * mm, "end": v(-32.5, 65.5) * mm});
            skLineSegment(sketch, "E1018.MirrorCS", {"start": v(-36.5, -52.5) * mm, "end": v(-48.5, -52.5) * mm});
            skArc(sketch, "E1019.MirrorCS", {"start": v(-2.5, 49.5) * mm, "mid": v(-1.8, 49.2) * mm, "end": v(-1.5, 48.5) * mm});
            skLineSegment(sketch, "E1020.MirrorCS", {"start": v(-32.5, -2.5) * mm, "end": v(-32.5, -14.5) * mm});
            skArc(sketch, "E1021.MirrorCS", {"start": v(-48.5, 35.5) * mm, "mid": v(-49.2, 35.8) * mm, "end": v(-49.5, 36.5) * mm});
            skLineSegment(sketch, "E1022.MirrorCS", {"start": v(-32.5, 87.5) * mm, "end": v(-32.5, 99.5) * mm});
            skLineSegment(sketch, "E1023.MirrorCS", {"start": v(-100.5, -19.5) * mm, "end": v(-100.5, -31.5) * mm});
            skArc(sketch, "E1024.MirrorCS", {"start": v(-2.5, 83.5) * mm, "mid": v(-1.8, 83.2) * mm, "end": v(-1.5, 82.5) * mm});
            skArc(sketch, "E1025.MirrorCS", {"start": v(-15.5, 14.5) * mm, "mid": v(-15.2, 15.2) * mm, "end": v(-14.5, 15.5) * mm});
            skPoint(sketch, "E1026.MirrorP", {"position": v(-18.5, 69.5) * mm});
            skArc(sketch, "E1027.MirrorCS", {"start": v(-48.5, 69.5) * mm, "mid": v(-49.2, 69.8) * mm, "end": v(-49.5, 70.5) * mm});
            skPoint(sketch, "E1028.MirrorP", {"position": v(-83.5, 69.5) * mm});
            skPoint(sketch, "E1029.MirrorP", {"position": v(-18.5, -86.5) * mm});
            skPoint(sketch, "E1030.MirrorP", {"position": v(-100.5, 15.5) * mm});
            skArc(sketch, "E1031.MirrorCS", {"start": v(-36.5, 15.5) * mm, "mid": v(-35.8, 15.2) * mm, "end": v(-35.5, 14.5) * mm});
            skPoint(sketch, "E1032.MirrorP", {"position": v(-49.5, -103.5) * mm});
            skArc(sketch, "E1033.MirrorCS", {"start": v(-2.5, -49.5) * mm, "mid": v(-1.8, -49.2) * mm, "end": v(-1.5, -48.5) * mm});
            skPoint(sketch, "E1034.MirrorP", {"position": v(-83.5, -35.5) * mm});
            skLineSegment(sketch, "E1035.MirrorCS", {"start": v(-19.5, 1.5) * mm, "end": v(-31.5, 1.5) * mm});
            skArc(sketch, "E1036.MirrorCS", {"start": v(-48.5, 103.5) * mm, "mid": v(-48.95, 103.6) * mm, "end": v(-49.3, 103.9) * mm});
            skArc(sketch, "E1037.MirrorCS", {"start": v(-36.5, 49.5) * mm, "mid": v(-35.8, 49.2) * mm, "end": v(-35.5, 48.5) * mm});
            skPoint(sketch, "E1038.MirrorP", {"position": v(-32.5, 1.5) * mm});
            skPoint(sketch, "E1039.MirrorP", {"position": v(-66.5, 52.5) * mm});
            skLineSegment(sketch, "E1040.MirrorCS", {"start": v(-19.5, -35.5) * mm, "end": v(-31.5, -35.5) * mm});
            skPoint(sketch, "E1041.MirrorP", {"position": v(-69.5, 49.5) * mm});
            skLineSegment(sketch, "E1042.MirrorCS", {"start": v(-19.5, 35.5) * mm, "end": v(-31.5, 35.5) * mm});
            skArc(sketch, "E1043.MirrorCS", {"start": v(-1.5, 2.5) * mm, "mid": v(-1.8, 1.8) * mm, "end": v(-2.5, 1.5) * mm});
            skArc(sketch, "E1044.MirrorCS", {"start": v(-53.5, 32.5) * mm, "mid": v(-52.8, 32.2) * mm, "end": v(-52.5, 31.5) * mm});
            skArc(sketch, "E1045.MirrorCS", {"start": v(-36.5, 83.5) * mm, "mid": v(-35.8, 83.2) * mm, "end": v(-35.5, 82.5) * mm});
            skArc(sketch, "E1046.MirrorCS", {"start": v(-69.5, -2.5) * mm, "mid": v(-69.8, -1.8) * mm, "end": v(-70.5, -1.5) * mm});
            skLineSegment(sketch, "E1047.MirrorCS", {"start": v(-19.5, 69.5) * mm, "end": v(-31.5, 69.5) * mm});
            skArc(sketch, "E1048.MirrorCS", {"start": v(-53.5, 66.5) * mm, "mid": v(-52.8, 66.2) * mm, "end": v(-52.5, 65.5) * mm});
            skArc(sketch, "E1049.MirrorCS", {"start": v(-65.5, 1.5) * mm, "mid": v(-66.2, 1.8) * mm, "end": v(-66.5, 2.5) * mm});
            skLineSegment(sketch, "E1050.MirrorCS", {"start": v(-35.5, -53.5) * mm, "end": v(-35.5, -65.5) * mm});
            skLineSegment(sketch, "E1051.MirrorCS", {"start": v(-19.5, 103.5) * mm, "end": v(-31.5, 103.5) * mm});
            skLineSegment(sketch, "E1052.MirrorCS", {"start": v(-53.5, 100.5) * mm, "end": v(-55.9, 100.5) * mm});
            skArc(sketch, "E1053.MirrorCS", {"start": v(-65.5, 35.5) * mm, "mid": v(-66.2, 35.8) * mm, "end": v(-66.5, 36.5) * mm});
            skLineSegment(sketch, "E1054.MirrorCS", {"start": v(-15.5, -2.5) * mm, "end": v(-15.5, -14.5) * mm});
            skArc(sketch, "E1055.MirrorCS", {"start": v(-49.5, 31.5) * mm, "mid": v(-49.2, 32.2) * mm, "end": v(-48.5, 32.5) * mm});
            skLineSegment(sketch, "E1056.MirrorCS", {"start": v(-70.5, 32.5) * mm, "end": v(-82.5, 32.5) * mm});
            skArc(sketch, "E1057.MirrorCS", {"start": v(-65.5, 69.5) * mm, "mid": v(-66.2, 69.8) * mm, "end": v(-66.5, 70.5) * mm});
            skLineSegment(sketch, "E1058.MirrorCS", {"start": v(-2.5, -52.5) * mm, "end": v(-14.5, -52.5) * mm});
            skArc(sketch, "E1059.MirrorCS", {"start": v(-49.5, 65.5) * mm, "mid": v(-49.2, 66.2) * mm, "end": v(-48.5, 66.5) * mm});
            skLineSegment(sketch, "E1060.MirrorCS", {"start": v(-70.5, 66.5) * mm, "end": v(-82.5, 66.5) * mm});
            skLineSegment(sketch, "E1061.MirrorCS", {"start": v(-83.5, 2.5) * mm, "end": v(-83.5, 14.5) * mm});
            skPoint(sketch, "E1062.MirrorP", {"position": v(-1.5, 49.5) * mm});
            skArc(sketch, "E1063.MirrorCS", {"start": v(-49.5, 99.5) * mm, "mid": v(-49.2, 100.2) * mm, "end": v(-48.5, 100.5) * mm});
            skPoint(sketch, "E1064.MirrorP", {"position": v(-35.5, 100.5) * mm});
            skLineSegment(sketch, "E1065.MirrorCS", {"start": v(-86.5, 2.5) * mm, "end": v(-86.5, 14.5) * mm});
            skArc(sketch, "E1066.MirrorCS", {"start": v(-14.5, 1.5) * mm, "mid": v(-15.2, 1.8) * mm, "end": v(-15.5, 2.5) * mm});
            skPoint(sketch, "E1067.MirrorP", {"position": v(-32.5, -18.5) * mm});
            skLineSegment(sketch, "E1068.MirrorCS", {"start": v(-83.5, 36.5) * mm, "end": v(-83.5, 48.5) * mm});
            skArc(sketch, "E1069.MirrorCS", {"start": v(-52.5, 2.5) * mm, "mid": v(-52.8, 1.8) * mm, "end": v(-53.5, 1.5) * mm});
            skLineSegment(sketch, "E1070.MirrorCS", {"start": v(-86.5, 36.5) * mm, "end": v(-86.5, 48.5) * mm});
            skPoint(sketch, "E1071.MirrorP", {"position": v(-35.5, 18.5) * mm});
            skLineSegment(sketch, "E1072.MirrorCS", {"start": v(-83.5, 70.5) * mm, "end": v(-83.5, 79.07) * mm});
            skPoint(sketch, "E1073.MirrorP", {"position": v(-103.5, 1.5) * mm});
            skArc(sketch, "E1074.MirrorCS", {"start": v(-52.5, 36.5) * mm, "mid": v(-52.8, 35.8) * mm, "end": v(-53.5, 35.5) * mm});
            skArc(sketch, "E1075.MirrorCS", {"start": v(-104.5, 15.5) * mm, "mid": v(-103.8, 15.2) * mm, "end": v(-103.5, 14.5) * mm});
            skLineSegment(sketch, "E1076.MirrorCS", {"start": v(-2.5, 18.5) * mm, "end": v(-14.5, 18.5) * mm});
            skLineSegment(sketch, "E1077.MirrorCS", {"start": v(-87.5, 18.5) * mm, "end": v(-99.5, 18.5) * mm});
            skArc(sketch, "E1078.MirrorCS", {"start": v(-52.5, 70.5) * mm, "mid": v(-52.8, 69.8) * mm, "end": v(-53.5, 69.5) * mm});
            skArc(sketch, "E1079.MirrorCS", {"start": v(-100.5, 55.9) * mm, "mid": v(-97.3, 61.3) * mm, "end": v(-93.82, 66.5) * mm});
            skPoint(sketch, "E1080.MirrorP", {"position": v(-49.5, 49.5) * mm});
            skLineSegment(sketch, "E1081.MirrorCS", {"start": v(-87.5, 52.5) * mm, "end": v(-99.5, 52.5) * mm});
            skPoint(sketch, "E1082.MirrorP", {"position": v(-15.5, -100.5) * mm});
            skLineSegment(sketch, "E1083.MirrorCS", {"start": v(-70.5, 18.5) * mm, "end": v(-82.5, 18.5) * mm});
            skPoint(sketch, "E1084.MirrorP", {"position": v(-18.5, -1.5) * mm});
            skArc(sketch, "E1085.MirrorCS", {"start": v(-1.5, -2.5) * mm, "mid": v(-1.8, -1.8) * mm, "end": v(-2.5, -1.5) * mm});
            skLineSegment(sketch, "E1086.MirrorCS", {"start": v(-103.5, 19.5) * mm, "end": v(-103.5, 31.5) * mm});
            skArc(sketch, "E1087.MirrorCS", {"start": v(-14.5, 18.5) * mm, "mid": v(-15.2, 18.8) * mm, "end": v(-15.5, 19.5) * mm});
            skLineSegment(sketch, "E1088.MirrorCS", {"start": v(-70.5, 52.5) * mm, "end": v(-82.5, 52.5) * mm});
            skArc(sketch, "E1089.MirrorCS", {"start": v(-1.5, -53.5) * mm, "mid": v(-1.8, -52.8) * mm, "end": v(-2.5, -52.5) * mm});
            skArc(sketch, "E1090.MirrorCS", {"start": v(-66.5, 93.82) * mm, "mid": v(-61.3, 97.3) * mm, "end": v(-55.9, 100.5) * mm});
            skPoint(sketch, "E1091.MirrorP", {"position": v(-69.5, -69.5) * mm});
            skLineSegment(sketch, "E1092.MirrorCS", {"start": v(-69.5, 87.5) * mm, "end": v(-69.5, 91.62) * mm});
            skLineSegment(sketch, "E1093.MirrorCS", {"start": v(-83.5, -53.5) * mm, "end": v(-83.5, -65.5) * mm});
            skArc(sketch, "E1094.MirrorCS", {"start": v(-32.5, -48.5) * mm, "mid": v(-32.2, -49.2) * mm, "end": v(-31.5, -49.5) * mm});
            skPoint(sketch, "E1095.MirrorP", {"position": v(-18.5, 66.5) * mm});
            skLineSegment(sketch, "E1096.MirrorCS", {"start": v(-87.5, 32.5) * mm, "end": v(-99.5, 32.5) * mm});
            skLineSegment(sketch, "E1097.MirrorCS", {"start": v(-15.5, 19.5) * mm, "end": v(-15.5, 31.5) * mm});
            skPoint(sketch, "E1098.MirrorP", {"position": v(-69.5, 69.5) * mm});
            skLineSegment(sketch, "E1099.MirrorCS", {"start": v(-32.5, -87.5) * mm, "end": v(-32.5, -99.5) * mm});
            skArc(sketch, "E1100.MirrorCS", {"start": v(-52.5, -53.5) * mm, "mid": v(-52.8, -52.8) * mm, "end": v(-53.5, -52.5) * mm});
            skArc(sketch, "E1101.MirrorCS", {"start": v(-86.5, 53.5) * mm, "mid": v(-86.8, 52.8) * mm, "end": v(-87.5, 52.5) * mm});
            skArc(sketch, "E1102.MirrorCS", {"start": v(-19.5, -49.5) * mm, "mid": v(-18.8, -49.2) * mm, "end": v(-18.5, -48.5) * mm});
            skLineSegment(sketch, "E1103.MirrorCS", {"start": v(-18.5, -70.5) * mm, "end": v(-18.5, -82.5) * mm});
            skArc(sketch, "E1104.MirrorCS", {"start": v(-103.9, 49.3) * mm, "mid": v(-103.6, 48.95) * mm, "end": v(-103.5, 48.5) * mm});
            skArc(sketch, "E1105.MirrorCS", {"start": v(-15.5, 31.5) * mm, "mid": v(-15.2, 32.2) * mm, "end": v(-14.5, 32.5) * mm});
            skArc(sketch, "E1106.MirrorCS", {"start": v(-86.5, -2.5) * mm, "mid": v(-86.8, -1.8) * mm, "end": v(-87.5, -1.5) * mm});
            skLineSegment(sketch, "E1107.MirrorCS", {"start": v(-86.5, -70.5) * mm, "end": v(-86.5, -75.78) * mm});
            skLineSegment(sketch, "E1108.MirrorCS", {"start": v(-2.5, -66.5) * mm, "end": v(-14.5, -66.5) * mm});
            skLineSegment(sketch, "E1109.MirrorCS", {"start": v(-19.5, -49.5) * mm, "end": v(-31.5, -49.5) * mm});
            skArc(sketch, "E1110.MirrorCS", {"start": v(-82.5, -35.5) * mm, "mid": v(-83.2, -35.8) * mm, "end": v(-83.5, -36.5) * mm});
            skArc(sketch, "E1111.MirrorCS", {"start": v(-65.5, -18.5) * mm, "mid": v(-66.2, -18.8) * mm, "end": v(-66.5, -19.5) * mm});
            skLineSegment(sketch, "E1112.MirrorCS", {"start": v(-1.5, 19.5) * mm, "end": v(-1.5, 31.5) * mm});
            skLineSegment(sketch, "E1113.MirrorCS", {"start": v(-36.5, -35.5) * mm, "end": v(-48.5, -35.5) * mm});
            skLineSegment(sketch, "E1114.MirrorCS", {"start": v(-70.5, -1.5) * mm, "end": v(-82.5, -1.5) * mm});
            skPoint(sketch, "E1115.MirrorP", {"position": v(-66.5, 1.5) * mm});
            skLineSegment(sketch, "E1116.MirrorCS", {"start": v(-2.5, -69.5) * mm, "end": v(-14.5, -69.5) * mm});
            skLineSegment(sketch, "E1117.MirrorCS", {"start": v(-15.5, -53.5) * mm, "end": v(-15.5, -65.5) * mm});
            skPoint(sketch, "E1118.MirrorP", {"position": v(-49.5, 66.5) * mm});
            skArc(sketch, "E1119.MirrorCS", {"start": v(-35.5, -53.5) * mm, "mid": v(-35.8, -52.8) * mm, "end": v(-36.5, -52.5) * mm});
            skPoint(sketch, "E1120.MirrorP", {"position": v(-18.5, -35.5) * mm});
            skArc(sketch, "E1121.MirrorCS", {"start": v(-82.5, -69.5) * mm, "mid": v(-83.2, -69.8) * mm, "end": v(-83.5, -70.5) * mm});
            skPoint(sketch, "E1122.MirrorP", {"position": v(-1.5, 66.5) * mm});
            skLineSegment(sketch, "E1123.MirrorCS", {"start": v(-36.5, -69.5) * mm, "end": v(-48.5, -69.5) * mm});
            skPoint(sketch, "E1124.MirrorP", {"position": v(-52.5, -83.5) * mm});
            skPoint(sketch, "E1125.MirrorP", {"position": v(-86.5, -15.5) * mm});
            skPoint(sketch, "E1126.MirrorP", {"position": v(-18.5, -83.5) * mm});
            skPoint(sketch, "E1127.MirrorP", {"position": v(-103.5, -15.5) * mm});
            skLineSegment(sketch, "E1128.MirrorCS", {"start": v(-52.5, -53.5) * mm, "end": v(-52.5, -65.5) * mm});
            skPoint(sketch, "E1129.MirrorP", {"position": v(-35.5, 35.5) * mm});
            skPoint(sketch, "E1130.MirrorP", {"position": v(-103.5, 35.5) * mm});
            skPoint(sketch, "E1131.MirrorP", {"position": v(-69.5, -18.5) * mm});
            skArc(sketch, "E1132.MirrorCS", {"start": v(-48.5, -103.5) * mm, "mid": v(-48.95, -103.6) * mm, "end": v(-49.3, -103.9) * mm});
            skLineSegment(sketch, "E1133.MirrorCS", {"start": v(-53.5, -100.5) * mm, "end": v(-55.9, -100.5) * mm});
            skLineSegment(sketch, "E1134.MirrorCS", {"start": v(-87.5, -52.5) * mm, "end": v(-99.5, -52.5) * mm});
            skLineSegment(sketch, "E1135.MirrorCS", {"start": v(-86.5, -2.5) * mm, "end": v(-86.5, -14.5) * mm});
            skArc(sketch, "E1136.MirrorCS", {"start": v(-14.5, -69.5) * mm, "mid": v(-15.2, -69.8) * mm, "end": v(-15.5, -70.5) * mm});
            skArc(sketch, "E1137.MirrorCS", {"start": v(-19.5, -100.5) * mm, "mid": v(-18.8, -100.2) * mm, "end": v(-18.5, -99.5) * mm});
            skLineSegment(sketch, "E1138.MirrorCS", {"start": v(-49.5, -70.5) * mm, "end": v(-49.5, -82.5) * mm});
            skLineSegment(sketch, "E1139.MirrorCS", {"start": v(-36.5, -86.5) * mm, "end": v(-48.5, -86.5) * mm});
            skLineSegment(sketch, "E1140.MirrorCS", {"start": v(-15.5, 53.5) * mm, "end": v(-15.5, 65.5) * mm});
            skLineSegment(sketch, "E1141.MirrorCS", {"start": v(-53.5, -66.5) * mm, "end": v(-65.5, -66.5) * mm});
            skPoint(sketch, "E1142.MirrorP", {"position": v(-32.5, 66.5) * mm});
            skLineSegment(sketch, "E1143.MirrorCS", {"start": v(-52.5, -19.5) * mm, "end": v(-52.5, -31.5) * mm});
            skArc(sketch, "E1144.MirrorCS", {"start": v(-1.5, -104.5) * mm, "mid": v(-1.8, -103.8) * mm, "end": v(-2.5, -103.5) * mm});
            skPoint(sketch, "E1145.MirrorP", {"position": v(-104.5, -49.5) * mm});
            skLineSegment(sketch, "E1146.MirrorCS", {"start": v(-15.5, 87.5) * mm, "end": v(-15.5, 99.5) * mm});
            skArc(sketch, "E1147.MirrorCS", {"start": v(-69.5, -53.5) * mm, "mid": v(-69.8, -52.8) * mm, "end": v(-70.5, -52.5) * mm});
            skLineSegment(sketch, "E1148.MirrorCS", {"start": v(-103.5, -19.5) * mm, "end": v(-103.5, -31.5) * mm});
            skPoint(sketch, "E1149.MirrorP", {"position": v(-18.5, 15.5) * mm});
            skLineSegment(sketch, "E1150.MirrorCS", {"start": v(-49.5, -19.5) * mm, "end": v(-49.5, -31.5) * mm});
            skPoint(sketch, "E1151.MirrorP", {"position": v(-52.5, 66.5) * mm});
            skArc(sketch, "E1152.MirrorCS", {"start": v(-19.5, 15.5) * mm, "mid": v(-18.8, 15.2) * mm, "end": v(-18.5, 14.5) * mm});
            skLineSegment(sketch, "E1153.MirrorCS", {"start": v(-19.5, -66.5) * mm, "end": v(-31.5, -66.5) * mm});
            skPoint(sketch, "E1154.MirrorP", {"position": v(-69.5, -83.5) * mm});
            skLineSegment(sketch, "E1155.MirrorCS", {"start": v(-2.5, 66.5) * mm, "end": v(-14.5, 66.5) * mm});
            skLineSegment(sketch, "E1156.MirrorCS", {"start": v(-49.5, -2.5) * mm, "end": v(-49.5, -14.5) * mm});
            skPoint(sketch, "E1157.MirrorP", {"position": v(-100.5, -1.5) * mm});
            skLineSegment(sketch, "E1158.MirrorCS", {"start": v(-2.5, -49.5) * mm, "end": v(-14.5, -49.5) * mm});
            skArc(sketch, "E1159.MirrorCS", {"start": v(-19.5, 49.5) * mm, "mid": v(-18.8, 49.2) * mm, "end": v(-18.5, 48.5) * mm});
            skArc(sketch, "E1160.MirrorCS", {"start": v(-48.5, -86.5) * mm, "mid": v(-49.2, -86.8) * mm, "end": v(-49.5, -87.5) * mm});
            skLineSegment(sketch, "E1161.MirrorCS", {"start": v(-2.5, 100.5) * mm, "end": v(-14.5, 100.5) * mm});
            skLineSegment(sketch, "E1162.MirrorCS", {"start": v(-35.5, -104.5) * mm, "end": v(-35.5, -109.38) * mm});
            skArc(sketch, "E1163.MirrorCS", {"start": v(-31.5, -35.5) * mm, "mid": v(-32.2, -35.8) * mm, "end": v(-32.5, -36.5) * mm});
            skArc(sketch, "E1164.MirrorCS", {"start": v(-19.5, 83.5) * mm, "mid": v(-18.8, 83.2) * mm, "end": v(-18.5, 82.5) * mm});
            skLineSegment(sketch, "E1165.MirrorCS", {"start": v(-70.5, -15.5) * mm, "end": v(-82.5, -15.5) * mm});
            skPoint(sketch, "E1166.MirrorP", {"position": v(-32.5, -69.5) * mm});
            skPoint(sketch, "E1167.MirrorP", {"position": v(-15.5, -83.5) * mm});
            skPoint(sketch, "E1168.MirrorP", {"position": v(-18.5, 35.5) * mm});
            skArc(sketch, "E1169.MirrorCS", {"start": v(-31.5, 18.5) * mm, "mid": v(-32.2, 18.8) * mm, "end": v(-32.5, 19.5) * mm});
            skArc(sketch, "E1170.MirrorCS", {"start": v(-104.5, -15.5) * mm, "mid": v(-103.8, -15.2) * mm, "end": v(-103.5, -14.5) * mm});
            skPoint(sketch, "E1171.MirrorP", {"position": v(-83.5, 66.5) * mm});
            skLineSegment(sketch, "E1172.MirrorCS", {"start": v(-2.5, -15.5) * mm, "end": v(-14.5, -15.5) * mm});
            skLineSegment(sketch, "E1173.MirrorCS", {"start": v(-36.5, 1.5) * mm, "end": v(-48.5, 1.5) * mm});
            skLineSegment(sketch, "E1174.MirrorCS", {"start": v(-2.5, -83.5) * mm, "end": v(-14.5, -83.5) * mm});
            skArc(sketch, "E1175.MirrorCS", {"start": v(-31.5, 52.5) * mm, "mid": v(-32.2, 52.8) * mm, "end": v(-32.5, 53.5) * mm});
            skLineSegment(sketch, "E1176.MirrorCS", {"start": v(-1.5, -104.5) * mm, "end": v(-1.5, -115) * mm});
            skPoint(sketch, "E1177.MirrorP", {"position": v(-66.5, 18.5) * mm});
            skLineSegment(sketch, "E1178.MirrorCS", {"start": v(-1.5, 36.5) * mm, "end": v(-1.5, 48.5) * mm});
            skArc(sketch, "E1179.MirrorCS", {"start": v(-2.5, -100.5) * mm, "mid": v(-1.8, -100.2) * mm, "end": v(-1.5, -99.5) * mm});
            skLineSegment(sketch, "E1180.MirrorCS", {"start": v(-36.5, 35.5) * mm, "end": v(-48.5, 35.5) * mm});
            skArc(sketch, "E1181.MirrorCS", {"start": v(-87.5, -32.5) * mm, "mid": v(-86.8, -32.2) * mm, "end": v(-86.5, -31.5) * mm});
            skArc(sketch, "E1182.MirrorCS", {"start": v(-31.5, 86.5) * mm, "mid": v(-32.2, 86.8) * mm, "end": v(-32.5, 87.5) * mm});
            skArc(sketch, "E1183.MirrorCS", {"start": v(-91.62, -69.5) * mm, "mid": v(-89.12, -72.69) * mm, "end": v(-86.5, -75.78) * mm});
            skLineSegment(sketch, "E1184.MirrorCS", {"start": v(-1.5, 70.5) * mm, "end": v(-1.5, 82.5) * mm});
            skLineSegment(sketch, "E1185.MirrorCS", {"start": v(-36.5, 69.5) * mm, "end": v(-48.5, 69.5) * mm});
            skLineSegment(sketch, "E1186.MirrorCS", {"start": v(-53.5, -52.5) * mm, "end": v(-65.5, -52.5) * mm});
            skLineSegment(sketch, "E1187.MirrorCS", {"start": v(-35.5, 2.5) * mm, "end": v(-35.5, 14.5) * mm});
            skLineSegment(sketch, "E1188.MirrorCS", {"start": v(-70.5, -83.5) * mm, "end": v(-79.07, -83.5) * mm});
            skArc(sketch, "E1189.MirrorCS", {"start": v(-1.5, 104.5) * mm, "mid": v(-1.8, 103.8) * mm, "end": v(-2.5, 103.5) * mm});
            skLineSegment(sketch, "E1190.MirrorCS", {"start": v(-36.5, 103.5) * mm, "end": v(-48.5, 103.5) * mm});
            skLineSegment(sketch, "E1191.MirrorCS", {"start": v(-19.5, -18.5) * mm, "end": v(-31.5, -18.5) * mm});
            skLineSegment(sketch, "E1192.MirrorCS", {"start": v(-35.5, 36.5) * mm, "end": v(-35.5, 48.5) * mm});
            skArc(sketch, "E1193.MirrorCS", {"start": v(-15.5, -113.95) * mm, "mid": v(-8.52, -114.68) * mm, "end": v(-1.5, -115) * mm});
            skArc(sketch, "E1194.MirrorCS", {"start": v(-18.5, 19.5) * mm, "mid": v(-18.8, 18.8) * mm, "end": v(-19.5, 18.5) * mm});
            skLineSegment(sketch, "E1195.MirrorCS", {"start": v(-52.5, 19.5) * mm, "end": v(-52.5, 31.5) * mm});
            skLineSegment(sketch, "E1196.MirrorCS", {"start": v(-35.5, 70.5) * mm, "end": v(-35.5, 82.5) * mm});
            skLineSegment(sketch, "E1197.MirrorCS", {"start": v(-104.5, -35.5) * mm, "end": v(-109.38, -35.5) * mm});
            skArc(sketch, "E1198.MirrorCS", {"start": v(-18.5, 53.5) * mm, "mid": v(-18.8, 52.8) * mm, "end": v(-19.5, 52.5) * mm});
            skLineSegment(sketch, "E1199.MirrorCS", {"start": v(-52.5, 53.5) * mm, "end": v(-52.5, 65.5) * mm});
            skLineSegment(sketch, "E1200.MirrorCS", {"start": v(-53.5, 1.5) * mm, "end": v(-65.5, 1.5) * mm});
            skLineSegment(sketch, "E1201.MirrorCS", {"start": v(-2.5, -1.5) * mm, "end": v(-14.5, -1.5) * mm});
            skPoint(sketch, "E1202.MirrorP", {"position": v(-1.5, 15.5) * mm});
            skArc(sketch, "E1203.MirrorCS", {"start": v(-18.5, 87.5) * mm, "mid": v(-18.8, 86.8) * mm, "end": v(-19.5, 86.5) * mm});
            skPoint(sketch, "E1204.MirrorP", {"position": v(-35.5, 66.5) * mm});
            skArc(sketch, "E1205.MirrorCS", {"start": v(-53.5, 100.5) * mm, "mid": v(-52.8, 100.2) * mm, "end": v(-52.5, 99.5) * mm});
            skLineSegment(sketch, "E1206.MirrorCS", {"start": v(-53.5, 35.5) * mm, "end": v(-65.5, 35.5) * mm});
            skArc(sketch, "E1207.MirrorCS", {"start": v(-1.5, -36.5) * mm, "mid": v(-1.8, -35.8) * mm, "end": v(-2.5, -35.5) * mm});
            skPoint(sketch, "E1208.MirrorP", {"position": v(-32.5, -66.5) * mm});
            skLineSegment(sketch, "E1209.MirrorCS", {"start": v(-49.5, 19.5) * mm, "end": v(-49.5, 31.5) * mm});
            skArc(sketch, "E1210.MirrorCS", {"start": v(-70.5, 32.5) * mm, "mid": v(-69.8, 32.2) * mm, "end": v(-69.5, 31.5) * mm});
            skLineSegment(sketch, "E1211.MirrorCS", {"start": v(-53.5, 69.5) * mm, "end": v(-65.5, 69.5) * mm});
            skArc(sketch, "E1212.MirrorCS", {"start": v(-15.5, -14.5) * mm, "mid": v(-15.2, -15.2) * mm, "end": v(-14.5, -15.5) * mm});
            skLineSegment(sketch, "E1213.MirrorCS", {"start": v(-49.5, 53.5) * mm, "end": v(-49.5, 65.5) * mm});
            skPoint(sketch, "E1214.MirrorP", {"position": v(-103.5, -35.5) * mm});
            skArc(sketch, "E1215.MirrorCS", {"start": v(-70.5, 66.5) * mm, "mid": v(-69.8, 66.2) * mm, "end": v(-69.5, 65.5) * mm});
            skArc(sketch, "E1216.MirrorCS", {"start": v(-82.5, 1.5) * mm, "mid": v(-83.2, 1.8) * mm, "end": v(-83.5, 2.5) * mm});
            skLineSegment(sketch, "E1217.MirrorCS", {"start": v(-49.5, 87.5) * mm, "end": v(-49.5, 99.5) * mm});
            skArc(sketch, "E1218.MirrorCS", {"start": v(-100.5, 14.5) * mm, "mid": v(-100.2, 15.2) * mm, "end": v(-99.5, 15.5) * mm});
            skPoint(sketch, "E1219.MirrorP", {"position": v(-49.5, 15.5) * mm});
            skArc(sketch, "E1220.MirrorCS", {"start": v(-82.5, 35.5) * mm, "mid": v(-83.2, 35.8) * mm, "end": v(-83.5, 36.5) * mm});
            skLineSegment(sketch, "E1221.MirrorCS", {"start": v(-53.5, 15.5) * mm, "end": v(-65.5, 15.5) * mm});
            skPoint(sketch, "E1222.MirrorP", {"position": v(-49.5, -104.5) * mm});
            skPoint(sketch, "E1223.MirrorP", {"position": v(-52.5, 86.5) * mm});
            skArc(sketch, "E1224.MirrorCS", {"start": v(-100.5, 48.5) * mm, "mid": v(-100.2, 49.2) * mm, "end": v(-99.5, 49.5) * mm});
            skArc(sketch, "E1225.MirrorCS", {"start": v(-82.5, 69.5) * mm, "mid": v(-83.2, 69.8) * mm, "end": v(-83.5, 70.5) * mm});
            skLineSegment(sketch, "E1226.MirrorCS", {"start": v(-53.5, 49.5) * mm, "end": v(-65.5, 49.5) * mm});
            skLineSegment(sketch, "E1227.MirrorCS", {"start": v(-103.5, 2.5) * mm, "end": v(-103.5, 14.5) * mm});
            skPoint(sketch, "E1228.MirrorP", {"position": v(-32.5, 83.5) * mm});
            skArc(sketch, "E1229.MirrorCS", {"start": v(-86.5, 2.5) * mm, "mid": v(-86.8, 1.8) * mm, "end": v(-87.5, 1.5) * mm});
            skLineSegment(sketch, "E1230.MirrorCS", {"start": v(-53.5, 83.5) * mm, "end": v(-65.5, 83.5) * mm});
            skPoint(sketch, "E1231.MirrorP", {"position": v(-49.5, -32.5) * mm});
            skArc(sketch, "E1232.MirrorCS", {"start": v(-109.38, 35.5) * mm, "mid": v(-106.86, 42.49) * mm, "end": v(-103.9, 49.3) * mm});
            skArc(sketch, "E1233.MirrorCS", {"start": v(-86.5, 36.5) * mm, "mid": v(-86.8, 35.8) * mm, "end": v(-87.5, 35.5) * mm});
            skPoint(sketch, "E1234.MirrorP", {"position": v(-18.5, 32.5) * mm});
            skPoint(sketch, "E1235.MirrorP", {"position": v(-52.5, 83.5) * mm});
            skArc(sketch, "E1236.MirrorCS", {"start": v(-69.5, 2.5) * mm, "mid": v(-69.8, 1.8) * mm, "end": v(-70.5, 1.5) * mm});
            skArc(sketch, "E1237.MirrorCS", {"start": v(-32.5, -14.5) * mm, "mid": v(-32.2, -15.2) * mm, "end": v(-31.5, -15.5) * mm});
            skPoint(sketch, "E1238.MirrorP", {"position": v(-86.5, -66.5) * mm});
            skLineSegment(sketch, "E1239.MirrorCS", {"start": v(-104.5, 18.5) * mm, "end": v(-113.5, 18.5) * mm});
            skArc(sketch, "E1240.MirrorCS", {"start": v(-69.5, 36.5) * mm, "mid": v(-69.8, 35.8) * mm, "end": v(-70.5, 35.5) * mm});
            skArc(sketch, "E1241.MirrorCS", {"start": v(-31.5, -86.5) * mm, "mid": v(-32.2, -86.8) * mm, "end": v(-32.5, -87.5) * mm});
            skArc(sketch, "E1242.MirrorCS", {"start": v(-75.78, 86.5) * mm, "mid": v(-72.69, 89.12) * mm, "end": v(-69.5, 91.62) * mm});
            skLineSegment(sketch, "E1243.MirrorCS", {"start": v(-70.5, 86.5) * mm, "end": v(-75.78, 86.5) * mm});
            skLineSegment(sketch, "E1244.MirrorCS", {"start": v(-36.5, -100.5) * mm, "end": v(-48.5, -100.5) * mm});
            skArc(sketch, "E1245.MirrorCS", {"start": v(-31.5, -18.5) * mm, "mid": v(-32.2, -18.8) * mm, "end": v(-32.5, -19.5) * mm});
            skArc(sketch, "E1246.MirrorCS", {"start": v(-87.5, 32.5) * mm, "mid": v(-86.8, 32.2) * mm, "end": v(-86.5, 31.5) * mm});
            skLineSegment(sketch, "E1247.MirrorCS", {"start": v(-53.5, -35.5) * mm, "end": v(-65.5, -35.5) * mm});
            skArc(sketch, "E1248.MirrorCS", {"start": v(-65.5, -86.5) * mm, "mid": v(-66.2, -86.8) * mm, "end": v(-66.5, -87.5) * mm});
            skLineSegment(sketch, "E1249.MirrorCS", {"start": v(-87.5, 66.5) * mm, "end": v(-93.82, 66.5) * mm});
            skArc(sketch, "E1250.MirrorCS", {"start": v(-36.5, -49.5) * mm, "mid": v(-35.8, -49.2) * mm, "end": v(-35.5, -48.5) * mm});
            skLineSegment(sketch, "E1251.MirrorCS", {"start": v(-32.5, -53.5) * mm, "end": v(-32.5, -65.5) * mm});
            skLineSegment(sketch, "E1252.MirrorCS", {"start": v(-103.5, 36.5) * mm, "end": v(-103.5, 48.5) * mm});
            skArc(sketch, "E1253.MirrorCS", {"start": v(-99.5, -35.5) * mm, "mid": v(-100.2, -35.8) * mm, "end": v(-100.5, -36.5) * mm});
            skPoint(sketch, "E1254.MirrorP", {"position": v(-35.5, -86.5) * mm});
            skLineSegment(sketch, "E1255.MirrorCS", {"start": v(-66.5, -87.5) * mm, "end": v(-66.5, -93.82) * mm});
            skPoint(sketch, "E1256.MirrorP", {"position": v(-49.5, -49.5) * mm});
            skPoint(sketch, "E1257.MirrorP", {"position": v(-32.5, -52.5) * mm});
            skLineSegment(sketch, "E1258.MirrorCS", {"start": v(-32.5, -104.5) * mm, "end": v(-32.5, -110.31) * mm});
            skLineSegment(sketch, "E1259.MirrorCS", {"start": v(-83.5, -2.5) * mm, "end": v(-83.5, -14.5) * mm});
            skArc(sketch, "E1260.MirrorCS", {"start": v(-83.5, -79.07) * mm, "mid": v(-81.32, -81.32) * mm, "end": v(-79.07, -83.5) * mm});
            skPoint(sketch, "E1261.MirrorP", {"position": v(-49.5, 32.5) * mm});
            skArc(sketch, "E1262.MirrorCS", {"start": v(-35.5, -104.5) * mm, "mid": v(-35.8, -103.8) * mm, "end": v(-36.5, -103.5) * mm});
            skPoint(sketch, "E1263.MirrorP", {"position": v(-15.5, -66.5) * mm});
            skPoint(sketch, "E1264.MirrorP", {"position": v(-83.5, -15.5) * mm});
            skArc(sketch, "E1265.MirrorCS", {"start": v(-15.5, -99.5) * mm, "mid": v(-15.2, -100.2) * mm, "end": v(-14.5, -100.5) * mm});
            skLineSegment(sketch, "E1266.MirrorCS", {"start": v(-83.5, -19.5) * mm, "end": v(-83.5, -31.5) * mm});
            skLineSegment(sketch, "E1267.MirrorCS", {"start": v(-1.5, -19.5) * mm, "end": v(-1.5, -31.5) * mm});
            skPoint(sketch, "E1268.MirrorP", {"position": v(-104.5, 49.5) * mm});
            skPoint(sketch, "E1269.MirrorP", {"position": v(-1.5, 32.5) * mm});
            skLineSegment(sketch, "E1270.MirrorCS", {"start": v(-2.5, -18.5) * mm, "end": v(-14.5, -18.5) * mm});
            skPoint(sketch, "E1271.MirrorP", {"position": v(-15.5, -15.5) * mm});
            skPoint(sketch, "E1272.MirrorP", {"position": v(-35.5, 83.5) * mm});
            skPoint(sketch, "E1273.MirrorP", {"position": v(-52.5, -15.5) * mm});
            skArc(sketch, "E1274.MirrorCS", {"start": v(-19.5, -15.5) * mm, "mid": v(-18.8, -15.2) * mm, "end": v(-18.5, -14.5) * mm});
            skPoint(sketch, "E1275.MirrorP", {"position": v(-35.5, 1.5) * mm});
            skArc(sketch, "E1276.MirrorCS", {"start": v(-99.5, -1.5) * mm, "mid": v(-100.2, -1.8) * mm, "end": v(-100.5, -2.5) * mm});
            skPoint(sketch, "E1277.MirrorP", {"position": v(-35.5, -69.5) * mm});
            skPoint(sketch, "E1278.MirrorP", {"position": v(-32.5, -103.5) * mm});
            skLineSegment(sketch, "E1279.MirrorCS", {"start": v(-19.5, -15.5) * mm, "end": v(-31.5, -15.5) * mm});
            skLineSegment(sketch, "E1280.MirrorCS", {"start": v(-100.5, -36.5) * mm, "end": v(-100.5, -48.5) * mm});
            skArc(sketch, "E1281.MirrorCS", {"start": v(-18.5, -36.5) * mm, "mid": v(-18.8, -35.8) * mm, "end": v(-19.5, -35.5) * mm});
            skLineSegment(sketch, "E1282.MirrorCS", {"start": v(-49.5, -36.5) * mm, "end": v(-49.5, -48.5) * mm});
            skArc(sketch, "E1283.MirrorCS", {"start": v(-48.5, -35.5) * mm, "mid": v(-49.2, -35.8) * mm, "end": v(-49.5, -36.5) * mm});
            skPoint(sketch, "E1284.MirrorP", {"position": v(-32.5, 32.5) * mm});
            skPoint(sketch, "E1285.MirrorP", {"position": v(-66.5, 83.5) * mm});
            skLineSegment(sketch, "E1286.MirrorCS", {"start": v(-53.5, -32.5) * mm, "end": v(-65.5, -32.5) * mm});
            skLineSegment(sketch, "E1287.MirrorCS", {"start": v(-36.5, -15.5) * mm, "end": v(-48.5, -15.5) * mm});
            skArc(sketch, "E1288.MirrorCS", {"start": v(-15.5, -48.5) * mm, "mid": v(-15.2, -49.2) * mm, "end": v(-14.5, -49.5) * mm});
            skPoint(sketch, "E1289.MirrorP", {"position": v(-52.5, 32.5) * mm});
            skLineSegment(sketch, "E1290.MirrorCS", {"start": v(-66.5, -2.5) * mm, "end": v(-66.5, -14.5) * mm});
            skPoint(sketch, "E1291.MirrorP", {"position": v(-32.5, -49.5) * mm});
            skLineSegment(sketch, "E1292.MirrorCS", {"start": v(-19.5, -32.5) * mm, "end": v(-31.5, -32.5) * mm});
            skArc(sketch, "E1293.MirrorCS", {"start": v(-14.5, 52.5) * mm, "mid": v(-15.2, 52.8) * mm, "end": v(-15.5, 53.5) * mm});
            skArc(sketch, "E1294.MirrorCS", {"start": v(-83.5, -14.5) * mm, "mid": v(-83.2, -15.2) * mm, "end": v(-82.5, -15.5) * mm});
            skLineSegment(sketch, "E1295.MirrorCS", {"start": v(-100.5, -2.5) * mm, "end": v(-100.5, -14.5) * mm});
            skLineSegment(sketch, "E1296.MirrorCS", {"start": v(-100.5, -53.5) * mm, "end": v(-100.5, -55.9) * mm});
            skPoint(sketch, "E1297.MirrorP", {"position": v(-15.5, 86.5) * mm});
            skPoint(sketch, "E1298.MirrorP", {"position": v(-18.5, 1.5) * mm});
            skArc(sketch, "E1299.MirrorCS", {"start": v(-14.5, 86.5) * mm, "mid": v(-15.2, 86.8) * mm, "end": v(-15.5, 87.5) * mm});
            skArc(sketch, "E1300.MirrorCS", {"start": v(-66.5, -48.5) * mm, "mid": v(-66.2, -49.2) * mm, "end": v(-65.5, -49.5) * mm});
            skPoint(sketch, "E1301.MirrorP", {"position": v(-83.5, 32.5) * mm});
            skPoint(sketch, "E1302.MirrorP", {"position": v(-52.5, 52.5) * mm});
            skPoint(sketch, "E1303.MirrorP", {"position": v(-103.5, -1.5) * mm});
            skArc(sketch, "E1304.MirrorCS", {"start": v(-48.5, -69.5) * mm, "mid": v(-49.2, -69.8) * mm, "end": v(-49.5, -70.5) * mm});
            skPoint(sketch, "E1305.MirrorP", {"position": v(-86.5, -32.5) * mm});
            skArc(sketch, "E1306.MirrorCS", {"start": v(-2.5, -83.5) * mm, "mid": v(-1.8, -83.2) * mm, "end": v(-1.5, -82.5) * mm});
            skLineSegment(sketch, "E1307.MirrorCS", {"start": v(-18.5, 2.5) * mm, "end": v(-18.5, 14.5) * mm});
            skLineSegment(sketch, "E1308.MirrorCS", {"start": v(-104.5, -15.5) * mm, "end": v(-113.95, -15.5) * mm});
            skArc(sketch, "E1309.MirrorCS", {"start": v(-2.5, 66.5) * mm, "mid": v(-1.8, 66.2) * mm, "end": v(-1.5, 65.5) * mm});
            skLineSegment(sketch, "E1310.MirrorCS", {"start": v(-36.5, -49.5) * mm, "end": v(-48.5, -49.5) * mm});
            skPoint(sketch, "E1311.MirrorP", {"position": v(-49.5, 103.5) * mm});
            skLineSegment(sketch, "E1312.MirrorCS", {"start": v(-2.5, -32.5) * mm, "end": v(-14.5, -32.5) * mm});
            skLineSegment(sketch, "E1313.MirrorCS", {"start": v(-18.5, 36.5) * mm, "end": v(-18.5, 48.5) * mm});
            skLineSegment(sketch, "E1314.MirrorCS", {"start": v(-104.5, -32.5) * mm, "end": v(-110.31, -32.5) * mm});
            skPoint(sketch, "E1315.MirrorP", {"position": v(-1.5, -69.5) * mm});
            skArc(sketch, "E1316.MirrorCS", {"start": v(-2.5, 100.5) * mm, "mid": v(-1.8, 100.2) * mm, "end": v(-1.5, 99.5) * mm});
            skLineSegment(sketch, "E1317.MirrorCS", {"start": v(-15.5, -36.5) * mm, "end": v(-15.5, -48.5) * mm});
            skArc(sketch, "E1318.MirrorCS", {"start": v(-49.5, -99.5) * mm, "mid": v(-49.2, -100.2) * mm, "end": v(-48.5, -100.5) * mm});
            skLineSegment(sketch, "E1319.MirrorCS", {"start": v(-18.5, 70.5) * mm, "end": v(-18.5, 82.5) * mm});
            skLineSegment(sketch, "E1320.MirrorCS", {"start": v(-19.5, -1.5) * mm, "end": v(-31.5, -1.5) * mm});
            skLineSegment(sketch, "E1321.MirrorCS", {"start": v(-19.5, 18.5) * mm, "end": v(-31.5, 18.5) * mm});
            skArc(sketch, "E1322.MirrorCS", {"start": v(-52.5, -87.5) * mm, "mid": v(-52.8, -86.8) * mm, "end": v(-53.5, -86.5) * mm});
            skLineSegment(sketch, "E1323.MirrorCS", {"start": v(-35.5, -87.5) * mm, "end": v(-35.5, -99.5) * mm});
            skArc(sketch, "E1324.MirrorCS", {"start": v(-18.5, 104.5) * mm, "mid": v(-18.8, 103.8) * mm, "end": v(-19.5, 103.5) * mm});
            skLineSegment(sketch, "E1325.MirrorCS", {"start": v(-19.5, -103.5) * mm, "end": v(-31.5, -103.5) * mm});
            skLineSegment(sketch, "E1326.MirrorCS", {"start": v(-19.5, 52.5) * mm, "end": v(-31.5, 52.5) * mm});
            skArc(sketch, "E1327.MirrorCS", {"start": v(-87.5, -15.5) * mm, "mid": v(-86.8, -15.2) * mm, "end": v(-86.5, -14.5) * mm});
            skArc(sketch, "E1328.MirrorCS", {"start": v(-15.5, 48.5) * mm, "mid": v(-15.2, 49.2) * mm, "end": v(-14.5, 49.5) * mm});
            skArc(sketch, "E1329.MirrorCS", {"start": v(-69.5, -87.5) * mm, "mid": v(-69.8, -86.8) * mm, "end": v(-70.5, -86.5) * mm});
            skArc(sketch, "E1330.MirrorCS", {"start": v(-35.5, 19.5) * mm, "mid": v(-35.8, 18.8) * mm, "end": v(-36.5, 18.5) * mm});
            skArc(sketch, "E1331.MirrorCS", {"start": v(-52.5, -2.5) * mm, "mid": v(-52.8, -1.8) * mm, "end": v(-53.5, -1.5) * mm});
            skLineSegment(sketch, "E1332.MirrorCS", {"start": v(-19.5, 86.5) * mm, "end": v(-31.5, 86.5) * mm});
            skLineSegment(sketch, "E1333.MirrorCS", {"start": v(-52.5, -36.5) * mm, "end": v(-52.5, -48.5) * mm});
            skArc(sketch, "E1334.MirrorCS", {"start": v(-15.5, 82.5) * mm, "mid": v(-15.2, 83.2) * mm, "end": v(-14.5, 83.5) * mm});
            skArc(sketch, "E1335.MirrorCS", {"start": v(-35.5, 53.5) * mm, "mid": v(-35.8, 52.8) * mm, "end": v(-36.5, 52.5) * mm});
            skLineSegment(sketch, "E1336.MirrorCS", {"start": v(-87.5, -32.5) * mm, "end": v(-99.5, -32.5) * mm});
            skArc(sketch, "E1337.MirrorCS", {"start": v(-49.5, 14.5) * mm, "mid": v(-49.2, 15.2) * mm, "end": v(-48.5, 15.5) * mm});
            skArc(sketch, "E1338.MirrorCS", {"start": v(-53.5, -15.5) * mm, "mid": v(-52.8, -15.2) * mm, "end": v(-52.5, -14.5) * mm});
            skLineSegment(sketch, "E1339.MirrorCS", {"start": v(-1.5, 104.5) * mm, "end": v(-1.5, 115) * mm});
            skPoint(sketch, "E1340.MirrorP", {"position": v(-35.5, 32.5) * mm});
            skArc(sketch, "E1341.MirrorCS", {"start": v(-35.5, 87.5) * mm, "mid": v(-35.8, 86.8) * mm, "end": v(-36.5, 86.5) * mm});
            skArc(sketch, "E1342.MirrorCS", {"start": v(-86.5, -19.5) * mm, "mid": v(-86.8, -18.8) * mm, "end": v(-87.5, -18.5) * mm});
            skPoint(sketch, "E1343.MirrorP", {"position": v(-86.5, 69.5) * mm});
            skPoint(sketch, "E1344.MirrorP", {"position": v(-18.5, -100.5) * mm});
            skArc(sketch, "E1345.MirrorCS", {"start": v(-49.5, 48.5) * mm, "mid": v(-49.2, 49.2) * mm, "end": v(-48.5, 49.5) * mm});
            skLineSegment(sketch, "E1346.MirrorCS", {"start": v(-70.5, -49.5) * mm, "end": v(-82.5, -49.5) * mm});
            skLineSegment(sketch, "E1347.MirrorCS", {"start": v(-19.5, 32.5) * mm, "end": v(-31.5, 32.5) * mm});
            skArc(sketch, "E1348.MirrorCS", {"start": v(-66.5, 31.5) * mm, "mid": v(-66.2, 32.2) * mm, "end": v(-65.5, 32.5) * mm});
            skArc(sketch, "E1349.MirrorCS", {"start": v(-49.5, 82.5) * mm, "mid": v(-49.2, 83.2) * mm, "end": v(-48.5, 83.5) * mm});
            skArc(sketch, "E1350.MirrorCS", {"start": v(-49.5, -65.5) * mm, "mid": v(-49.2, -66.2) * mm, "end": v(-48.5, -66.5) * mm});
            skLineSegment(sketch, "E1351.MirrorCS", {"start": v(-19.5, 66.5) * mm, "end": v(-31.5, 66.5) * mm});
            skPoint(sketch, "E1352.MirrorP", {"position": v(-18.5, -103.5) * mm});
            skArc(sketch, "E1353.MirrorCS", {"start": v(-66.5, 65.5) * mm, "mid": v(-66.2, 66.2) * mm, "end": v(-65.5, 66.5) * mm});
            skArc(sketch, "E1354.MirrorCS", {"start": v(-35.5, 104.5) * mm, "mid": v(-35.8, 103.8) * mm, "end": v(-36.5, 103.5) * mm});
            skArc(sketch, "E1355.MirrorCS", {"start": v(-52.5, -70.5) * mm, "mid": v(-52.8, -69.8) * mm, "end": v(-53.5, -69.5) * mm});
            skLineSegment(sketch, "E1356.MirrorCS", {"start": v(-19.5, 100.5) * mm, "end": v(-31.5, 100.5) * mm});
            skLineSegment(sketch, "E1357.MirrorCS", {"start": v(-52.5, 87.5) * mm, "end": v(-52.5, 99.5) * mm});
            skArc(sketch, "E1358.MirrorCS", {"start": v(-52.5, 19.5) * mm, "mid": v(-52.8, 18.8) * mm, "end": v(-53.5, 18.5) * mm});
            skArc(sketch, "E1359.MirrorCS", {"start": v(-103.9, -49.3) * mm, "mid": v(-103.6, -48.95) * mm, "end": v(-103.5, -48.5) * mm});
            skPoint(sketch, "E1360.MirrorP", {"position": v(-52.5, -100.5) * mm});
            skArc(sketch, "E1361.MirrorCS", {"start": v(-48.5, 18.5) * mm, "mid": v(-49.2, 18.8) * mm, "end": v(-49.5, 19.5) * mm});
            skPoint(sketch, "E1362.MirrorP", {"position": v(-86.5, 18.5) * mm});
            skPoint(sketch, "E1363.MirrorP", {"position": v(-49.5, -66.5) * mm});
            skPoint(sketch, "E1364.MirrorP", {"position": v(-66.5, -18.5) * mm});
            skLineSegment(sketch, "E1365.MirrorCS", {"start": v(-69.5, 19.5) * mm, "end": v(-69.5, 31.5) * mm});
            skArc(sketch, "E1366.MirrorCS", {"start": v(-52.5, 53.5) * mm, "mid": v(-52.8, 52.8) * mm, "end": v(-53.5, 52.5) * mm});
            skArc(sketch, "E1367.MirrorCS", {"start": v(-103.5, -36.5) * mm, "mid": v(-103.8, -35.8) * mm, "end": v(-104.5, -35.5) * mm});
            skArc(sketch, "E1368.MirrorCS", {"start": v(-48.5, 52.5) * mm, "mid": v(-49.2, 52.8) * mm, "end": v(-49.5, 53.5) * mm});
            skLineSegment(sketch, "E1369.MirrorCS", {"start": v(-69.5, 53.5) * mm, "end": v(-69.5, 65.5) * mm});
            skPoint(sketch, "E1370.MirrorP", {"position": v(-32.5, 49.5) * mm});
            skLineSegment(sketch, "E1371.MirrorCS", {"start": v(-70.5, 1.5) * mm, "end": v(-82.5, 1.5) * mm});
            skArc(sketch, "E1372.MirrorCS", {"start": v(-48.5, 86.5) * mm, "mid": v(-49.2, 86.8) * mm, "end": v(-49.5, 87.5) * mm});
            skPoint(sketch, "E1373.MirrorP", {"position": v(-86.5, -1.5) * mm});
            skLineSegment(sketch, "E1374.MirrorCS", {"start": v(-100.5, 2.5) * mm, "end": v(-100.5, 14.5) * mm});
            skLineSegment(sketch, "E1375.MirrorCS", {"start": v(-70.5, 35.5) * mm, "end": v(-82.5, 35.5) * mm});
            skPoint(sketch, "E1376.MirrorP", {"position": v(-52.5, 49.5) * mm});
            skArc(sketch, "E1377.MirrorCS", {"start": v(-53.5, 15.5) * mm, "mid": v(-52.8, 15.2) * mm, "end": v(-52.5, 14.5) * mm});
            skLineSegment(sketch, "E1378.MirrorCS", {"start": v(-100.5, 36.5) * mm, "end": v(-100.5, 48.5) * mm});
            skSolve(sketch);
        }
        {
            var Q0;
            Q0 = qSketchRegion(id + "F2", true);
            extrude(context, id + "F3", {"entities" : qUnion([Q0]), "operationType" : NewBodyOperationType.REMOVE, "endBound" : BoundingType.THROUGH_ALL, "oppositeDirection" : true, "depth" : 25 * mm});
        }
    });
